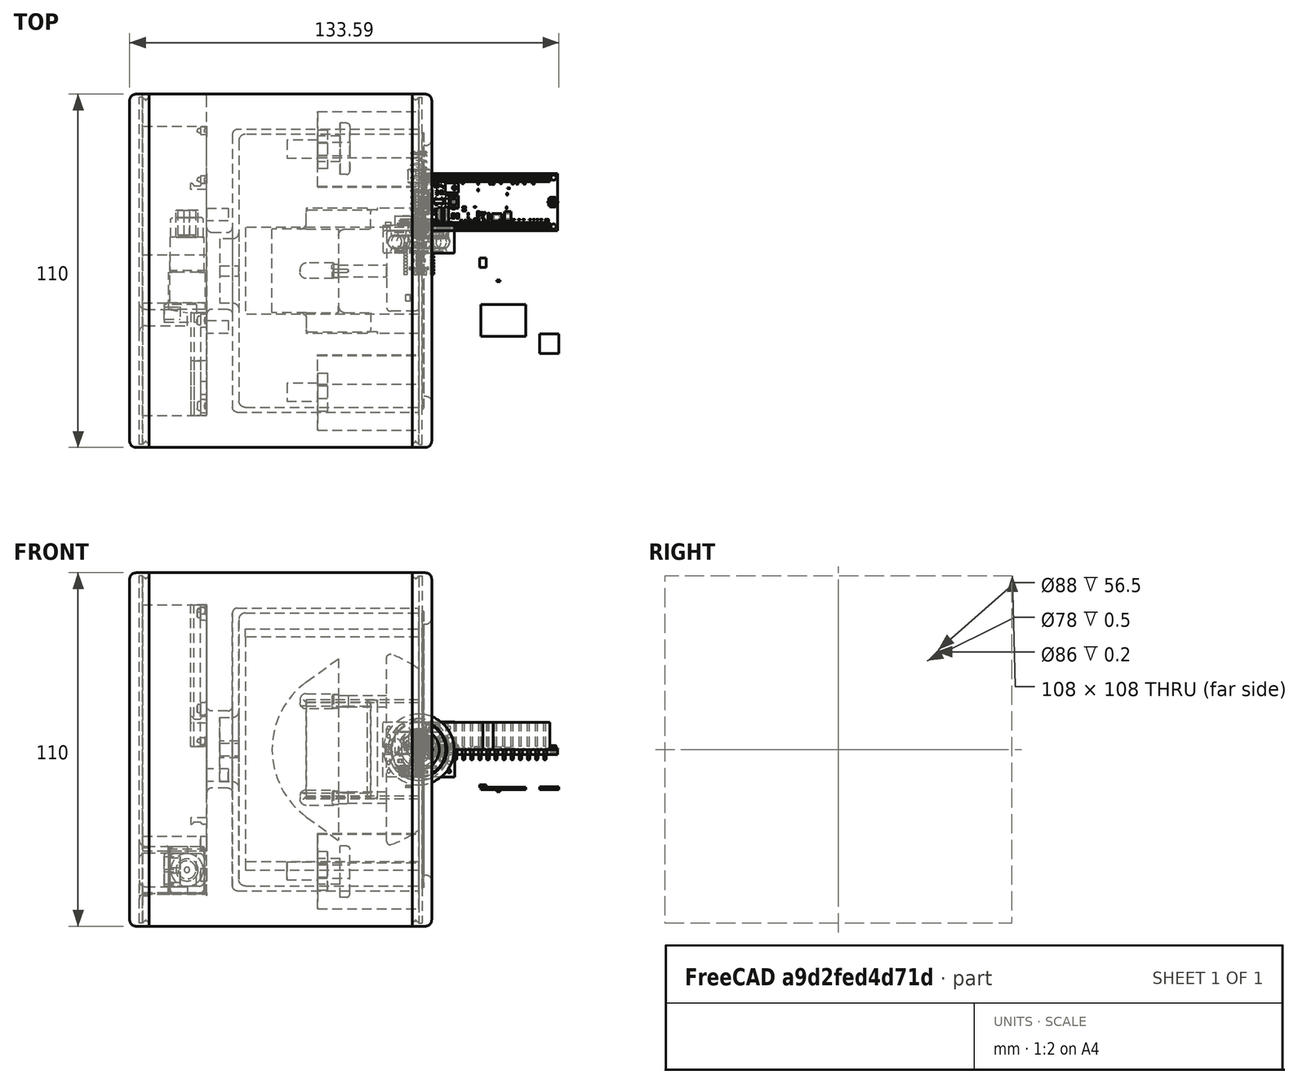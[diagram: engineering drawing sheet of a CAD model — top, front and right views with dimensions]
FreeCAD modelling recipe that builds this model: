
FCSTD DOCUMENT  (FreeCAD 1.0R39109 (Git))
Label: Watch_Winder
License: All rights reserved
LicenseURL: https://en.wikipedia.org/wiki/All_rights_reserved
objects: Part::Feature×284, App::Part×149, Sketcher::SketchObject×41, PartDesign::Fillet×24, PartDesign::Pad×20, PartDesign::Pocket×16, App::FeaturePython×16, App::Link×15, PartDesign::Body×7, PartDesign::AdditivePipe×2, PartDesign::SubtractivePipe×2, App::DocumentObjectGroup×2, PartDesign::Revolution×1, PartDesign::Chamfer×1, Assembly::JointGroup×1, Assembly::AssemblyObject×1
note: 571 computed .brp shape members not serialized (recipe doc carries the construction recipe); baked Part::Feature solids carry a one-line shape summary decoded from their .brp

FEATURE [Sketcher::SketchObject] Sketch
  ArcFitTolerance = 1e-06
  AttachmentSupport = -> [XZ_Plane]
  FullyConstrained = true
  MakeInternals = false
  MapMode = 5
  Placement = pos=(0,0,0) rot=(1,0,0;1.5708rad)
  sketch-geometry (4):
    g0: LineSegment StartX=-7.1e-15 StartY=-25 StartZ=0 EndX=3.6e-15 EndY=25 EndZ=0
    g1: LineSegment StartX=-10 StartY=-30 StartZ=0 EndX=-10 EndY=30 EndZ=0
    g2: ArcOfCircle CenterX=-18.75 CenterY=-1.9e-15 CenterZ=0 NormalX=0 NormalY=0 NormalZ=1 AngleXU=0 Radius=31.25 StartAngle=0.927295 EndAngle=1.287
    g3: ArcOfCircle CenterX=-18.75 CenterY=-1.9e-15 CenterZ=0 NormalX=0 NormalY=0 NormalZ=1 AngleXU=0 Radius=31.25 StartAngle=4.99618 EndAngle=5.35589
  constraints (11):
    c: PointOnObject(g0,g-2)
    c: DistanceY(g0,g0) = 50
    c: DistanceY(g1,g1) = 60
    c: Symmetric(g0,g0,g-1)
    c: Symmetric(g1,g1,g-1)
    c: DistanceX(g1,g0) = 10
    c: Coincident(g2,g0)
    c: Coincident(g2,g1)
    c: Coincident(g3,g0)
    c: Coincident(g3,g1)
    c: Coincident(g3,g2)
FEATURE [PartDesign::Pad] Pad  label="General_Shape"
  Direction = (0,-1,2e-16)
  Length = 25
  Length2 = 10
  Placement = pos=(0,0,0) rot=(1,0,0;1.5708rad)
  Profile = -> Sketch
  ReferenceAxis = -> Sketch [N_Axis]
  Refine = true
  Suppressed = false
  Type = 0
FEATURE [Sketcher::SketchObject] Sketch002
  ArcFitTolerance = 1e-06
  AttachmentSupport = -> [Pad]
  ExternalGeometry = -> [Pad]
  FullyConstrained = true
  MakeInternals = false
  MapMode = 5
  Placement = pos=(-10,0,-9e-16) rot=(0.707107,0,-0.707107;3.14159rad)
  sketch-geometry (3):
    g0: Circle CenterX=-15 CenterY=12.5 CenterZ=0 NormalX=0 NormalY=0 NormalZ=1 AngleXU=0 Radius=1.85
    g1: Circle CenterX=15 CenterY=12.5 CenterZ=0 NormalX=0 NormalY=0 NormalZ=1 AngleXU=0 Radius=1.85
    g2: LineSegment [constr] StartX=15 StartY=12.5 StartZ=0 EndX=-30 EndY=12.5 EndZ=0
  constraints (8):
    c: Equal(g0,g1)
    c: Diameter(g0) = 3.7
    c: Horizontal(g0,g1)
    c: DistanceX(g0,g1) = 30
    c: DistanceX(g-1,g1) = 15
    c: Coincident(g2,g1)
    c: Symmetric(g-3,g-3,g2)
    c: Horizontal(g2)
FEATURE [PartDesign::Pad] Pad002  label="Columns"
  BaseFeature = -> Pad
  Direction = (-1,0,-2e-16)
  Length = 15
  Length2 = 10
  Placement = pos=(0,0,0) rot=(1,0,0;1.5708rad)
  Profile = -> Sketch002
  ReferenceAxis = -> Sketch002 [N_Axis]
  Refine = true
  Suppressed = false
  Type = 0
FEATURE [PartDesign::Fillet] Fillet
  Base = -> Pad002 [Edge7,Edge6,Edge5,Edge1]
  BaseFeature = -> Pad002
  Placement = pos=(0,0,0) rot=(1,0,0;1.5708rad)
  Radius = 1
  Refine = true
  SupportTransform = false
  Suppressed = false
  UseAllEdges = false
FEATURE [PartDesign::Fillet] Fillet001
  Base = -> Fillet [Edge6,Edge15]
  BaseFeature = -> Fillet
  Placement = pos=(0,0,0) rot=(1,0,0;1.5708rad)
  Radius = 1
  Refine = true
  SupportTransform = false
  Suppressed = false
  UseAllEdges = false
FEATURE [Part::Feature] Part__Feature  label="SOLID"
  shape: bbox 5.553 x 25.03 x 5.575 mm, 16 faces (baked)
FEATURE [App::Part] Y_JG_WJ_A00220_01  label="Spring_0.5x5x25"
  Group = -> [Part__Feature]
  Origin = -> Origin003
  Placement = pos=(-10,-10,15) rot=(0,0,1;1.5708rad)
FEATURE [Sketcher::SketchObject] Sketch004
  ArcFitTolerance = 1e-06
  AttachmentSupport = -> [Fillet001]
  ExternalGeometry = -> [Fillet001]
  FullyConstrained = true
  MakeInternals = false
  MapMode = 5
  Placement = pos=(-25,0,-6e-15) rot=(0.707107,0,-0.707107;3.14159rad)
  sketch-geometry (2):
    g0: Circle CenterX=15 CenterY=12.5 CenterZ=0 NormalX=0 NormalY=0 NormalZ=1 AngleXU=0 Radius=2.1
    g1: Circle CenterX=-15 CenterY=12.5 CenterZ=0 NormalX=0 NormalY=0 NormalZ=1 AngleXU=0 Radius=2.1
  constraints (4):
    c: Coincident(g0,g-3)
    c: Coincident(g1,g-4)
    c: Equal(g1,g0)
    c: Diameter(g1) = 4.2
FEATURE [PartDesign::Pad] Pad003  label="Stopper"
  BaseFeature = -> Fillet001
  Direction = (-1,0,-2e-16)
  Length = 2
  Length2 = 10
  Placement = pos=(0,0,0) rot=(1,0,0;1.5708rad)
  Profile = -> Sketch004
  ReferenceAxis = -> Sketch004 [N_Axis]
  Refine = true
  Suppressed = false
  Type = 0
FEATURE [PartDesign::Fillet] Fillet004
  Base = -> Pad003 [Edge36,Edge34]
  BaseFeature = -> Pad003
  Placement = pos=(0,0,0) rot=(1,0,0;1.5708rad)
  Radius = 0.05
  Refine = true
  SupportTransform = false
  Suppressed = false
  UseAllEdges = false
FEATURE [PartDesign::Fillet] Fillet005
  Base = -> Fillet004 [Edge46,Edge27]
  BaseFeature = -> Fillet004
  Placement = pos=(0,0,0) rot=(1,0,0;1.5708rad)
  Radius = 0.4
  Refine = true
  SupportTransform = false
  Suppressed = false
  UseAllEdges = false
FEATURE [Sketcher::SketchObject] Sketch001
  ArcFitTolerance = 1e-06
  AttachmentSupport = -> [XZ_Plane001]
  FullyConstrained = true
  MakeInternals = false
  MapMode = 5
  Placement = pos=(0,0,0) rot=(1,0,0;1.5708rad)
  expr: Constraints[3] = 42 / 2 + 5
  sketch-geometry (5):
    g0: LineSegment [constr] StartX=-35 StartY=21 StartZ=0 EndX=-35 EndY=-21 EndZ=0
    g1: ArcOfCircle CenterX=-19.6703 CenterY=0 CenterZ=0 NormalX=0 NormalY=0 NormalZ=1 AngleXU=0 Radius=26 StartAngle=2.20137 EndAngle=4.08182
    g2: LineSegment StartX=-35 StartY=21 StartZ=0 EndX=-25 EndY=28.2998 EndZ=0
    g3: LineSegment StartX=-35 StartY=-21 StartZ=0 EndX=-25 EndY=-28.2998 EndZ=0
    g4: LineSegment StartX=-25 StartY=28.2998 StartZ=0 EndX=-25 EndY=-28.2998 EndZ=0
  constraints (15):
    c: DistanceY(g0,g0) = 42
    c: Coincident(g1,g0)
    c: Coincident(g1,g0)
    c: Radius(g1) = 26
    c: Vertical(g0)
    c: Coincident(g2,g0)
    c: Tangent(g2,g1)
    c: Coincident(g3,g0)
    c: Tangent(g3,g1)
    c: Coincident(g4,g2)
    c: Coincident(g4,g3)
    c: Vertical(g4)
    c: DistanceX(g0,g3) = 10
    c: PointOnObject(g1,g-1)
    c: DistanceX(g2,g-1) = 25
FEATURE [PartDesign::Pad] Pad001  label="General_Shape_R"
  Direction = (0,-1,2e-16)
  Length = 26
  Length2 = 10
  Placement = pos=(0,0,0) rot=(1,0,0;1.5708rad)
  Profile = -> Sketch001
  ReferenceAxis = -> Sketch001 [N_Axis]
  Refine = true
  Suppressed = false
  Type = 0
FEATURE [Sketcher::SketchObject] Sketch003
  ArcFitTolerance = 1e-06
  AttachmentSupport = -> [Pad001]
  ExternalGeometry = -> [Pad001]
  FullyConstrained = true
  MakeInternals = false
  MapMode = 5
  Placement = pos=(-25,0,0) rot=(0.707107,0,0.707107;3.14159rad)
  sketch-geometry (3):
    g0: Circle CenterX=-15 CenterY=13 CenterZ=0 NormalX=0 NormalY=0 NormalZ=1 AngleXU=0 Radius=2.05
    g1: Circle CenterX=15 CenterY=13 CenterZ=0 NormalX=0 NormalY=0 NormalZ=1 AngleXU=0 Radius=2.05
    g2: LineSegment [constr] StartX=15 StartY=13 StartZ=0 EndX=-28.2998 EndY=13 EndZ=0
  constraints (8):
    c: Horizontal(g1,g0)
    c: Equal(g0,g1)
    c: Diameter(g0) = 4.1
    c: DistanceX(g0,g1) = 30
    c: DistanceX(g-1,g1) = 15
    c: Coincident(g2,g1)
    c: Symmetric(g-3,g-3,g2)
    c: Horizontal(g2)
FEATURE [PartDesign::Pocket] Pocket  label="Columns_Holes"
  BaseFeature = -> Pad001
  Direction = (-1,0,2e-16)
  Length = 12
  Length2 = 5
  Placement = pos=(0,0,0) rot=(1,0,0;1.5708rad)
  Profile = -> Sketch003
  ReferenceAxis = -> Sketch003 [N_Axis]
  Refine = true
  Suppressed = false
  Type = 0
FEATURE [Sketcher::SketchObject] Sketch005
  ArcFitTolerance = 1e-06
  AttachmentSupport = -> [Pocket]
  ExternalGeometry = -> [Pocket]
  FullyConstrained = true
  MakeInternals = false
  MapMode = 5
  Placement = pos=(-37,0,8.5e-15) rot=(0.707107,0,0.707107;3.14159rad)
  sketch-geometry (2):
    g0: Circle CenterX=-15 CenterY=13 CenterZ=0 NormalX=0 NormalY=0 NormalZ=1 AngleXU=0 Radius=2.4
    g1: Circle CenterX=15 CenterY=13 CenterZ=0 NormalX=0 NormalY=0 NormalZ=1 AngleXU=0 Radius=2.4
  constraints (4):
    c: Coincident(g1,g-4)
    c: Equal(g0,g1)
    c: Diameter(g0) = 4.8
    c: Coincident(g0,g-3)
FEATURE [PartDesign::Pocket] Pocket001  label="Columns_Cavity"
  BaseFeature = -> Pocket
  Direction = (-1,0,2e-16)
  Length = 10.5
  Length2 = 5
  Placement = pos=(0,0,0) rot=(1,0,0;1.5708rad)
  Profile = -> Sketch005
  ReferenceAxis = -> Sketch005 [N_Axis]
  Refine = true
  Reversed = true
  Suppressed = false
  Type = 0
FEATURE [Sketcher::SketchObject] Sketch006
  ArcFitTolerance = 1e-06
  AttachmentSupport = -> [Pocket001]
  ExternalGeometry = -> [Pocket001]
  FullyConstrained = false
  MakeInternals = false
  MapMode = 5
  Placement = pos=(-25,0,0) rot=(0.707107,0,0.707107;3.14159rad)
  sketch-geometry (9):
    g0: LineSegment StartX=-13.504 StartY=26 StartZ=0 EndX=13.504 EndY=26 EndZ=0
    g1: LineSegment StartX=-13.504 StartY=26 StartZ=0 EndX=-15 EndY=32 EndZ=0
    g2: LineSegment StartX=13.504 StartY=26 StartZ=0 EndX=15 EndY=32 EndZ=0
    g3: LineSegment StartX=15 StartY=32 StartZ=0 EndX=-15 EndY=32 EndZ=0
    g4: LineSegment [constr] StartX=-15 StartY=13 StartZ=0 EndX=15 EndY=13 EndZ=0
    g5: LineSegment StartX=-13.504 StartY=-3.6e-15 StartZ=0 EndX=13.504 EndY=3.6e-15 EndZ=0
    g6: LineSegment StartX=-13.504 StartY=-3.6e-15 StartZ=0 EndX=-15 EndY=-6 EndZ=0
    g7: LineSegment StartX=13.504 StartY=3.6e-15 StartZ=0 EndX=15 EndY=-6 EndZ=0
    g8: LineSegment StartX=15 StartY=-6 StartZ=0 EndX=-15 EndY=-6 EndZ=0
  constraints (19):
    c: PointOnObject(g0,g-3)
    c: PointOnObject(g0,g-3)
    c: Coincident(g1,g0)
    c: Coincident(g2,g0)
    c: Coincident(g3,g2)
    c: Coincident(g3,g1)
    c: Horizontal(g3)
    c: DistanceY(g0,g1) = 6
    c: Angle(g-3,g1) = 1.81514
    c: Angle(g2,g0) = 1.81514
    c: DistanceX(g3,g3) = 30
    c: DistanceX(g-1,g2) = 15
    c: Coincident(g4,g-5)
    c: Coincident(g4,g-6)
    c: Coincident(g6,g5)
    c: Coincident(g7,g5)
    c: Coincident(g8,g7)
    c: Coincident(g8,g6)
    c: Angle(g7,g5) = -1.81514
FEATURE [PartDesign::Pad] Pad004  label="Dovetail"
  BaseFeature = -> Pocket001
  Direction = (1,0,-2e-16)
  Length = 20
  Length2 = 10
  Midplane = true
  Placement = pos=(0,0,0) rot=(1,0,0;1.5708rad)
  Profile = -> Sketch006
  ReferenceAxis = -> Sketch006 [N_Axis]
  Refine = true
  Suppressed = false
  Type = 0
FEATURE [PartDesign::Fillet] Fillet006
  Base = -> Pad004 [Edge22,Edge21,Edge13,Edge18]
  BaseFeature = -> Pad004
  Placement = pos=(0,0,0) rot=(1,0,0;1.5708rad)
  Radius = 2
  Refine = true
  SupportTransform = false
  Suppressed = false
  UseAllEdges = false
FEATURE [PartDesign::Fillet] Fillet007
  Base = -> Fillet006 [Edge43,Edge15,Edge44,Edge34,Edge48,Edge68,Edge60,Edge69]
  BaseFeature = -> Fillet006
  Placement = pos=(0,0,0) rot=(1,0,0;1.5708rad)
  Radius = 0.5
  Refine = true
  SupportTransform = false
  Suppressed = false
  UseAllEdges = false
FEATURE [PartDesign::Fillet] Fillet008
  Base = -> Fillet007 [Edge98,Edge100]
  BaseFeature = -> Fillet007
  Placement = pos=(0,0,0) rot=(1,0,0;1.5708rad)
  Radius = 2
  Refine = true
  SupportTransform = false
  Suppressed = false
  UseAllEdges = false
FEATURE [PartDesign::Body] Body001  label="Watch_Press_Rear"
  AllowCompound = false
  Group = -> [Sketch001,Pad001,Sketch003,Pocket,Sketch005,Pocket001,Sketch006,Pad004,Fillet006,Fillet007,Fillet008]
  Origin = -> Origin001
  Placement = pos=(0,0.5,0) rot=(0,0,1;0rad)
  Tip = -> Fillet008
FEATURE [Sketcher::SketchObject] Sketch007
  ArcFitTolerance = 1e-06
  AttachmentSupport = -> [Fillet005]
  ExternalGeometry = -> [Fillet005]
  FullyConstrained = false
  MakeInternals = false
  MapMode = 5
  Placement = pos=(-27,0,-6.2e-15) rot=(0.707107,0,-0.707107;3.14159rad)
  sketch-geometry (5):
    g0: LineSegment StartX=-18.2309 StartY=13 StartZ=0 EndX=-18.2309 EndY=12 EndZ=0
    g1: LineSegment StartX=-18.2309 StartY=12 StartZ=0 EndX=19.1024 EndY=12 EndZ=0
    g2: LineSegment StartX=19.1024 StartY=12 StartZ=0 EndX=19.1024 EndY=13 EndZ=0
    g3: LineSegment StartX=19.1024 StartY=13 StartZ=0 EndX=-18.2309 EndY=13 EndZ=0
    g4: LineSegment [constr] StartX=-15 StartY=12.5 StartZ=0 EndX=-18.2309 EndY=12.5 EndZ=0
  constraints (12):
    c: Coincident(g0,g1)
    c: Coincident(g1,g2)
    c: Coincident(g2,g3)
    c: Coincident(g3,g0)
    c: Vertical(g0)
    c: Vertical(g2)
    c: Horizontal(g1)
    c: Horizontal(g3)
    c: Coincident(g4,g-3)
    c: Symmetric(g0,g0,g4)
    c: Horizontal(g4)
    c: DistanceY(g0,g0) = 1
FEATURE [PartDesign::Pocket] Pocket002  label="Snap"
  BaseFeature = -> Fillet005
  Direction = (1,0,2e-16)
  Length = 5
  Length2 = 5
  Placement = pos=(0,0,0) rot=(1,0,0;1.5708rad)
  Profile = -> Sketch007
  ReferenceAxis = -> Sketch007 [N_Axis]
  Refine = true
  Suppressed = false
  Type = 0
FEATURE [PartDesign::Fillet] Fillet009
  Base = -> Pocket002 [Edge12,Edge26,Edge80,Edge79]
  BaseFeature = -> Pocket002
  Placement = pos=(0,0,0) rot=(1,0,0;1.5708rad)
  Radius = 0.3
  Refine = true
  SupportTransform = false
  Suppressed = false
  UseAllEdges = false
FEATURE [PartDesign::Body] Body  label="Watch_Press_Front"
  AllowCompound = false
  Group = -> [Sketch,Pad,Sketch002,Pad002,Fillet,Fillet001,Sketch004,Pad003,Fillet004,Fillet005,Sketch007,Pocket002,Fillet009]
  Origin = -> Origin
  Tip = -> Fillet009
FEATURE [Sketcher::SketchObject] Sketch008
  ArcFitTolerance = 1e-06
  AttachmentSupport = -> [YZ_Plane002]
  FullyConstrained = true
  MakeInternals = false
  MapMode = 5
  Placement = pos=(0,0,0) rot=(0.57735,0.57735,0.57735;2.0944rad)
  sketch-geometry (1):
    g0: Circle CenterX=-12.5 CenterY=0 CenterZ=0 NormalX=0 NormalY=0 NormalZ=1 AngleXU=0 Radius=42.5
  constraints (3):
    c: PointOnObject(g0,g-1)
    c: DistanceX(g0,g-1) = 12.5
    c: Diameter(g0) = 85
FEATURE [PartDesign::Pad] Pad005  label="Drum_Depth"
  Direction = (1,0,0)
  Length = 56
  Length2 = 10
  Placement = pos=(0,0,0) rot=(1,1,1;2.0944rad)
  Profile = -> Sketch008
  ReferenceAxis = -> Sketch008 [N_Axis]
  Refine = true
  Reversed = true
  Suppressed = false
  Type = 0
FEATURE [Sketcher::SketchObject] Sketch009
  ArcFitTolerance = 1e-06
  AttachmentSupport = -> [Pad005]
  ExternalGeometry = -> [Pad005]
  FullyConstrained = true
  MakeInternals = false
  MapMode = 5
  Placement = pos=(0,0,0) rot=(0.57735,0.57735,0.57735;2.0944rad)
  expr: Constraints[44] = 31.5 / 2
  sketch-geometry (16):
    g0: ArcOfCircle CenterX=-12.5 CenterY=0 CenterZ=0 NormalX=0 NormalY=0 NormalZ=1 AngleXU=0 Radius=37.5 StartAngle=4.34412 EndAngle=5.08066
    g1: LineSegment StartX=-26 StartY=34.9857 StartZ=0 EndX=-26 EndY=14.254 EndZ=0
    g2: LineSegment StartX=1 StartY=34.9857 StartZ=0 EndX=1 EndY=14.254 EndZ=0
    g3: LineSegment [constr] StartX=-26 StartY=34.9857 StartZ=0 EndX=1 EndY=34.9857 EndZ=0
    g4: LineSegment [constr] StartX=-26 StartY=-34.9857 StartZ=0 EndX=1 EndY=-34.9857 EndZ=0
    g5: ArcOfCircle CenterX=-12.5 CenterY=0 CenterZ=0 NormalX=0 NormalY=0 NormalZ=1 AngleXU=0 Radius=37.5 StartAngle=1.20253 EndAngle=1.93906
    g6: LineSegment StartX=-26 StartY=14.254 StartZ=0 EndX=-32 EndY=15.75 EndZ=0
    g7: LineSegment StartX=-32 StartY=15.75 StartZ=0 EndX=-32 EndY=-15.75 EndZ=0
    g8: LineSegment StartX=-32 StartY=-15.75 StartZ=0 EndX=-26 EndY=-14.254 EndZ=0
    g9: LineSegment StartX=1 StartY=14.254 StartZ=0 EndX=7 EndY=15.75 EndZ=0
    g10: LineSegment StartX=7 StartY=15.75 StartZ=0 EndX=7 EndY=-15.75 EndZ=0
    g11: LineSegment StartX=7 StartY=-15.75 StartZ=0 EndX=1 EndY=-14.254 EndZ=0
    g12: LineSegment StartX=-26 StartY=-14.254 StartZ=0 EndX=-26 EndY=-34.9857 EndZ=0
    g13: LineSegment StartX=1 StartY=-14.254 StartZ=0 EndX=1 EndY=-34.9857 EndZ=0
    g14: LineSegment [constr] StartX=-26 StartY=14.254 StartZ=0 EndX=1 EndY=14.254 EndZ=0
    g15: LineSegment [constr] StartX=-26 StartY=-14.254 StartZ=0 EndX=1 EndY=-14.254 EndZ=0
  constraints (47):
    c: Coincident(g0,g-3)
    c: Diameter(g0) = 75
    c: Vertical(g1)
    c: PointOnObject(g2,g5)
    c: Vertical(g2)
    c: Coincident(g3,g1)
    c: Coincident(g3,g2)
    c: Horizontal(g3)
    c: Coincident(g4,g12)
    c: Coincident(g4,g13)
    c: DistanceX(g3,g3) = 27
    c: Coincident(g5,g1)
    c: Coincident(g0,g12)
    c: Equal(g0,g5)
    c: Coincident(g0,g13)
    c: PointOnObject(g5,g2)
    c: Coincident(g0,g5)
    c: Coincident(g7,g6)
    c: Vertical(g7)
    c: Coincident(g8,g7)
    c: PointOnObject(g8,g12)
    c: Angle(g6,g1) = 1.81514
    c: Angle(g1,g8) = 1.81514
    c: Coincident(g10,g9)
    c: Vertical(g10)
    c: Coincident(g11,g10)
    c: PointOnObject(g11,g13)
    c: Coincident(g1,g6)
    c: PointOnObject(g12,g8)
    c: Coincident(g2,g9)
    c: PointOnObject(g13,g11)
    c: Angle(g11,g13) = 1.81514
    c: Angle(g2,g9) = 1.81514
    c: Coincident(g14,g1)
    c: Coincident(g14,g2)
    c: Horizontal(g14)
    c: Coincident(g15,g8)
    c: Coincident(g15,g11)
    c: Horizontal(g15)
    c: DistanceX(g4,g4) = 27
    c: Vertical(g13)
    c: Vertical(g12)
    c: DistanceX(g2,g9) = 6
    c: DistanceY(g7,g7) = 31.5
    c: DistanceY(g0,g6) = 15.75
    c: DistanceX(g7,g12) = 6
    c: DistanceX(g6,g1) = 6
FEATURE [PartDesign::Pocket] Pocket003  label="Press_Stand"
  BaseFeature = -> Pad005
  Direction = (-1,0,0)
  Length = 35
  Length2 = 5
  Placement = pos=(0,0,0) rot=(1,1,1;2.0944rad)
  Profile = -> Sketch009
  ReferenceAxis = -> Sketch009 [N_Axis]
  Refine = true
  Suppressed = false
  Type = 0
FEATURE [Sketcher::SketchObject] Sketch010
  ArcFitTolerance = 1e-06
  AttachmentSupport = -> [Pocket003]
  ExternalGeometry = -> [Pocket003]
  FullyConstrained = true
  MakeInternals = false
  MapMode = 5
  Placement = pos=(-35,0,0) rot=(0.57735,0.57735,0.57735;2.0944rad)
  sketch-geometry (4):
    g0: ArcOfCircle CenterX=-12.5 CenterY=1.22e-14 CenterZ=0 NormalX=0 NormalY=0 NormalZ=1 AngleXU=0 Radius=37.5 StartAngle=4.34412 EndAngle=5.08066
    g1: LineSegment StartX=-26 StartY=34.9857 StartZ=0 EndX=-26 EndY=-34.9857 EndZ=0
    g2: LineSegment StartX=1 StartY=34.9857 StartZ=0 EndX=1 EndY=-34.9857 EndZ=0
    g3: ArcOfCircle CenterX=-12.5 CenterY=1.22e-14 CenterZ=0 NormalX=0 NormalY=0 NormalZ=1 AngleXU=0 Radius=37.5 StartAngle=1.20253 EndAngle=1.93906
  constraints (11):
    c: Coincident(g0,g-3)
    c: Coincident(g1,g-3)
    c: Vertical(g1)
    c: Coincident(g2,g-3)
    c: Vertical(g2)
    c: Coincident(g3,g1)
    c: Coincident(g0,g1)
    c: Equal(g0,g3)
    c: Coincident(g0,g2)
    c: PointOnObject(g3,g2)
    c: Coincident(g0,g3)
FEATURE [PartDesign::Pocket] Pocket004  label="Press_Depth"
  BaseFeature = -> Pocket003
  Direction = (-1,0,0)
  Length = 19
  Length2 = 5
  Placement = pos=(0,0,0) rot=(1,1,1;2.0944rad)
  Profile = -> Sketch010
  ReferenceAxis = -> Sketch010 [N_Axis]
  Refine = true
  Suppressed = false
  Type = 0
FEATURE [Part::Feature] Part__Feature001  label="PRODUCT_NAME_1"
  shape: bbox 4.2 x 4.2 x 4.2 mm, 2 faces (baked)
FEATURE [Part::Feature] Part__Feature002  label="PRODUCT_NAME_002"
  shape: bbox 4.2 x 4.2 x 4.2 mm, 2 faces (baked)
FEATURE [Part::Feature] Part__Feature003  label="PRODUCT_NAME_003"
  shape: bbox 4.2 x 4.2 x 4.2 mm, 2 faces (baked)
FEATURE [Part::Feature] Part__Feature004  label="PRODUCT_NAME_004"
  shape: bbox 4.2 x 4.2 x 4.2 mm, 2 faces (baked)
FEATURE [Part::Feature] Part__Feature005  label="PRODUCT_NAME_005"
  shape: bbox 4.2 x 4.2 x 4.2 mm, 2 faces (baked)
FEATURE [Part::Feature] Part__Feature006  label="PRODUCT_NAME_006"
  shape: bbox 4.2 x 4.2 x 4.2 mm, 2 faces (baked)
FEATURE [Part::Feature] Part__Feature007  label="PRODUCT_NAME_007"
  shape: bbox 4.2 x 4.2 x 4.2 mm, 2 faces (baked)
FEATURE [Part::Feature] Part__Feature008  label="PRODUCT_NAME_008"
  shape: bbox 4.2 x 4.2 x 4.2 mm, 2 faces (baked)
FEATURE [Part::Feature] Part__Feature009  label="PRODUCT_NAME_009"
  shape: bbox 4.2 x 4.2 x 4.2 mm, 2 faces (baked)
FEATURE [Part::Feature] Part__Feature010  label="PRODUCT_NAME_010"
  shape: bbox 16.24 x 7 x 15.75 mm, 38 faces (baked)
FEATURE [Part::Feature] Part__Feature011  label="PRODUCT_NAME_011"
  shape: bbox 23.81 x 7 x 23.81 mm, 54 faces (baked)
FEATURE [App::Part] PRODUCT_NAME_1  label="608zz"
  Group = -> [Part__Feature001,Part__Feature002,Part__Feature003,Part__Feature004,Part__Feature005,Part__Feature006,Part__Feature007,Part__Feature008,Part__Feature009,Part__Feature010,Part__Feature011]
  Origin = -> Origin004
  Placement = pos=(-31.5,25.5,-38) rot=(0,0,1;1.5708rad)
FEATURE [Part::Feature] Part__Feature012  label="28BYJ-48"
  Placement = pos=(-85,-12.5,-8) rot=(0.57735,0.57735,0.57735;2.0944rad)
  shape: bbox 137.1 x 43.04 x 56 mm, 617 faces, 0 solids (baked)
FEATURE [Sketcher::SketchObject] Sketch011
  ArcFitTolerance = 1e-06
  AttachmentSupport = -> [YZ_Plane005]
  FullyConstrained = true
  MakeInternals = false
  MapMode = 5
  Placement = pos=(0,0,0) rot=(0.57735,0.57735,0.57735;2.0944rad)
  sketch-geometry (7):
    g0: LineSegment StartX=-67.5 StartY=55 StartZ=0 EndX=-67.5 EndY=-55 EndZ=0
    g1: LineSegment StartX=-67.5 StartY=-55 StartZ=0 EndX=42.5 EndY=-55 EndZ=0
    g2: LineSegment StartX=42.5 StartY=-55 StartZ=0 EndX=42.5 EndY=55 EndZ=0
    g3: LineSegment StartX=42.5 StartY=55 StartZ=0 EndX=-67.5 EndY=55 EndZ=0
    g4: LineSegment [constr] StartX=-12.5 StartY=55 StartZ=0 EndX=-12.5 EndY=-55 EndZ=0
    g5: LineSegment [constr] StartX=-67.5 StartY=-7e-16 StartZ=0 EndX=42.5 EndY=7e-16 EndZ=0
    g6: GeomPoint [constr] X=-12.5 Y=0 Z=0
  constraints (17):
    c: Coincident(g0,g1)
    c: Coincident(g1,g2)
    c: Coincident(g2,g3)
    c: Coincident(g3,g0)
    c: Vertical(g0)
    c: Vertical(g2)
    c: Horizontal(g1)
    c: Horizontal(g3)
    c: DistanceX(g3,g3) = 110
    c: DistanceY(g0,g0) = 110
    c: Symmetric(g3,g3,g4)
    c: Symmetric(g1,g1,g4)
    c: Symmetric(g0,g0,g5)
    c: Symmetric(g2,g2,g5)
    c: Symmetric(g5,g5,g6)
    c: DistanceX(g6,g-1) = 12.5
    c: PointOnObject(g6,g-1)
FEATURE [PartDesign::Pad] Pad006  label="Depth"
  Direction = (1,0,0)
  Length = 86
  Length2 = 10
  Placement = pos=(0,0,0) rot=(1,1,1;2.0944rad)
  Profile = -> Sketch011
  ReferenceAxis = -> Sketch011 [N_Axis]
  Refine = true
  Reversed = true
  Suppressed = false
  Type = 0
FEATURE [Sketcher::SketchObject] Sketch012
  ArcFitTolerance = 1e-06
  AttachmentSupport = -> [Pad006]
  ExternalGeometry = -> [Pad006]
  FullyConstrained = true
  MakeInternals = false
  MapMode = 5
  Placement = pos=(0,0,0) rot=(0.57735,0.57735,0.57735;2.0944rad)
  sketch-geometry (4):
    g0: LineSegment [constr] StartX=-67.5 StartY=2.15e-14 StartZ=0 EndX=42.5 EndY=-1.24e-14 EndZ=0
    g1: LineSegment [constr] StartX=-12.5 StartY=-55 StartZ=0 EndX=-12.5 EndY=55 EndZ=0
    g2: GeomPoint [constr] X=-12.5 Y=4.5e-15 Z=0
    g3: Circle CenterX=-12.5 CenterY=4.5e-15 CenterZ=0 NormalX=0 NormalY=0 NormalZ=1 AngleXU=0 Radius=44
  constraints (7):
    c: Symmetric(g-6,g-6,g0)
    c: Symmetric(g-5,g-5,g0)
    c: Symmetric(g-4,g-4,g1)
    c: Symmetric(g-3,g-3,g1)
    c: Symmetric(g0,g0,g2)
    c: Coincident(g3,g2)
    c: Diameter(g3) = 88
FEATURE [PartDesign::Pocket] Pocket005  label="Drum_Cavity"
  BaseFeature = -> Pad006
  Direction = (-1,0,0)
  Length = 58
  Length2 = 5
  Placement = pos=(0,0,0) rot=(1,1,1;2.0944rad)
  Profile = -> Sketch012
  ReferenceAxis = -> Sketch012 [N_Axis]
  Refine = true
  Suppressed = false
  Type = 0
FEATURE [Sketcher::SketchObject] Sketch013
  ArcFitTolerance = 1e-06
  AttachmentSupport = -> [Pocket005]
  ExternalGeometry = -> [Pocket005]
  FullyConstrained = true
  MakeInternals = false
  MapMode = 5
  Placement = pos=(0,0,0) rot=(0.57735,0.57735,0.57735;2.0944rad)
  expr: Constraints[4] = 85 / 2 + 22 / 2
  sketch-geometry (6):
    g0: LineSegment [constr] StartX=-12.5 StartY=8.7e-15 StartZ=0 EndX=42.5 EndY=-55 EndZ=0
    g1: Circle [constr] CenterX=25.3302 CenterY=-37.8302 CenterZ=0 NormalX=0 NormalY=0 NormalZ=1 AngleXU=0 Radius=11
    g2: Circle CenterX=25.3302 CenterY=-37.8302 CenterZ=0 NormalX=0 NormalY=0 NormalZ=1 AngleXU=0 Radius=11.75
    g3: LineSegment [constr] StartX=-12.5 StartY=8.7e-15 StartZ=0 EndX=-67.5 EndY=-55 EndZ=0
    g4: LineSegment [constr] StartX=25.3302 StartY=-37.8302 StartZ=0 EndX=-50.3302 EndY=-37.8302 EndZ=0
    g5: Circle CenterX=-50.3302 CenterY=-37.8302 CenterZ=0 NormalX=0 NormalY=0 NormalZ=1 AngleXU=0 Radius=11.75
  constraints (14):
    c: Coincident(g0,g-3)
    c: Coincident(g0,g-5)
    c: PointOnObject(g1,g0)
    c: Diameter(g1) = 22
    c: Distance(g1,g0) = 53.5
    c: Coincident(g2,g1)
    c: Coincident(g3,g0)
    c: Coincident(g3,g-6)
    c: Coincident(g4,g1)
    c: PointOnObject(g4,g3)
    c: Horizontal(g4)
    c: Coincident(g5,g4)
    c: Equal(g2,g5)
    c: Diameter(g2) = 23.5
FEATURE [PartDesign::Pocket] Pocket006  label="Bearing"
  BaseFeature = -> Pocket005
  Direction = (-1,0,0)
  Length = 31.5
  Length2 = 5
  Placement = pos=(0,0,0) rot=(1,1,1;2.0944rad)
  Profile = -> Sketch013
  ReferenceAxis = -> Sketch013 [N_Axis]
  Refine = true
  Suppressed = false
  Type = 0
  expr: Length = 56 / 2 + 7 / 2
FEATURE [Sketcher::SketchObject] Sketch014
  ArcFitTolerance = 1e-06
  AttachmentSupport = -> [Pocket004]
  ExternalGeometry = -> [Pocket004]
  FullyConstrained = true
  MakeInternals = false
  MapMode = 5
  Placement = pos=(-56,0,0) rot=(0.57735,0.57735,-0.57735;4.18879rad)
  sketch-geometry (1):
    g0: Circle CenterX=-12.5 CenterY=0 CenterZ=0 NormalX=0 NormalY=0 NormalZ=1 AngleXU=0 Radius=10
  constraints (2):
    c: Coincident(g0,g-3)
    c: Diameter(g0) = 20
FEATURE [PartDesign::Pad] Pad007  label="Motor_Pad"
  BaseFeature = -> Pocket004
  Direction = (-1,0,0)
  Length = 6
  Length2 = 10
  Placement = pos=(0,0,0) rot=(1,1,1;2.0944rad)
  Profile = -> Sketch014
  ReferenceAxis = -> Sketch014 [N_Axis]
  Refine = true
  Suppressed = false
  Type = 0
FEATURE [Sketcher::SketchObject] Sketch015
  ArcFitTolerance = 1e-06
  AttachmentSupport = -> [Pad007]
  ExternalGeometry = -> [Pad007]
  FullyConstrained = true
  MakeInternals = false
  MapMode = 5
  Placement = pos=(-62,0,0) rot=(0.57735,0.57735,-0.57735;4.18879rad)
  sketch-geometry (5):
    g0: ArcOfCircle CenterX=-12.5 CenterY=1.52e-14 CenterZ=0 NormalX=0 NormalY=0 NormalZ=1 AngleXU=0 Radius=2.55 StartAngle=0.917455 EndAngle=2.22414
    g1: LineSegment [constr] StartX=-10.95 StartY=-2.02485 StartZ=0 EndX=-14.05 EndY=-2.02485 EndZ=0
    g2: LineSegment StartX=-10.95 StartY=-2.02485 StartZ=0 EndX=-10.95 EndY=2.02485 EndZ=0
    g3: LineSegment StartX=-14.05 StartY=-2.02485 StartZ=0 EndX=-14.05 EndY=2.02485 EndZ=0
    g4: ArcOfCircle CenterX=-12.5 CenterY=1.52e-14 CenterZ=0 NormalX=0 NormalY=0 NormalZ=1 AngleXU=0 Radius=2.55 StartAngle=4.05905 EndAngle=5.36573
  constraints (15):
    c: Coincident(g0,g-3)
    c: Diameter(g0) = 5.1
    c: PointOnObject(g1,g4)
    c: Horizontal(g1)
    c: Coincident(g2,g1)
    c: Vertical(g2)
    c: Coincident(g3,g1)
    c: Vertical(g3)
    c: DistanceX(g1,g1) = 3.1
    c: Coincident(g4,g2)
    c: Coincident(g0,g2)
    c: Equal(g0,g4)
    c: Coincident(g0,g3)
    c: PointOnObject(g4,g3)
    c: Coincident(g0,g4)
FEATURE [PartDesign::Pocket] Pocket007  label="Motor_Axis"
  BaseFeature = -> Pad007
  Direction = (1,0,0)
  Length = 6
  Length2 = 5
  Placement = pos=(0,0,0) rot=(1,1,1;2.0944rad)
  Profile = -> Sketch015
  ReferenceAxis = -> Sketch015 [N_Axis]
  Refine = true
  Suppressed = false
  Type = 0
FEATURE [PartDesign::Fillet] Fillet010
  Base = -> Pocket007 [Edge32,Edge34,Edge33,Edge36,Edge38,Edge20,Edge21,Edge25,Edge27,Edge22]
  BaseFeature = -> Pocket007
  Placement = pos=(0,0,0) rot=(1,1,1;2.0944rad)
  Radius = 1
  Refine = true
  SupportTransform = false
  Suppressed = false
  UseAllEdges = false
FEATURE [PartDesign::Fillet] Fillet011
  Base = -> Fillet010 [Edge70]
  BaseFeature = -> Fillet010
  Placement = pos=(0,0,0) rot=(1,1,1;2.0944rad)
  Radius = 2
  Refine = true
  SupportTransform = false
  Suppressed = false
  UseAllEdges = false
FEATURE [Sketcher::SketchObject] Sketch016
  ArcFitTolerance = 1e-06
  AttachmentSupport = -> [Pocket006]
  ExternalGeometry = -> [Pocket006]
  FullyConstrained = true
  MakeInternals = false
  MapMode = 5
  Placement = pos=(-86,0,0) rot=(0.57735,0.57735,-0.57735;4.18879rad)
  expr: Constraints[20] = 90 - 35
  sketch-geometry (8):
    g0: LineSegment StartX=32.5 StartY=-45 StartZ=0 EndX=32.5 EndY=27 EndZ=0
    g1: LineSegment StartX=-22.5 StartY=45 StartZ=0 EndX=-57.5 EndY=45 EndZ=0
    g2: LineSegment StartX=-57.5 StartY=45 StartZ=0 EndX=-57.5 EndY=-45 EndZ=0
    g3: LineSegment StartX=-57.5 StartY=-45 StartZ=0 EndX=32.5 EndY=-45 EndZ=0
    g4: LineSegment [constr] StartX=-12.5 StartY=-55 StartZ=0 EndX=-12.5 EndY=55 EndZ=0
    g5: LineSegment [constr] StartX=42.5 StartY=4.18e-14 StartZ=0 EndX=-67.5 EndY=0 EndZ=0
    g6: LineSegment StartX=-22.5 StartY=27 StartZ=0 EndX=32.5 EndY=27 EndZ=0
    g7: LineSegment StartX=-22.5 StartY=27 StartZ=0 EndX=-22.5 EndY=45 EndZ=0
  constraints (22):
    c: Coincident(g1,g2)
    c: Coincident(g2,g3)
    c: Coincident(g3,g0)
    c: Vertical(g0)
    c: Vertical(g2)
    c: Horizontal(g1)
    c: Horizontal(g3)
    c: DistanceX(g3,g3) = 90
    c: Symmetric(g-3,g-3,g4)
    c: Symmetric(g-4,g-4,g4)
    c: DistanceX(g2,g4) = 45
    c: Symmetric(g-5,g-5,g5)
    c: Symmetric(g-6,g-6,g5)
    c: DistanceY(g0,g5) = 45
    c: Horizontal(g6)
    c: Coincident(g7,g6)
    c: Vertical(g7)
    c: DistanceY(g2,g2) = 90
    c: Coincident(g0,g6)
    c: Coincident(g1,g7)
    c: DistanceX(g6,g6) = 55
    c: DistanceY(g7,g7) = 18
FEATURE [PartDesign::Pocket] Pocket008  label="Rear_Cavity"
  BaseFeature = -> Pocket006
  Direction = (1,0,0)
  Length = 20
  Length2 = 5
  Placement = pos=(0,0,0) rot=(1,1,1;2.0944rad)
  Profile = -> Sketch016
  ReferenceAxis = -> Sketch016 [N_Axis]
  Refine = true
  Suppressed = false
  Type = 0
FEATURE [Sketcher::SketchObject] Sketch017
  ArcFitTolerance = 1e-06
  AttachmentSupport = -> [Pocket008]
  ExternalGeometry = -> [Pocket008]
  FullyConstrained = false
  MakeInternals = false
  MapMode = 5
  Placement = pos=(-66,0,0) rot=(0.57735,0.57735,-0.57735;4.18879rad)
  sketch-geometry (4):
    g0: LineSegment [constr] StartX=-12.5 StartY=55 StartZ=0 EndX=-12.5 EndY=-20.1023 EndZ=0
    g1: LineSegment [constr] StartX=-67.5 StartY=-6.03e-14 StartZ=0 EndX=21.0372 EndY=-6.03e-14 EndZ=0
    g2: GeomPoint [constr] X=-12.5 Y=0 Z=0
    g3: Circle CenterX=-12.5 CenterY=0 CenterZ=0 NormalX=0 NormalY=0 NormalZ=1 AngleXU=0 Radius=12
  constraints (8):
    c: Symmetric(g-3,g-3,g0)
    c: Vertical(g0)
    c: Symmetric(g-4,g-4,g1)
    c: Horizontal(g1)
    c: PointOnObject(g2,g0)
    c: PointOnObject(g2,g1)
    c: Coincident(g3,g2)
    c: Diameter(g3) = 24
FEATURE [PartDesign::Pocket] Pocket009  label="Motor_pass_through"
  BaseFeature = -> Pocket008
  Direction = (1,0,0)
  Length = 5
  Length2 = 5
  Placement = pos=(0,0,0) rot=(1,1,1;2.0944rad)
  Profile = -> Sketch017
  ReferenceAxis = -> Sketch017 [N_Axis]
  Refine = true
  Suppressed = false
  Type = 1
FEATURE [Part::Feature] Part__Feature013  label="ULN2003"
  Placement = pos=(-68,-25.25,10.25) rot=(0.57735,-0.57735,-0.57735;2.0944rad)
  shape: bbox 94.31 x 32 x 34.6 mm, 2359 faces, 0 solids (baked)
FEATURE [Part::Feature] Part__Feature014  label="Open CASCADE STEP translator 7.5 2.1.1"
  Placement = pos=(0,0,-1.60632) rot=(0,0,1;0rad)
  shape: bbox 43.18 x 17.78 x 1.606 mm, 361 faces (baked)
FEATURE [App::Part] Board
  Group = -> [Part__Feature014]
  Origin = -> Origin006
FEATURE [Part::Feature] Part__Feature015  label="CAP-0201"
  Placement = pos=(38.0693,3.4529,0) rot=(0,0,1;3.14159rad)
  shape: bbox 0.6 x 0.3076 x 0.3076 mm, 58 faces (baked)
FEATURE [App::Part] C16
  Group = -> [Part__Feature015]
  Origin = -> Origin007
FEATURE [Part::Feature] Part__Feature016  label="RES-0201"
  Placement = pos=(31.155,3.45286,0) rot=(0,0,1;3.14159rad)
  shape: bbox 0.6 x 0.3 x 0.2375 mm, 36 faces (baked)
FEATURE [App::Part] R16
  Group = -> [Part__Feature016]
  Origin = -> Origin008
FEATURE [Part::Feature] Part__Feature017  label="RES-0202"
  Placement = pos=(13.6362,14.771,0) rot=(0,0,1;3.14159rad)
  shape: bbox 0.6 x 0.3 x 0.2375 mm, 36 faces (baked)
FEATURE [App::Part] RPAD
  Group = -> [Part__Feature017]
  Origin = -> Origin009
FEATURE [Part::Feature] Part__Feature018  label="CAP-0202"
  Placement = pos=(21.7196,4.04301,0) rot=(0,0,1;3.14159rad)
  shape: bbox 0.6 x 0.3076 x 0.3076 mm, 58 faces (baked)
FEATURE [App::Part] C30
  Group = -> [Part__Feature018]
  Origin = -> Origin010
FEATURE [Part::Feature] Part__Feature019  label="CAP-0203"
  Placement = pos=(21.7196,3.44301,0) rot=(0,0,1;3.14159rad)
  shape: bbox 0.6 x 0.3076 x 0.3076 mm, 58 faces (baked)
FEATURE [App::Part] C32
  Group = -> [Part__Feature019]
  Origin = -> Origin011
FEATURE [Part::Feature] Part__Feature020  label="CAP-0204"
  Placement = pos=(29.4943,3.44248,0) rot=(0,0,0.991678;0rad)
  shape: bbox 0.6 x 0.3076 x 0.3076 mm, 58 faces (baked)
FEATURE [App::Part] C27
  Group = -> [Part__Feature020]
  Origin = -> Origin012
FEATURE [Part::Feature] Part__Feature021  label="RES-0203"
  Placement = pos=(20.6756,3.14594,0) rot=(0,0,1;1.5708rad)
  shape: bbox 0.3 x 0.6 x 0.2375 mm, 36 faces (baked)
FEATURE [App::Part] R10
  Group = -> [Part__Feature021]
  Origin = -> Origin013
FEATURE [Part::Feature] Part__Feature022  label="RES-0204"
  Placement = pos=(20.0429,3.14729,0) rot=(0,0,1;1.5708rad)
  shape: bbox 0.3 x 0.6 x 0.2375 mm, 36 faces (baked)
FEATURE [App::Part] R9
  Group = -> [Part__Feature022]
  Origin = -> Origin014
FEATURE [Part::Feature] Part__Feature023  label="RES-0205"
  Placement = pos=(6.99618,14.0061,0) rot=(0,0,1;1.5708rad)
  shape: bbox 0.3 x 0.6 x 0.2375 mm, 36 faces (baked)
FEATURE [App::Part] R23
  Group = -> [Part__Feature023]
  Origin = -> Origin015
FEATURE [Part::Feature] Part__Feature024  label="RES-0206"
  Placement = pos=(25.5132,14.7616,0) rot=(0,0,0.991678;0rad)
  shape: bbox 0.6 x 0.3 x 0.2375 mm, 36 faces (baked)
FEATURE [App::Part] R12
  Group = -> [Part__Feature024]
  Origin = -> Origin016
FEATURE [Part::Feature] Part__Feature025  label="CAP-0205"
  Placement = pos=(21.7196,4.64301,0) rot=(0,0,1;3.14159rad)
  shape: bbox 0.6 x 0.3076 x 0.3076 mm, 58 faces (baked)
FEATURE [App::Part] C6
  Group = -> [Part__Feature025]
  Origin = -> Origin017
FEATURE [Part::Feature] Part__Feature026  label="CAP-0206"
  Placement = pos=(21.7196,5.24301,0) rot=(0,0,1;3.14159rad)
  shape: bbox 0.6 x 0.3076 x 0.3076 mm, 58 faces (baked)
FEATURE [App::Part] C5
  Group = -> [Part__Feature026]
  Origin = -> Origin018
FEATURE [Part::Feature] Part__Feature027  label="RES-0207"
  Placement = pos=(3.81931,3.49148,0) rot=(0,0,0.991678;0rad)
  shape: bbox 0.6 x 0.3 x 0.2375 mm, 36 faces (baked)
FEATURE [App::Part] SJ2
  Group = -> [Part__Feature027]
  Origin = -> Origin019
FEATURE [Part::Feature] Part__Feature028  label="RES-0208"
  Placement = pos=(32.7943,14.6024,0) rot=(0,0,1;3.14159rad)
  shape: bbox 0.6 x 0.3 x 0.2375 mm, 36 faces (baked)
FEATURE [App::Part] R28
  Group = -> [Part__Feature028]
  Origin = -> Origin020
FEATURE [Part::Feature] Part__Feature029  label="RES-0209"
  Placement = pos=(3.84431,14.4915,0) rot=(0,0,0.991678;0rad)
  shape: bbox 0.6 x 0.3 x 0.2375 mm, 36 faces (baked)
FEATURE [App::Part] R25
  Group = -> [Part__Feature029]
  Origin = -> Origin021
FEATURE [Part::Feature] Part__Feature030  label="HSMx-190"
  Placement = pos=(1.89431,14.4914,0) rot=(0,0,1;3.14159rad)
  shape: bbox 1.601 x 0.8052 x 0.7957 mm, 72 faces (baked)
FEATURE [App::Part] DL2
  Group = -> [Part__Feature030]
  Origin = -> Origin022
FEATURE [Part::Feature] Part__Feature031  label="RES-0210"
  Placement = pos=(30.5463,14.6024,0) rot=(0,0,1;3.14159rad)
  shape: bbox 0.6 x 0.3 x 0.2375 mm, 36 faces (baked)
FEATURE [App::Part] R22
  Group = -> [Part__Feature031]
  Origin = -> Origin023
FEATURE [Part::Feature] Part__Feature032  label="RES-0211"
  Placement = pos=(35.6883,3.44241,0) rot=(0,0,1;3.14159rad)
  shape: bbox 0.6 x 0.3 x 0.2375 mm, 36 faces (baked)
FEATURE [App::Part] R20
  Group = -> [Part__Feature032]
  Origin = -> Origin024
FEATURE [Part::Feature] Part__Feature033  label="RES-0212"
  Placement = pos=(34.5883,3.44241,0) rot=(0,0,1;3.14159rad)
  shape: bbox 0.6 x 0.3 x 0.2375 mm, 36 faces (baked)
FEATURE [App::Part] R19
  Group = -> [Part__Feature033]
  Origin = -> Origin025
FEATURE [Part::Feature] Part__Feature034  label="RES-0213"
  Placement = pos=(27.8943,13.1915,0) rot=(0,0,0.991678;0rad)
  shape: bbox 0.6 x 0.3 x 0.2375 mm, 36 faces (baked)
FEATURE [App::Part] R18
  Group = -> [Part__Feature034]
  Origin = -> Origin026
FEATURE [Part::Feature] Part__Feature035  label="CAP-0207"
  Placement = pos=(19.8621,4.61416,0) rot=(0,0,0.991678;0rad)
  shape: bbox 0.6 x 0.3076 x 0.3076 mm, 58 faces (baked)
FEATURE [App::Part] C33
  Group = -> [Part__Feature035]
  Origin = -> Origin027
FEATURE [Part::Feature] Part__Feature036  label="CAP-0208"
  Placement = pos=(19.8621,4.01417,0) rot=(0,0,1;3.14159rad)
  shape: bbox 0.6 x 0.3076 x 0.3076 mm, 58 faces (baked)
FEATURE [App::Part] C24
  Group = -> [Part__Feature036]
  Origin = -> Origin028
FEATURE [Part::Feature] Part__Feature037  label="CAP-0209"
  Placement = pos=(20.476,5.45742,0) rot=(0,0,-1;1.5708rad)
  shape: bbox 0.3076 x 0.6 x 0.3076 mm, 58 faces (baked)
FEATURE [App::Part] C13
  Group = -> [Part__Feature037]
  Origin = -> Origin029
FEATURE [Part::Feature] Part__Feature038  label="RES-0214"
  Placement = pos=(32.5443,3.44253,0) rot=(0,0,0.991678;0rad)
  shape: bbox 0.6 x 0.3 x 0.2375 mm, 36 faces (baked)
FEATURE [App::Part] R17
  Group = -> [Part__Feature038]
  Origin = -> Origin030
FEATURE [Part::Feature] Part__Feature039  label="RES-0215"
  Placement = pos=(23.3382,14.6865,0) rot=(0,0,1;1.5708rad)
  shape: bbox 0.3 x 0.6 x 0.2375 mm, 36 faces (baked)
FEATURE [App::Part] R3
  Group = -> [Part__Feature039]
  Origin = -> Origin031
FEATURE [Part::Feature] Part__Feature040  label="SOT-523"
  Placement = pos=(5.50746,13.9614,0) rot=(1,0,0;1.5708rad)
  shape: bbox 1.6 x 1.6 x 0.8 mm, 48 faces (baked)
FEATURE [App::Part] Q1
  Group = -> [Part__Feature040]
  Origin = -> Origin032
FEATURE [Part::Feature] Part__Feature041  label="RES-0216"
  Placement = pos=(5.09435,3.31645,0) rot=(0,0,-1;1.5708rad)
  shape: bbox 0.3 x 0.6 x 0.2375 mm, 36 faces (baked)
FEATURE [App::Part] R2
  Group = -> [Part__Feature041]
  Origin = -> Origin033
FEATURE [Part::Feature] Part__Feature042  label="HSMx-191"
  Placement = pos=(1.89421,3.29145,0) rot=(0,0,0.991678;0rad)
  shape: bbox 1.601 x 0.8052 x 0.7957 mm, 72 faces (baked)
FEATURE [App::Part] DL1
  Group = -> [Part__Feature042]
  Origin = -> Origin034
FEATURE [Part::Feature] Part__Feature043  label="CAP-0210"
  Placement = pos=(7.71057,13.5715,0) rot=(0,0,1;1.5708rad)
  shape: bbox 0.3076 x 0.6 x 0.3076 mm, 58 faces (baked)
FEATURE [App::Part] C28
  Group = -> [Part__Feature043]
  Origin = -> Origin035
FEATURE [Part::Feature] Part__Feature044  label="User Library-LGA-14 2_5x3-1"
  Placement = pos=(24.2712,4.13099,0.762) rot=(-1,0,0;1.5708rad)
  shape: bbox 3 x 2.5 x 0.86 mm, 80 faces (baked)
FEATURE [App::Part] U9
  Group = -> [Part__Feature044]
  Origin = -> Origin036
FEATURE [Part::Feature] Part__Feature045  label="MP34DT06J"
  Placement = pos=(10.2842,13.3342,0) rot=(0,0,0.991678;0rad)
  shape: bbox 4 x 3 x 1 mm, 44 faces (baked)
FEATURE [App::Part] U8
  Group = -> [Part__Feature045]
  Origin = -> Origin037
FEATURE [Part::Feature] Part__Feature046  label="Header _Fem_1X8"
  Placement = pos=(30.3323,16.5014,0) rot=(0,0.707107,0.707107;3.14159rad)
  shape: bbox 20.82 x 2.54 x 11.7 mm, 134 faces (baked)
FEATURE [Part::Feature] Part__Feature047  label="Header _Fem_1X009"
  Placement = pos=(12.6832,16.5014,0) rot=(1,0,0;1.5708rad)
  shape: bbox 20.82 x 2.54 x 11.7 mm, 134 faces (baked)
FEATURE [App::Part] JP3
  Group = -> [Part__Feature046,Part__Feature047]
  Origin = -> Origin038
FEATURE [Part::Feature] Part__Feature048  label="Extruded"
  shape: bbox 0.2 x 0.2 x 0.85 mm, 22 faces (baked)
FEATURE [App::Part] _138194336  label="7138194336"
  Group = -> [Part__Feature048]
  Origin = -> Origin039
  Placement = pos=(28.2269,14.708,0.0499999) rot=(0,0,1;0rad)
FEATURE [Part::Feature] Part__Feature049  label="Extruded001"
  shape: bbox 1.6 x 1.2 x 0.86 mm, 7 faces (baked)
FEATURE [App::Part] _138189936  label="7138189936"
  Group = -> [Part__Feature049]
  Origin = -> Origin040
  Placement = pos=(27.6719,14.333,0.0199999) rot=(0,0,1;0rad)
FEATURE [App::Part] U7
  Group = -> [_138194336,_138189936]
  Origin = -> Origin041
FEATURE [Part::Feature] Part__Feature050  label="RES-0217"
  Placement = pos=(5.5909,11.2714,0) rot=(0,0,1;3.14159rad)
  shape: bbox 0.6 x 0.3 x 0.2375 mm, 36 faces (baked)
FEATURE [App::Part] R15
  Group = -> [Part__Feature050]
  Origin = -> Origin042
FEATURE [Part::Feature] Part__Feature051  label="RES-0218"
  Placement = pos=(5.59431,12.4117,0) rot=(0,0,1;3.14159rad)
  shape: bbox 0.6 x 0.3 x 0.2375 mm, 36 faces (baked)
FEATURE [App::Part] R14
  Group = -> [Part__Feature051]
  Origin = -> Origin043
FEATURE [Part::Feature] Part__Feature052  label="RES-0219"
  Placement = pos=(5.59431,11.8414,0) rot=(0,0,1;3.14159rad)
  shape: bbox 0.6 x 0.3 x 0.2375 mm, 36 faces (baked)
FEATURE [App::Part] R13
  Group = -> [Part__Feature052]
  Origin = -> Origin044
FEATURE [Part::Feature] Part__Feature053  label="SMLP34RGB"
  Placement = pos=(7.08928,11.8914,0) rot=(0,0,1;1.5708rad)
  shape: bbox 1.076 x 1 x 0.2004 mm, 116 faces (baked)
FEATURE [App::Part] DL3
  Group = -> [Part__Feature053]
  Origin = -> Origin045
FEATURE [Part::Feature] Part__Feature054  label="Open CASCADE STEP translator 6.8 13.1"
  Placement = pos=(-3.05,-2.55,0) rot=(0,0,1;0rad)
  shape: bbox 0.7625 x 0.7625 x 2e-07 mm, 1 faces, 0 solids (baked)
FEATURE [Part::Feature] Part__Feature055  label="Open CASCADE STEP translator 6.8 13.2.1"
  shape: bbox 6.1 x 5.1 x 0.55 mm, 8 faces (baked)
FEATURE [App::Part] Body004
  Group = -> [Part__Feature055]
  Origin = -> Origin046
  Placement = pos=(-3.05,-2.55,0) rot=(0,0,1;0rad)
FEATURE [Part::Feature] Part__Feature056  label="Thermal_Shape"
  Placement = pos=(-1.7,-2,0) rot=(0,0,1;0rad)
  shape: bbox 3.4 x 4 x 0.05 mm, 7 faces (baked)
FEATURE [Part::Feature] Part__Feature057  label="Open CASCADE STEP translator 6.8 13.4.1"
  shape: bbox 0.625 x 0.415 x 0.05 mm, 6 faces (baked)
FEATURE [Part::Feature] Part__Feature058  label="Open CASCADE STEP translator 6.8 13.4.2"
  shape: bbox 2e-07 x 0.415 x 0.2 mm, 1 faces, 0 solids (baked)
FEATURE [App::Part] Pin_Shape
  Group = -> [Part__Feature057,Part__Feature058]
  Origin = -> Origin047
  Placement = pos=(-3.05,-2.1125,0) rot=(0,0,1;0rad)
FEATURE [Part::Feature] Part__Feature059  label="Open CASCADE STEP translator 6.8 13.4.003"
  shape: bbox 0.625 x 0.415 x 0.05 mm, 6 faces (baked)
FEATURE [Part::Feature] Part__Feature060  label="Open CASCADE STEP translator 6.8 13.4.004"
  shape: bbox 2e-07 x 0.415 x 0.2 mm, 1 faces, 0 solids (baked)
FEATURE [App::Part] Pin_Shape001
  Group = -> [Part__Feature059,Part__Feature060]
  Origin = -> Origin048
  Placement = pos=(-3.05,-0.8425,0) rot=(0,0,1;0rad)
FEATURE [Part::Feature] Part__Feature061  label="Open CASCADE STEP translator 6.8 13.4.005"
  shape: bbox 0.625 x 0.415 x 0.05 mm, 6 faces (baked)
FEATURE [Part::Feature] Part__Feature062  label="Open CASCADE STEP translator 6.8 13.4.006"
  shape: bbox 2e-07 x 0.415 x 0.2 mm, 1 faces, 0 solids (baked)
FEATURE [App::Part] Pin_Shape002
  Group = -> [Part__Feature061,Part__Feature062]
  Origin = -> Origin049
  Placement = pos=(-3.05,0.4275,0) rot=(0,0,1;0rad)
FEATURE [Part::Feature] Part__Feature063  label="Open CASCADE STEP translator 6.8 13.4.007"
  shape: bbox 0.625 x 0.415 x 0.05 mm, 6 faces (baked)
FEATURE [Part::Feature] Part__Feature064  label="Open CASCADE STEP translator 6.8 13.4.008"
  shape: bbox 2e-07 x 0.415 x 0.2 mm, 1 faces, 0 solids (baked)
FEATURE [App::Part] Pin_Shape003
  Group = -> [Part__Feature063,Part__Feature064]
  Origin = -> Origin050
  Placement = pos=(-3.05,1.6975,0) rot=(0,0,1;0rad)
FEATURE [Part::Feature] Part__Feature065  label="Open CASCADE STEP translator 6.8 13.4.009"
  shape: bbox 0.625 x 0.415 x 0.05 mm, 6 faces (baked)
FEATURE [Part::Feature] Part__Feature066  label="Open CASCADE STEP translator 6.8 13.4.010"
  shape: bbox 2e-07 x 0.415 x 0.2 mm, 1 faces, 0 solids (baked)
FEATURE [App::Part] Pin_Shape004
  Group = -> [Part__Feature065,Part__Feature066]
  Origin = -> Origin051
  Placement = pos=(3.05,-1.6975,0) rot=(0,0,1;3.14159rad)
FEATURE [Part::Feature] Part__Feature067  label="Open CASCADE STEP translator 6.8 13.4.011"
  shape: bbox 0.625 x 0.415 x 0.05 mm, 6 faces (baked)
FEATURE [Part::Feature] Part__Feature068  label="Open CASCADE STEP translator 6.8 13.4.012"
  shape: bbox 2e-07 x 0.415 x 0.2 mm, 1 faces, 0 solids (baked)
FEATURE [App::Part] Pin_Shape005
  Group = -> [Part__Feature067,Part__Feature068]
  Origin = -> Origin052
  Placement = pos=(3.05,-0.4275,0) rot=(0,0,1;3.14159rad)
FEATURE [Part::Feature] Part__Feature069  label="Open CASCADE STEP translator 6.8 13.4.013"
  shape: bbox 0.625 x 0.415 x 0.05 mm, 6 faces (baked)
FEATURE [Part::Feature] Part__Feature070  label="Open CASCADE STEP translator 6.8 13.4.014"
  shape: bbox 2e-07 x 0.415 x 0.2 mm, 1 faces, 0 solids (baked)
FEATURE [App::Part] Pin_Shape006
  Group = -> [Part__Feature069,Part__Feature070]
  Origin = -> Origin053
  Placement = pos=(3.05,0.8425,0) rot=(0,0,1;3.14159rad)
FEATURE [Part::Feature] Part__Feature071  label="Open CASCADE STEP translator 6.8 13.4.015"
  shape: bbox 0.625 x 0.415 x 0.05 mm, 6 faces (baked)
FEATURE [Part::Feature] Part__Feature072  label="Open CASCADE STEP translator 6.8 13.4.016"
  shape: bbox 2e-07 x 0.415 x 0.2 mm, 1 faces, 0 solids (baked)
FEATURE [App::Part] Pin_Shape007
  Group = -> [Part__Feature071,Part__Feature072]
  Origin = -> Origin054
  Placement = pos=(3.05,2.1125,0) rot=(0,0,1;3.14159rad)
FEATURE [App::Part] _211587936  label="7211587936"
  Group = -> [Part__Feature054,Body004,Part__Feature056,Pin_Shape,Pin_Shape001,Pin_Shape002,Pin_Shape003,Pin_Shape004,Pin_Shape005,Pin_Shape006,Pin_Shape007]
  Origin = -> Origin055
  Placement = pos=(15.2662,11.0011,0) rot=(0,0,-1;1.5708rad)
FEATURE [App::Part] U5
  Group = -> [_211587936]
  Origin = -> Origin056
FEATURE [Part::Feature] Part__Feature073  label="RES-0220"
  Placement = pos=(18.45,14.6911,0) rot=(0,0,-1;1.5708rad)
  shape: bbox 0.3 x 0.6 x 0.2375 mm, 36 faces (baked)
FEATURE [App::Part] R11
  Group = -> [Part__Feature073]
  Origin = -> Origin057
FEATURE [Part::Feature] Part__Feature074  label="CAP-0211"
  Placement = pos=(17.4462,7.38108,0) rot=(0,0,0.991678;0rad)
  shape: bbox 0.6 x 0.3076 x 0.3076 mm, 58 faces (baked)
FEATURE [App::Part] C26
  Group = -> [Part__Feature074]
  Origin = -> Origin058
FEATURE [Part::Feature] Part__Feature075  label="CAP-0212"
  Placement = pos=(18.45,12.625,0) rot=(0,0,1;1.5708rad)
  shape: bbox 0.3076 x 0.6 x 0.3076 mm, 58 faces (baked)
FEATURE [App::Part] C21
  Group = -> [Part__Feature075]
  Origin = -> Origin059
FEATURE [Part::Feature] Part__Feature076  label="CAP-0213"
  Placement = pos=(19.9278,5.45742,0) rot=(0,0,-1;1.5708rad)
  shape: bbox 0.3076 x 0.6 x 0.3076 mm, 58 faces (baked)
FEATURE [App::Part] C18
  Group = -> [Part__Feature076]
  Origin = -> Origin060
FEATURE [Part::Feature] Part__Feature077  label="ATECC608A-MAH"
  Placement = pos=(27.6543,4.49142,0) rot=(0,0,1;3.14159rad)
  shape: bbox 2 x 3 x 0.55 mm, 56 faces (baked)
FEATURE [App::Part] U4
  Group = -> [Part__Feature077]
  Origin = -> Origin061
FEATURE [Part::Feature] Part__Feature078  label="PCB"
  Placement = pos=(30.6817,-31.292,-13.3123) rot=(0,0,1;0rad)
  shape: bbox 14 x 10 x 0.8 mm, 6 faces (baked)
FEATURE [App::Part] PCB  label="PCB001"
  Group = -> [Part__Feature078]
  Origin = -> Origin062
  Placement = pos=(-1.15818,-1.34837,0) rot=(0,0,1;0rad)
FEATURE [App::Part] _4x10_0_PCB  label="14x10.0 PCB"
  Group = -> [PCB]
  Origin = -> Origin063
  Placement = pos=(-34.0434,-15.9735,12.5523) rot=(0,0,1;1.5708rad)
FEATURE [Part::Feature] Part__Feature079  label="Part9"
  Placement = pos=(1.22143,-17.55,-0.142857) rot=(0,0,1;0rad)
  shape: bbox 0.7 x 1.15 x 0.01 mm, 6 faces (baked)
FEATURE [Part::Feature] Part__Feature080  label="Part010"
  Placement = pos=(2.22143,-17.55,-0.142857) rot=(0,0,1;0rad)
  shape: bbox 0.7 x 1.15 x 0.01 mm, 6 faces (baked)
FEATURE [Part::Feature] Part__Feature081  label="Part011"
  Placement = pos=(3.22143,-17.55,-0.142857) rot=(0,0,1;0rad)
  shape: bbox 0.7 x 1.15 x 0.01 mm, 6 faces (baked)
FEATURE [Part::Feature] Part__Feature082  label="Part012"
  Placement = pos=(4.22143,-17.55,-0.142857) rot=(0,0,1;0rad)
  shape: bbox 0.7 x 1.15 x 0.01 mm, 6 faces (baked)
FEATURE [Part::Feature] Part__Feature083  label="Part013"
  Placement = pos=(5.22143,-17.55,-0.142857) rot=(0,0,1;0rad)
  shape: bbox 0.7 x 1.15 x 0.01 mm, 6 faces (baked)
FEATURE [Part::Feature] Part__Feature084  label="Part014"
  Placement = pos=(-8.55,-16.4214,-0.142857) rot=(0,0,-1;1.5708rad)
  shape: bbox 1.15 x 0.7 x 0.01 mm, 6 faces (baked)
FEATURE [Part::Feature] Part__Feature085  label="Part015"
  Placement = pos=(-8.55,-15.4214,-0.142857) rot=(0,0,-1;1.5708rad)
  shape: bbox 1.15 x 0.7 x 0.01 mm, 6 faces (baked)
FEATURE [Part::Feature] Part__Feature086  label="Part016"
  Placement = pos=(-8.55,-14.4214,-0.142857) rot=(0,0,-1;1.5708rad)
  shape: bbox 1.15 x 0.7 x 0.01 mm, 6 faces (baked)
FEATURE [Part::Feature] Part__Feature087  label="Part017"
  Placement = pos=(-8.55,-13.4214,-0.142857) rot=(0,0,-1;1.5708rad)
  shape: bbox 1.15 x 0.7 x 0.01 mm, 6 faces (baked)
FEATURE [Part::Feature] Part__Feature088  label="Part018"
  Placement = pos=(-8.55,-12.4214,-0.142857) rot=(0,0,-1;1.5708rad)
  shape: bbox 1.15 x 0.7 x 0.01 mm, 6 faces (baked)
FEATURE [Part::Feature] Part__Feature089  label="Part019"
  Placement = pos=(-8.55,-11.4214,-0.142857) rot=(0,0,-1;1.5708rad)
  shape: bbox 1.15 x 0.7 x 0.01 mm, 6 faces (baked)
FEATURE [Part::Feature] Part__Feature090  label="Part020"
  Placement = pos=(-8.55,-10.4214,-0.142857) rot=(0,0,-1;1.5708rad)
  shape: bbox 1.15 x 0.7 x 0.01 mm, 6 faces (baked)
FEATURE [Part::Feature] Part__Feature091  label="Part021"
  Placement = pos=(-8.55,-9.42143,-0.142857) rot=(0,0,-1;1.5708rad)
  shape: bbox 1.15 x 0.7 x 0.01 mm, 6 faces (baked)
FEATURE [Part::Feature] Part__Feature092  label="Part022"
  Placement = pos=(-8.55,-8.42143,-0.142857) rot=(0,0,-1;1.5708rad)
  shape: bbox 1.15 x 0.7 x 0.01 mm, 6 faces (baked)
FEATURE [Part::Feature] Part__Feature093  label="Part023"
  Placement = pos=(-8.55,-7.42143,-0.142857) rot=(0,0,-1;1.5708rad)
  shape: bbox 1.15 x 0.7 x 0.01 mm, 6 faces (baked)
FEATURE [Part::Feature] Part__Feature094  label="Part024"
  Placement = pos=(-0.3,-16.4214,-0.142857) rot=(0,0,-1;1.5708rad)
  shape: bbox 1.15 x 0.7 x 0.01 mm, 6 faces (baked)
FEATURE [Part::Feature] Part__Feature095  label="Part025"
  Placement = pos=(-0.3,-15.4214,-0.142857) rot=(0,0,-1;1.5708rad)
  shape: bbox 1.15 x 0.7 x 0.01 mm, 6 faces (baked)
FEATURE [Part::Feature] Part__Feature096  label="Part026"
  Placement = pos=(-0.3,-14.4214,-0.142857) rot=(0,0,-1;1.5708rad)
  shape: bbox 1.15 x 0.7 x 0.01 mm, 6 faces (baked)
FEATURE [Part::Feature] Part__Feature097  label="Part027"
  Placement = pos=(-0.3,-13.4214,-0.142857) rot=(0,0,-1;1.5708rad)
  shape: bbox 1.15 x 0.7 x 0.01 mm, 6 faces (baked)
FEATURE [Part::Feature] Part__Feature098  label="Part028"
  Placement = pos=(-0.3,-12.4214,-0.142857) rot=(0,0,-1;1.5708rad)
  shape: bbox 1.15 x 0.7 x 0.01 mm, 6 faces (baked)
FEATURE [Part::Feature] Part__Feature099  label="Part029"
  Placement = pos=(-0.3,-11.4214,-0.142857) rot=(0,0,-1;1.5708rad)
  shape: bbox 1.15 x 0.7 x 0.01 mm, 6 faces (baked)
FEATURE [Part::Feature] Part__Feature100  label="Part030"
  Placement = pos=(-0.3,-10.4214,-0.142857) rot=(0,0,-1;1.5708rad)
  shape: bbox 1.15 x 0.7 x 0.01 mm, 6 faces (baked)
FEATURE [Part::Feature] Part__Feature101  label="Part031"
  Placement = pos=(-0.3,-9.42143,-0.142857) rot=(0,0,-1;1.5708rad)
  shape: bbox 1.15 x 0.7 x 0.01 mm, 6 faces (baked)
FEATURE [Part::Feature] Part__Feature102  label="Part032"
  Placement = pos=(-0.3,-8.42143,-0.142857) rot=(0,0,-1;1.5708rad)
  shape: bbox 1.15 x 0.7 x 0.01 mm, 6 faces (baked)
FEATURE [Part::Feature] Part__Feature103  label="Part033"
  Placement = pos=(-0.3,-7.42143,-0.142857) rot=(0,0,-1;1.5708rad)
  shape: bbox 1.15 x 0.7 x 0.01 mm, 6 faces (baked)
FEATURE [Part::Feature] Part__Feature104  label="Part034"
  Placement = pos=(1.22143,-8.7,-0.142857) rot=(0,0,1;0rad)
  shape: bbox 0.7 x 1.15 x 0.01 mm, 6 faces (baked)
FEATURE [Part::Feature] Part__Feature105  label="Part035"
  Placement = pos=(2.22143,-8.7,-0.142857) rot=(0,0,1;0rad)
  shape: bbox 0.7 x 1.15 x 0.01 mm, 6 faces (baked)
FEATURE [Part::Feature] Part__Feature106  label="Part036"
  Placement = pos=(3.22143,-8.7,-0.142857) rot=(0,0,1;0rad)
  shape: bbox 0.7 x 1.15 x 0.01 mm, 6 faces (baked)
FEATURE [Part::Feature] Part__Feature107  label="Part037"
  Placement = pos=(4.22143,-8.7,-0.142857) rot=(0,0,1;0rad)
  shape: bbox 0.7 x 1.15 x 0.01 mm, 6 faces (baked)
FEATURE [Part::Feature] Part__Feature108  label="Part038"
  Placement = pos=(5.22143,-8.7,-0.142857) rot=(0,0,1;0rad)
  shape: bbox 0.7 x 1.15 x 0.01 mm, 6 faces (baked)
FEATURE [Part::Feature] Part__Feature109  label="Part039"
  Placement = pos=(-1.82344,-10.6064,-0.142857) rot=(0,0,-1;1.5708rad)
  shape: bbox 0.7 x 0.7 x 0.01 mm, 6 faces (baked)
FEATURE [Part::Feature] Part__Feature110  label="Part040"
  Placement = pos=(-0.673438,-10.6064,-0.142857) rot=(0,0,-1;1.5708rad)
  shape: bbox 0.7 x 0.7 x 0.01 mm, 6 faces (baked)
FEATURE [Part::Feature] Part__Feature111  label="Part041"
  Placement = pos=(-2.97344,-9.45643,-0.142857) rot=(0,0,-1;1.5708rad)
  shape: bbox 0.7 x 0.7 x 0.01 mm, 6 faces (baked)
FEATURE [Part::Feature] Part__Feature112  label="Part042"
  Placement = pos=(-1.82344,-9.45643,-0.142857) rot=(0,0,-1;1.5708rad)
  shape: bbox 0.7 x 0.7 x 0.01 mm, 6 faces (baked)
FEATURE [Part::Feature] Part__Feature113  label="Part043"
  Placement = pos=(-0.673438,-9.45643,-0.142857) rot=(0,0,-1;1.5708rad)
  shape: bbox 0.7 x 0.7 x 0.01 mm, 6 faces (baked)
FEATURE [Part::Feature] Part__Feature114  label="Part044"
  Placement = pos=(0.476562,-9.45643,-0.142857) rot=(0,0,-1;1.5708rad)
  shape: bbox 0.7 x 0.7 x 0.01 mm, 6 faces (baked)
FEATURE [Part::Feature] Part__Feature115  label="Part045"
  Placement = pos=(-1.82344,-8.30643,-0.142857) rot=(0,0,-1;1.5708rad)
  shape: bbox 0.7 x 0.7 x 0.01 mm, 6 faces (baked)
FEATURE [Part::Feature] Part__Feature116  label="Part046"
  Placement = pos=(-0.673438,-8.30643,-0.142857) rot=(0,0,-1;1.5708rad)
  shape: bbox 0.7 x 0.7 x 0.01 mm, 6 faces (baked)
FEATURE [Part::Feature] Part__Feature117  label="Part047"
  Placement = pos=(-2.97344,-7.15643,-0.142857) rot=(0,0,-1;1.5708rad)
  shape: bbox 0.7 x 0.7 x 0.01 mm, 6 faces (baked)
FEATURE [Part::Feature] Part__Feature118  label="Part048"
  Placement = pos=(-1.82344,-7.15643,-0.142857) rot=(0,0,-1;1.5708rad)
  shape: bbox 0.7 x 0.7 x 0.01 mm, 6 faces (baked)
FEATURE [Part::Feature] Part__Feature119  label="Part049"
  Placement = pos=(-0.673438,-7.15643,-0.142857) rot=(0,0,-1;1.5708rad)
  shape: bbox 0.7 x 0.7 x 0.01 mm, 6 faces (baked)
FEATURE [Part::Feature] Part__Feature120  label="Part050"
  Placement = pos=(0.476562,-7.15643,-0.142857) rot=(0,0,-1;1.5708rad)
  shape: bbox 0.7 x 0.7 x 0.01 mm, 6 faces (baked)
FEATURE [Part::Feature] Part__Feature121  label="Part051"
  Placement = pos=(-3.99844,-11.9314,-0.142857) rot=(0,0,-1;1.5708rad)
  shape: bbox 0.7 x 0.7 x 0.01 mm, 6 faces (baked)
FEATURE [Part::Feature] Part__Feature122  label="Part052"
  Placement = pos=(-2.89844,-11.9314,-0.142857) rot=(0,0,-1;1.5708rad)
  shape: bbox 0.7 x 0.7 x 0.01 mm, 6 faces (baked)
FEATURE [Part::Feature] Part__Feature123  label="Part053"
  Placement = pos=(-1.79844,-11.9314,-0.142857) rot=(0,0,-1;1.5708rad)
  shape: bbox 0.7 x 0.7 x 0.01 mm, 6 faces (baked)
FEATURE [Part::Feature] Part__Feature124  label="Part054"
  Placement = pos=(-0.698438,-11.9314,-0.142857) rot=(0,0,-1;1.5708rad)
  shape: bbox 0.7 x 0.7 x 0.01 mm, 6 faces (baked)
FEATURE [Part::Feature] Part__Feature125  label="Part055"
  Placement = pos=(0.401562,-11.9314,-0.142857) rot=(0,0,-1;1.5708rad)
  shape: bbox 0.7 x 0.7 x 0.01 mm, 6 faces (baked)
FEATURE [Part::Feature] Part__Feature126  label="Part056"
  Placement = pos=(1.50156,-11.9314,-0.142857) rot=(0,0,-1;1.5708rad)
  shape: bbox 0.7 x 0.7 x 0.01 mm, 6 faces (baked)
FEATURE [App::Part] NINA_pads  label="NINA-pads"
  Group = -> [Part__Feature079,Part__Feature080,Part__Feature081,Part__Feature082,Part__Feature083,Part__Feature084,Part__Feature085,Part__Feature086,Part__Feature087,Part__Feature088,Part__Feature089,Part__Feature090,Part__Feature091,Part__Feature092,Part__Feature093,Part__Feature094,Part__Feature095,Part__Feature096,Part__Feature097,Part__Feature098,Part__Feature099,Part__Feature100,Part__Feature101,+25 more]
  Origin = -> Origin064
  Placement = pos=(-4.75303,16.1,-1.7e-15) rot=(0,0,1;0rad)
FEATURE [Part::Feature] Part__Feature127  label="Part49"
  Placement = pos=(0,0,-0.514074) rot=(0,0,1;0rad)
  shape: bbox 9.6 x 9.5 x 1.4 mm, 47 faces (baked)
FEATURE [App::Part] Shield_box  label="Shield box"
  Group = -> [Part__Feature127]
  Origin = -> Origin065
  Placement = pos=(20.0317,-10.292,-10.0114) rot=(0,0,1;0rad)
FEATURE [App::Part] Shieldbox
  Group = -> [Shield_box]
  Origin = -> Origin066
  Placement = pos=(-12.695,-17.1317,12.5255) rot=(0,0,1;1.5708rad)
FEATURE [Part::Feature] Part__Feature128  label="Package"
  Placement = pos=(30.0486,-14.2306,-14.6507) rot=(0,0,1;3.14159rad)
  shape: bbox 2 x 3 x 0.8 mm, 6 faces (baked)
FEATURE [App::Part] Flash
  Group = -> [Part__Feature128]
  Origin = -> Origin067
  Placement = pos=(18.5148,-5.31839,12.7176) rot=(0,0,1;3.14159rad)
FEATURE [Part::Feature] Part__Feature129  label="Part57"
  Placement = pos=(40.646,-34.7577,-15.6591) rot=(0,0,1;0rad)
  shape: bbox 6 x 6 x 0.9 mm, 6 faces (baked)
FEATURE [App::Part] ESP32
  Group = -> [Part__Feature129]
  Origin = -> Origin068
  Placement = pos=(-40.9979,47.5989,-10.7123) rot=(0.707107,-0.707107,0;3.14159rad)
FEATURE [Part::Feature] Part__Feature130  label="Part83"
  Placement = pos=(-1.10414,-6.80865,-2.54666) rot=(0,0,1;0rad)
  shape: bbox 0.15 x 0.3 x 0.33 mm, 6 faces (baked)
FEATURE [Part::Feature] Part__Feature131  label="Part057"
  Placement = pos=(-0.654141,-6.80865,-2.54666) rot=(0,0,1;0rad)
  shape: bbox 0.15 x 0.3 x 0.33 mm, 6 faces (baked)
FEATURE [Part::Feature] Part__Feature132  label="Part058"
  Placement = pos=(-0.879141,-6.80865,-2.54666) rot=(0,0,1;0rad)
  shape: bbox 0.3 x 0.3 x 0.33 mm, 6 faces (baked)
FEATURE [App::Part] C_0201  label="C 0201"
  Group = -> [Part__Feature130,Part__Feature131,Part__Feature132]
  Origin = -> Origin069
  Placement = pos=(6.0018,-1.76916,0.84388) rot=(0,0,-1;1.5708rad)
FEATURE [Part::Feature] Part__Feature133  label="Part059"
  Placement = pos=(-1.10414,-6.80865,-2.54666) rot=(0,0,1;0rad)
  shape: bbox 0.15 x 0.3 x 0.33 mm, 6 faces (baked)
FEATURE [Part::Feature] Part__Feature134  label="Part060"
  Placement = pos=(-0.654141,-6.80865,-2.54666) rot=(0,0,1;0rad)
  shape: bbox 0.15 x 0.3 x 0.33 mm, 6 faces (baked)
FEATURE [Part::Feature] Part__Feature135  label="Part061"
  Placement = pos=(-0.879141,-6.80865,-2.54666) rot=(0,0,1;0rad)
  shape: bbox 0.3 x 0.3 x 0.33 mm, 6 faces (baked)
FEATURE [App::Part] C_0202  label="C 0202"
  Group = -> [Part__Feature133,Part__Feature134,Part__Feature135]
  Origin = -> Origin070
  Placement = pos=(-2.37388,15.0886,0.84388) rot=(0,0,1;0rad)
FEATURE [Part::Feature] Part__Feature136  label="Part062"
  Placement = pos=(-1.10414,-6.80865,-2.54666) rot=(0,0,1;0rad)
  shape: bbox 0.15 x 0.3 x 0.33 mm, 6 faces (baked)
FEATURE [Part::Feature] Part__Feature137  label="Part063"
  Placement = pos=(-0.654141,-6.80865,-2.54666) rot=(0,0,1;0rad)
  shape: bbox 0.15 x 0.3 x 0.33 mm, 6 faces (baked)
FEATURE [Part::Feature] Part__Feature138  label="Part064"
  Placement = pos=(-0.879141,-6.80865,-2.54666) rot=(0,0,1;0rad)
  shape: bbox 0.3 x 0.3 x 0.33 mm, 6 faces (baked)
FEATURE [App::Part] C_0203  label="C 0203"
  Group = -> [Part__Feature136,Part__Feature137,Part__Feature138]
  Origin = -> Origin071
  Placement = pos=(-11.4129,3.94052,0.84388) rot=(0,0,1;3.14159rad)
FEATURE [Part::Feature] Part__Feature139  label="Part065"
  Placement = pos=(-1.10414,-6.80865,-2.54666) rot=(0,0,1;0rad)
  shape: bbox 0.15 x 0.3 x 0.33 mm, 6 faces (baked)
FEATURE [Part::Feature] Part__Feature140  label="Part066"
  Placement = pos=(-0.654141,-6.80865,-2.54666) rot=(0,0,1;0rad)
  shape: bbox 0.15 x 0.3 x 0.33 mm, 6 faces (baked)
FEATURE [Part::Feature] Part__Feature141  label="Part067"
  Placement = pos=(-0.879141,-6.80865,-2.54666) rot=(0,0,1;0rad)
  shape: bbox 0.3 x 0.3 x 0.33 mm, 6 faces (baked)
FEATURE [App::Part] C_0204  label="C 0204"
  Group = -> [Part__Feature139,Part__Feature140,Part__Feature141]
  Origin = -> Origin072
  Placement = pos=(-2.37388,14.5586,0.84388) rot=(0,0,1;0rad)
FEATURE [Part::Feature] Part__Feature142  label="Part068"
  Placement = pos=(-1.10414,-6.80865,-2.54666) rot=(0,0,1;0rad)
  shape: bbox 0.15 x 0.3 x 0.33 mm, 6 faces (baked)
FEATURE [Part::Feature] Part__Feature143  label="Part069"
  Placement = pos=(-0.654141,-6.80865,-2.54666) rot=(0,0,1;0rad)
  shape: bbox 0.15 x 0.3 x 0.33 mm, 6 faces (baked)
FEATURE [Part::Feature] Part__Feature144  label="Part070"
  Placement = pos=(-0.879141,-6.80865,-2.54666) rot=(0,0,1;0rad)
  shape: bbox 0.3 x 0.3 x 0.33 mm, 6 faces (baked)
FEATURE [App::Part] C_0205  label="C 0205"
  Group = -> [Part__Feature142,Part__Feature143,Part__Feature144]
  Origin = -> Origin073
  Placement = pos=(-7.46694,2.81803,0.84388) rot=(0,0,1;3.14159rad)
FEATURE [Part::Feature] Part__Feature145  label="Part071"
  Placement = pos=(-1.10414,-6.80865,-2.54666) rot=(0,0,1;0rad)
  shape: bbox 0.15 x 0.3 x 0.33 mm, 6 faces (baked)
FEATURE [Part::Feature] Part__Feature146  label="Part072"
  Placement = pos=(-0.654141,-6.80865,-2.54666) rot=(0,0,1;0rad)
  shape: bbox 0.15 x 0.3 x 0.33 mm, 6 faces (baked)
FEATURE [Part::Feature] Part__Feature147  label="Part073"
  Placement = pos=(-0.879141,-6.80865,-2.54666) rot=(0,0,1;0rad)
  shape: bbox 0.3 x 0.3 x 0.33 mm, 6 faces (baked)
FEATURE [App::Part] C_0206  label="C 0206"
  Group = -> [Part__Feature145,Part__Feature146,Part__Feature147]
  Origin = -> Origin074
  Placement = pos=(-7.69228,2.31135,0.84388) rot=(0,0,1;3.14159rad)
FEATURE [Part::Feature] Part__Feature148  label="Part074"
  Placement = pos=(-1.10414,-6.80865,-2.54666) rot=(0,0,1;0rad)
  shape: bbox 0.15 x 0.3 x 0.33 mm, 6 faces (baked)
FEATURE [Part::Feature] Part__Feature149  label="Part075"
  Placement = pos=(-0.654141,-6.80865,-2.54666) rot=(0,0,1;0rad)
  shape: bbox 0.15 x 0.3 x 0.33 mm, 6 faces (baked)
FEATURE [Part::Feature] Part__Feature150  label="Part076"
  Placement = pos=(-0.879141,-6.80865,-2.54666) rot=(0,0,1;0rad)
  shape: bbox 0.3 x 0.3 x 0.33 mm, 6 faces (baked)
FEATURE [App::Part] C_0207  label="C 0207"
  Group = -> [Part__Feature148,Part__Feature149,Part__Feature150]
  Origin = -> Origin075
  Placement = pos=(-7.73732,-0.182825,0.84388) rot=(0,0,1;3.14159rad)
FEATURE [Part::Feature] Part__Feature151  label="Part077"
  Placement = pos=(-1.10414,-6.80865,-2.54666) rot=(0,0,1;0rad)
  shape: bbox 0.15 x 0.3 x 0.33 mm, 6 faces (baked)
FEATURE [Part::Feature] Part__Feature152  label="Part078"
  Placement = pos=(-0.654141,-6.80865,-2.54666) rot=(0,0,1;0rad)
  shape: bbox 0.15 x 0.3 x 0.33 mm, 6 faces (baked)
FEATURE [Part::Feature] Part__Feature153  label="Part079"
  Placement = pos=(-0.879141,-6.80865,-2.54666) rot=(0,0,1;0rad)
  shape: bbox 0.3 x 0.3 x 0.33 mm, 6 faces (baked)
FEATURE [App::Part] C_0208  label="C 0208"
  Group = -> [Part__Feature151,Part__Feature152,Part__Feature153]
  Origin = -> Origin076
  Placement = pos=(-12.4448,4.02842,0.84388) rot=(0,0,1;3.14159rad)
FEATURE [Part::Feature] Part__Feature154  label="Part080"
  Placement = pos=(-1.10414,-6.80865,-2.54666) rot=(0,0,1;0rad)
  shape: bbox 0.15 x 0.3 x 0.33 mm, 6 faces (baked)
FEATURE [Part::Feature] Part__Feature155  label="Part081"
  Placement = pos=(-0.654141,-6.80865,-2.54666) rot=(0,0,1;0rad)
  shape: bbox 0.15 x 0.3 x 0.33 mm, 6 faces (baked)
FEATURE [Part::Feature] Part__Feature156  label="Part082"
  Placement = pos=(-0.879141,-6.80865,-2.54666) rot=(0,0,1;0rad)
  shape: bbox 0.3 x 0.3 x 0.33 mm, 6 faces (baked)
FEATURE [App::Part] C_0209  label="C 0209"
  Group = -> [Part__Feature154,Part__Feature155,Part__Feature156]
  Origin = -> Origin077
  Placement = pos=(-6.4332,2.83141,0.84388) rot=(0,0,1;3.14159rad)
FEATURE [Part::Feature] Part__Feature157  label="Part083"
  Placement = pos=(-1.10414,-6.80865,-2.54666) rot=(0,0,1;0rad)
  shape: bbox 0.15 x 0.3 x 0.33 mm, 6 faces (baked)
FEATURE [Part::Feature] Part__Feature158  label="Part084"
  Placement = pos=(-0.654141,-6.80865,-2.54666) rot=(0,0,1;0rad)
  shape: bbox 0.15 x 0.3 x 0.33 mm, 6 faces (baked)
FEATURE [Part::Feature] Part__Feature159  label="Part085"
  Placement = pos=(-0.879141,-6.80865,-2.54666) rot=(0,0,1;0rad)
  shape: bbox 0.3 x 0.3 x 0.33 mm, 6 faces (baked)
FEATURE [App::Part] C_0210  label="C 0210"
  Group = -> [Part__Feature157,Part__Feature158,Part__Feature159]
  Origin = -> Origin078
  Placement = pos=(1.86717,5.11122,0.84388) rot=(0,0,-1;1.5708rad)
FEATURE [Part::Feature] Part__Feature160  label="Part38"
  shape: bbox 0.6 x 0.5 x 0.5 mm, 6 faces (baked)
FEATURE [Part::Feature] Part__Feature161  label="Part39"
  shape: bbox 1 x 0.5 x 0.5 mm, 12 faces, 2 solids (baked)
FEATURE [App::Part] C0402
  Group = -> [Part__Feature160,Part__Feature161]
  Origin = -> Origin079
  Placement = pos=(-17.197,-14.0175,13.993) rot=(0,0,1;1.5708rad)
FEATURE [Part::Feature] Part__Feature162  label="Part086"
  Placement = pos=(-1.10414,-6.80865,-2.54666) rot=(0,0,1;0rad)
  shape: bbox 0.15 x 0.3 x 0.33 mm, 6 faces (baked)
FEATURE [Part::Feature] Part__Feature163  label="Part087"
  Placement = pos=(-0.654141,-6.80865,-2.54666) rot=(0,0,1;0rad)
  shape: bbox 0.15 x 0.3 x 0.33 mm, 6 faces (baked)
FEATURE [Part::Feature] Part__Feature164  label="Part088"
  Placement = pos=(-0.879141,-6.80865,-2.54666) rot=(0,0,1;0rad)
  shape: bbox 0.3 x 0.3 x 0.33 mm, 6 faces (baked)
FEATURE [App::Part] L_0201  label="L 0201"
  Group = -> [Part__Feature162,Part__Feature163,Part__Feature164]
  Origin = -> Origin080
  Placement = pos=(-0.554071,8.24143,0.84388) rot=(0,0,-1;1.5708rad)
FEATURE [Part::Feature] Part__Feature165  label="Part089"
  Placement = pos=(-1.10414,-6.80865,-2.54666) rot=(0,0,1;0rad)
  shape: bbox 0.15 x 0.3 x 0.33 mm, 6 faces (baked)
FEATURE [Part::Feature] Part__Feature166  label="Part090"
  Placement = pos=(-0.654141,-6.80865,-2.54666) rot=(0,0,1;0rad)
  shape: bbox 0.15 x 0.3 x 0.33 mm, 6 faces (baked)
FEATURE [Part::Feature] Part__Feature167  label="Part091"
  Placement = pos=(-0.879141,-6.80865,-2.54666) rot=(0,0,1;0rad)
  shape: bbox 0.3 x 0.3 x 0.33 mm, 6 faces (baked)
FEATURE [App::Part] C_0211  label="C 0211"
  Group = -> [Part__Feature165,Part__Feature166,Part__Feature167]
  Origin = -> Origin081
  Placement = pos=(-8.25428,3.73865,0.84388) rot=(0,0,1;3.14159rad)
FEATURE [Part::Feature] Part__Feature168  label="X2"
  Placement = pos=(-3.3463,-23.8977,-14.3401) rot=(0,0,1;1.5708rad)
  shape: bbox 1.6 x 2 x 0.8 mm, 27 faces (baked)
FEATURE [App::Part] _x1_6_Crystal  label="2x1.6 Crystal"
  Group = -> [Part__Feature168]
  Origin = -> Origin082
  Placement = pos=(-22.3165,11.2012,12.7123) rot=(0,0,1;1.5708rad)
FEATURE [Part::Feature] Part__Feature169  label="Pads"
  Placement = pos=(9.34912,7.35,-1.601) rot=(0,0,1;0rad)
  shape: bbox 3.15 x 9.4 x 0.011 mm, 24 faces, 4 solids (baked)
FEATURE [Part::Feature] Part__Feature170  label="LILY Antenna Rev D"
  Placement = pos=(5.39824,-2.597,0.656381) rot=(0.57735,-0.57735,0.57735;2.0944rad)
  shape: bbox 3.802 x 9.9 x 3.002 mm, 81 faces (baked)
FEATURE [App::Part] Antenna
  Group = -> [Part__Feature169,Part__Feature170]
  Origin = -> Origin083
  Placement = pos=(20.0317,-10.292,-10.1255) rot=(0,0,1;0rad)
FEATURE [App::Part] Antenna001
  Group = -> [Antenna]
  Origin = -> Origin084
  Placement = pos=(-12.695,-13.1317,12.5256) rot=(0,0,1;1.5708rad)
FEATURE [Part::Feature] Part__Feature171  label="Part092"
  shape: bbox 0.6 x 0.5 x 0.5 mm, 6 faces (baked)
FEATURE [Part::Feature] Part__Feature172  label="Part093"
  shape: bbox 1 x 0.5 x 0.5 mm, 12 faces, 2 solids (baked)
FEATURE [App::Part] C0403
  Group = -> [Part__Feature171,Part__Feature172]
  Origin = -> Origin085
  Placement = pos=(-16.275,-14.0348,13.993) rot=(0,0,1;1.5708rad)
FEATURE [Part::Feature] Part__Feature173  label="Part094"
  Placement = pos=(-1.10414,-6.80865,-2.54666) rot=(0,0,1;0rad)
  shape: bbox 0.15 x 0.3 x 0.33 mm, 6 faces (baked)
FEATURE [Part::Feature] Part__Feature174  label="Part095"
  Placement = pos=(-0.654141,-6.80865,-2.54666) rot=(0,0,1;0rad)
  shape: bbox 0.15 x 0.3 x 0.33 mm, 6 faces (baked)
FEATURE [Part::Feature] Part__Feature175  label="Part096"
  Placement = pos=(-0.879141,-6.80865,-2.54666) rot=(0,0,1;0rad)
  shape: bbox 0.3 x 0.3 x 0.33 mm, 6 faces (baked)
FEATURE [App::Part] C_0212  label="C 0212"
  Group = -> [Part__Feature173,Part__Feature174,Part__Feature175]
  Origin = -> Origin086
  Placement = pos=(-6.51288,-0.203908,0.84388) rot=(0,0,1;3.14159rad)
FEATURE [Part::Feature] Part__Feature176  label="Part097"
  Placement = pos=(-1.10414,-6.80865,-2.54666) rot=(0,0,1;0rad)
  shape: bbox 0.15 x 0.3 x 0.33 mm, 6 faces (baked)
FEATURE [Part::Feature] Part__Feature177  label="Part098"
  Placement = pos=(-0.654141,-6.80865,-2.54666) rot=(0,0,1;0rad)
  shape: bbox 0.15 x 0.3 x 0.33 mm, 6 faces (baked)
FEATURE [Part::Feature] Part__Feature178  label="Part099"
  Placement = pos=(-0.879141,-6.80865,-2.54666) rot=(0,0,1;0rad)
  shape: bbox 0.3 x 0.3 x 0.33 mm, 6 faces (baked)
FEATURE [App::Part] C_0213  label="C 0213"
  Group = -> [Part__Feature176,Part__Feature177,Part__Feature178]
  Origin = -> Origin087
  Placement = pos=(-9.07195,-3.2553,0.84388) rot=(0,0,1;3.14159rad)
FEATURE [Part::Feature] Part__Feature179  label="Part100"
  Placement = pos=(-1.10414,-6.80865,-2.54666) rot=(0,0,1;0rad)
  shape: bbox 0.15 x 0.3 x 0.33 mm, 6 faces (baked)
FEATURE [Part::Feature] Part__Feature180  label="Part101"
  Placement = pos=(-0.654141,-6.80865,-2.54666) rot=(0,0,1;0rad)
  shape: bbox 0.15 x 0.3 x 0.33 mm, 6 faces (baked)
FEATURE [Part::Feature] Part__Feature181  label="Part102"
  Placement = pos=(-0.879141,-6.80865,-2.54666) rot=(0,0,1;0rad)
  shape: bbox 0.3 x 0.3 x 0.33 mm, 6 faces (baked)
FEATURE [App::Part] C_0214  label="C 0214"
  Group = -> [Part__Feature179,Part__Feature180,Part__Feature181]
  Origin = -> Origin088
  Placement = pos=(4.48804,9.50069,0.84388) rot=(0,0,-1;1.0472rad)
FEATURE [Part::Feature] Part__Feature182  label="Part103"
  Placement = pos=(-1.10414,-6.80865,-2.54666) rot=(0,0,1;0rad)
  shape: bbox 0.15 x 0.3 x 0.33 mm, 6 faces (baked)
FEATURE [Part::Feature] Part__Feature183  label="Part104"
  Placement = pos=(-0.654141,-6.80865,-2.54666) rot=(0,0,1;0rad)
  shape: bbox 0.15 x 0.3 x 0.33 mm, 6 faces (baked)
FEATURE [Part::Feature] Part__Feature184  label="Part105"
  Placement = pos=(-0.879141,-6.80865,-2.54666) rot=(0,0,1;0rad)
  shape: bbox 0.3 x 0.3 x 0.33 mm, 6 faces (baked)
FEATURE [App::Part] C_0215  label="C 0215"
  Group = -> [Part__Feature182,Part__Feature183,Part__Feature184]
  Origin = -> Origin089
  Placement = pos=(-10.1504,-3.28729,0.84388) rot=(0,0,1;3.14159rad)
FEATURE [Part::Feature] Part__Feature185  label="Part106"
  Placement = pos=(-1.10414,-6.80865,-2.54666) rot=(0,0,1;0rad)
  shape: bbox 0.15 x 0.3 x 0.33 mm, 6 faces (baked)
FEATURE [Part::Feature] Part__Feature186  label="Part107"
  Placement = pos=(-0.654141,-6.80865,-2.54666) rot=(0,0,1;0rad)
  shape: bbox 0.15 x 0.3 x 0.33 mm, 6 faces (baked)
FEATURE [Part::Feature] Part__Feature187  label="Part108"
  Placement = pos=(-0.879141,-6.80865,-2.54666) rot=(0,0,1;0rad)
  shape: bbox 0.3 x 0.3 x 0.33 mm, 6 faces (baked)
FEATURE [App::Part] C_0216  label="C 0216"
  Group = -> [Part__Feature185,Part__Feature186,Part__Feature187]
  Origin = -> Origin090
  Placement = pos=(-12.444,-3.66035,0.84388) rot=(0,0,1;3.14159rad)
FEATURE [Part::Feature] Part__Feature188  label="Part109"
  Placement = pos=(-1.10414,-6.80865,-2.54666) rot=(0,0,1;0rad)
  shape: bbox 0.15 x 0.3 x 0.33 mm, 6 faces (baked)
FEATURE [Part::Feature] Part__Feature189  label="Part110"
  Placement = pos=(-0.654141,-6.80865,-2.54666) rot=(0,0,1;0rad)
  shape: bbox 0.15 x 0.3 x 0.33 mm, 6 faces (baked)
FEATURE [Part::Feature] Part__Feature190  label="Part111"
  Placement = pos=(-0.879141,-6.80865,-2.54666) rot=(0,0,1;0rad)
  shape: bbox 0.3 x 0.3 x 0.33 mm, 6 faces (baked)
FEATURE [App::Part] C_0217  label="C 0217"
  Group = -> [Part__Feature188,Part__Feature189,Part__Feature190]
  Origin = -> Origin091
  Placement = pos=(3.43652,5.1337,0.84388) rot=(0,0,-1;1.5708rad)
FEATURE [Part::Feature] Part__Feature191  label="Part112"
  Placement = pos=(-1.10414,-6.80865,-2.54666) rot=(0,0,1;0rad)
  shape: bbox 0.15 x 0.3 x 0.33 mm, 6 faces (baked)
FEATURE [Part::Feature] Part__Feature192  label="Part113"
  Placement = pos=(-0.654141,-6.80865,-2.54666) rot=(0,0,1;0rad)
  shape: bbox 0.15 x 0.3 x 0.33 mm, 6 faces (baked)
FEATURE [Part::Feature] Part__Feature193  label="Part114"
  Placement = pos=(-0.879141,-6.80865,-2.54666) rot=(0,0,1;0rad)
  shape: bbox 0.3 x 0.3 x 0.33 mm, 6 faces (baked)
FEATURE [App::Part] C_0218  label="C 0218"
  Group = -> [Part__Feature191,Part__Feature192,Part__Feature193]
  Origin = -> Origin092
  Placement = pos=(-8.23665,4.24066,0.84388) rot=(0,0,1;3.14159rad)
FEATURE [Part::Feature] Part__Feature194  label="Part115"
  Placement = pos=(-1.10414,-6.80865,-2.54666) rot=(0,0,1;0rad)
  shape: bbox 0.15 x 0.3 x 0.33 mm, 6 faces (baked)
FEATURE [Part::Feature] Part__Feature195  label="Part116"
  Placement = pos=(-0.654141,-6.80865,-2.54666) rot=(0,0,1;0rad)
  shape: bbox 0.15 x 0.3 x 0.33 mm, 6 faces (baked)
FEATURE [Part::Feature] Part__Feature196  label="Part117"
  Placement = pos=(-0.879141,-6.80865,-2.54666) rot=(0,0,1;0rad)
  shape: bbox 0.3 x 0.3 x 0.33 mm, 6 faces (baked)
FEATURE [App::Part] C_0219  label="C 0219"
  Group = -> [Part__Feature194,Part__Feature195,Part__Feature196]
  Origin = -> Origin093
  Placement = pos=(-8.23665,4.75189,0.84388) rot=(0,0,1;3.14159rad)
FEATURE [Part::Feature] Part__Feature197  label="Part118"
  Placement = pos=(-1.10414,-6.80865,-2.54666) rot=(0,0,1;0rad)
  shape: bbox 0.15 x 0.3 x 0.33 mm, 6 faces (baked)
FEATURE [Part::Feature] Part__Feature198  label="Part119"
  Placement = pos=(-0.654141,-6.80865,-2.54666) rot=(0,0,1;0rad)
  shape: bbox 0.15 x 0.3 x 0.33 mm, 6 faces (baked)
FEATURE [Part::Feature] Part__Feature199  label="Part120"
  Placement = pos=(-0.879141,-6.80865,-2.54666) rot=(0,0,1;0rad)
  shape: bbox 0.3 x 0.3 x 0.33 mm, 6 faces (baked)
FEATURE [App::Part] C_0220  label="C 0220"
  Group = -> [Part__Feature197,Part__Feature198,Part__Feature199]
  Origin = -> Origin094
  Placement = pos=(-2.24002,5.14739,0.84388) rot=(0,0,-1;1.5708rad)
FEATURE [Part::Feature] Part__Feature200  label="Part121"
  Placement = pos=(-1.10414,-6.80865,-2.54666) rot=(0,0,1;0rad)
  shape: bbox 0.15 x 0.3 x 0.33 mm, 6 faces (baked)
FEATURE [Part::Feature] Part__Feature201  label="Part122"
  Placement = pos=(-0.654141,-6.80865,-2.54666) rot=(0,0,1;0rad)
  shape: bbox 0.15 x 0.3 x 0.33 mm, 6 faces (baked)
FEATURE [Part::Feature] Part__Feature202  label="Part123"
  Placement = pos=(-0.879141,-6.80865,-2.54666) rot=(0,0,1;0rad)
  shape: bbox 0.3 x 0.3 x 0.33 mm, 6 faces (baked)
FEATURE [App::Part] C_0221  label="C 0221"
  Group = -> [Part__Feature200,Part__Feature201,Part__Feature202]
  Origin = -> Origin095
  Placement = pos=(-13.9838,4.07709,0.84388) rot=(0,0,1;3.14159rad)
FEATURE [Part::Feature] Part__Feature203  label="Part124"
  Placement = pos=(-1.10414,-6.80865,-2.54666) rot=(0,0,1;0rad)
  shape: bbox 0.15 x 0.3 x 0.33 mm, 6 faces (baked)
FEATURE [Part::Feature] Part__Feature204  label="Part125"
  Placement = pos=(-0.654141,-6.80865,-2.54666) rot=(0,0,1;0rad)
  shape: bbox 0.15 x 0.3 x 0.33 mm, 6 faces (baked)
FEATURE [Part::Feature] Part__Feature205  label="Part126"
  Placement = pos=(-0.879141,-6.80865,-2.54666) rot=(0,0,1;0rad)
  shape: bbox 0.3 x 0.3 x 0.33 mm, 6 faces (baked)
FEATURE [App::Part] C_0222  label="C 0222"
  Group = -> [Part__Feature203,Part__Feature204,Part__Feature205]
  Origin = -> Origin096
  Placement = pos=(-13.2729,7.90257,0.84388) rot=(0,0,1;3.14159rad)
FEATURE [Part::Feature] Part__Feature206  label="Part127"
  Placement = pos=(-1.10414,-6.80865,-2.54666) rot=(0,0,1;0rad)
  shape: bbox 0.15 x 0.3 x 0.33 mm, 6 faces (baked)
FEATURE [Part::Feature] Part__Feature207  label="Part128"
  Placement = pos=(-0.654141,-6.80865,-2.54666) rot=(0,0,1;0rad)
  shape: bbox 0.15 x 0.3 x 0.33 mm, 6 faces (baked)
FEATURE [Part::Feature] Part__Feature208  label="Part129"
  Placement = pos=(-0.879141,-6.80865,-2.54666) rot=(0,0,1;0rad)
  shape: bbox 0.3 x 0.3 x 0.33 mm, 6 faces (baked)
FEATURE [App::Part] C_0223  label="C 0223"
  Group = -> [Part__Feature206,Part__Feature207,Part__Feature208]
  Origin = -> Origin097
  Placement = pos=(-12.7654,6.30543,0.84388) rot=(0,0,1;3.14159rad)
FEATURE [Part::Feature] Part__Feature209  label="Part130"
  Placement = pos=(-1.10414,-6.80865,-2.54666) rot=(0,0,1;0rad)
  shape: bbox 0.15 x 0.3 x 0.33 mm, 6 faces (baked)
FEATURE [Part::Feature] Part__Feature210  label="Part131"
  Placement = pos=(-0.654141,-6.80865,-2.54666) rot=(0,0,1;0rad)
  shape: bbox 0.15 x 0.3 x 0.33 mm, 6 faces (baked)
FEATURE [Part::Feature] Part__Feature211  label="Part132"
  Placement = pos=(-0.879141,-6.80865,-2.54666) rot=(0,0,1;0rad)
  shape: bbox 0.3 x 0.3 x 0.33 mm, 6 faces (baked)
FEATURE [App::Part] C_0224  label="C 0224"
  Group = -> [Part__Feature209,Part__Feature210,Part__Feature211]
  Origin = -> Origin098
  Placement = pos=(-6.41238,2.31135,0.84388) rot=(0,0,1;3.14159rad)
FEATURE [Part::Feature] Part__Feature212  label="Part133"
  Placement = pos=(-1.10414,-6.80865,-2.54666) rot=(0,0,1;0rad)
  shape: bbox 0.15 x 0.3 x 0.33 mm, 6 faces (baked)
FEATURE [Part::Feature] Part__Feature213  label="Part134"
  Placement = pos=(-0.654141,-6.80865,-2.54666) rot=(0,0,1;0rad)
  shape: bbox 0.15 x 0.3 x 0.33 mm, 6 faces (baked)
FEATURE [Part::Feature] Part__Feature214  label="Part135"
  Placement = pos=(-0.879141,-6.80865,-2.54666) rot=(0,0,1;0rad)
  shape: bbox 0.3 x 0.3 x 0.33 mm, 6 faces (baked)
FEATURE [App::Part] C_0225  label="C 0225"
  Group = -> [Part__Feature212,Part__Feature213,Part__Feature214]
  Origin = -> Origin099
  Placement = pos=(-13.4395,-3.2553,0.84388) rot=(0,0,1;3.14159rad)
FEATURE [Part::Feature] Part__Feature215  label="Part136"
  Placement = pos=(-1.10414,-6.80865,-2.54666) rot=(0,0,1;0rad)
  shape: bbox 0.15 x 0.3 x 0.33 mm, 6 faces (baked)
FEATURE [Part::Feature] Part__Feature216  label="Part137"
  Placement = pos=(-0.654141,-6.80865,-2.54666) rot=(0,0,1;0rad)
  shape: bbox 0.15 x 0.3 x 0.33 mm, 6 faces (baked)
FEATURE [Part::Feature] Part__Feature217  label="Part138"
  Placement = pos=(-0.879141,-6.80865,-2.54666) rot=(0,0,1;0rad)
  shape: bbox 0.3 x 0.3 x 0.33 mm, 6 faces (baked)
FEATURE [App::Part] C_0226  label="C 0226"
  Group = -> [Part__Feature215,Part__Feature216,Part__Feature217]
  Origin = -> Origin100
  Placement = pos=(-13.9601,4.62472,0.84388) rot=(0,0,1;3.14159rad)
FEATURE [App::Part] NINA_W132_00B  label="NINA-W132-00B"
  Group = -> [_4x10_0_PCB,NINA_pads,Shieldbox,Flash,ESP32,C_0201,C_0202,C_0203,C_0204,C_0205,C_0206,C_0207,C_0208,C_0209,C_0210,C0402,L_0201,C_0211,_x1_6_Crystal,Antenna001,C0403,C_0212,C_0213,C_0214,C_0215,C_0216,C_0217,C_0218,C_0219,C_0220,C_0221,C_0222,C_0223,C_0224,C_0225,C_0226]
  Origin = -> Origin101
  Placement = pos=(27.0391,4.17556,0) rot=(0,0,-1;1.5708rad)
FEATURE [App::Part] U2
  Group = -> [NINA_W132_00B]
  Origin = -> Origin102
FEATURE [Part::Feature] Part__Feature218  label="Extruded002"
  shape: bbox 7 x 7 x 0.89 mm, 6 faces (baked)
FEATURE [App::Part] _138194256  label="7138194256"
  Group = -> [Part__Feature218]
  Origin = -> Origin103
  Placement = pos=(22.8043,10.1665,0.00999997) rot=(0,0,1;0rad)
FEATURE [App::Part] U1
  Group = -> [_138194256]
  Origin = -> Origin104
FEATURE [Part::Feature] Part__Feature219  label="RES-0221"
  Placement = pos=(35.6443,14.6393,0) rot=(0,0,1;3.14159rad)
  shape: bbox 0.6 x 0.3 x 0.2375 mm, 36 faces (baked)
FEATURE [App::Part] R7
  Group = -> [Part__Feature219]
  Origin = -> Origin105
FEATURE [Part::Feature] Part__Feature220  label="FER-0603"
  Placement = pos=(18.5137,5.17332,0) rot=(0,0,-1;1.5708rad)
  shape: bbox 0.8 x 1.6 x 0.8 mm, 58 faces (baked)
FEATURE [App::Part] L1
  Group = -> [Part__Feature220]
  Origin = -> Origin106
FEATURE [Part::Feature] Part__Feature221  label="U_FL-R-SMT(10)"
  Placement = pos=(41.6944,8.88136,0) rot=(0,0,1;1.5708rad)
  shape: bbox 3.3 x 3.2 x 1.45 mm, 79 faces (baked)
FEATURE [App::Part] J2
  Group = -> [Part__Feature221]
  Origin = -> Origin107
FEATURE [Part::Feature] Part__Feature222  label="CAP-0214"
  Placement = pos=(36.8883,3.44244,0) rot=(0,0,1;3.14159rad)
  shape: bbox 0.6 x 0.3076 x 0.3076 mm, 58 faces (baked)
FEATURE [App::Part] C15
  Group = -> [Part__Feature222]
  Origin = -> Origin108
FEATURE [Part::Feature] Part__Feature223  label="CAP-0215"
  Placement = pos=(29.2639,14.6024,0) rot=(0,0,0.991678;0rad)
  shape: bbox 0.6 x 0.3076 x 0.3076 mm, 58 faces (baked)
FEATURE [App::Part] C14
  Group = -> [Part__Feature223]
  Origin = -> Origin109
FEATURE [Part::Feature] Part__Feature224  label="CAP-0216"
  Placement = pos=(27.2993,7.12242,0) rot=(0,0,-1;1.5708rad)
  shape: bbox 0.3076 x 0.6 x 0.3076 mm, 58 faces (baked)
FEATURE [App::Part] C12
  Group = -> [Part__Feature224]
  Origin = -> Origin110
FEATURE [Part::Feature] Part__Feature225  label="CAP-0217"
  Placement = pos=(22.7338,14.6912,0) rot=(0,0,1;1.5708rad)
  shape: bbox 0.3076 x 0.6 x 0.3076 mm, 58 faces (baked)
FEATURE [App::Part] C11
  Group = -> [Part__Feature225]
  Origin = -> Origin111
FEATURE [Part::Feature] Part__Feature226  label="CAP-0218"
  Placement = pos=(22.1338,14.6912,0) rot=(0,0,1;1.5708rad)
  shape: bbox 0.3076 x 0.6 x 0.3076 mm, 58 faces (baked)
FEATURE [App::Part] C10
  Group = -> [Part__Feature226]
  Origin = -> Origin112
FEATURE [Part::Feature] Part__Feature227  label="CAP-0603"
  Placement = pos=(17.9848,3.35543,0) rot=(0,0,1;3.14159rad)
  shape: bbox 1.6 x 0.8 x 0.8 mm, 58 faces (baked)
FEATURE [App::Part] C9
  Group = -> [Part__Feature227]
  Origin = -> Origin113
FEATURE [Part::Feature] Part__Feature228  label="CAP-0604"
  Placement = pos=(19.3796,5.45742,0) rot=(0,0,-1;1.5708rad)
  shape: bbox 0.3076 x 0.6 x 0.3076 mm, 58 faces (baked)
FEATURE [App::Part] C8
  Group = -> [Part__Feature228]
  Origin = -> Origin114
FEATURE [Part::Feature] Part__Feature229  label="CAP-0605"
  Placement = pos=(27.4912,11.3793,0) rot=(0,0,1;1.5708rad)
  shape: bbox 0.3076 x 0.6 x 0.3076 mm, 58 faces (baked)
FEATURE [App::Part] C7
  Group = -> [Part__Feature229]
  Origin = -> Origin115
FEATURE [Part::Feature] Part__Feature230  label="CAP-0402"
  Placement = pos=(39.8393,3.33045,0) rot=(0,0,0.991678;0rad)
  shape: bbox 1 x 0.5 x 0.5 mm, 58 faces (baked)
FEATURE [App::Part] C25
  Group = -> [Part__Feature230]
  Origin = -> Origin116
FEATURE [Part::Feature] Part__Feature231  label="RES-0222"
  Placement = pos=(8.30421,8.46644,0) rot=(0,0,1;1.5708rad)
  shape: bbox 0.3 x 0.6 x 0.2375 mm, 36 faces (baked)
FEATURE [App::Part] R5
  Group = -> [Part__Feature231]
  Origin = -> Origin117
FEATURE [Part::Feature] Part__Feature232  label="CAP-0606"
  Placement = pos=(10.7077,4.57802,0) rot=(0,0,-1;1.5708rad)
  shape: bbox 0.8 x 1.6 x 0.8 mm, 58 faces (baked)
FEATURE [App::Part] C23
  Group = -> [Part__Feature232]
  Origin = -> Origin118
FEATURE [Part::Feature] Part__Feature233  label="Open CASCADE STEP translator 6.8 19.1"
  Placement = pos=(-0.8,-1.05,0) rot=(0,0,1;0rad)
  shape: bbox 0.2 x 0.2 x 2e-07 mm, 1 faces, 0 solids (baked)
FEATURE [Part::Feature] Part__Feature234  label="Open CASCADE STEP translator 6.8 19.2.1"
  shape: bbox 1.6 x 2.1 x 0.9 mm, 8 faces (baked)
FEATURE [App::Part] Body005
  Group = -> [Part__Feature234]
  Origin = -> Origin119
  Placement = pos=(-0.8,-1.05,0) rot=(0,0,1;0rad)
FEATURE [Part::Feature] Part__Feature235  label="Open CASCADE STEP translator 6.8 19.3.1"
  shape: bbox 0.351 x 0.25 x 0.2 mm, 14 faces (baked)
FEATURE [App::Part] Pin_Shape008
  Group = -> [Part__Feature235]
  Origin = -> Origin120
  Placement = pos=(-0.8,-0.875,0) rot=(0,0,1;0rad)
FEATURE [Part::Feature] Part__Feature236  label="Open CASCADE STEP translator 6.8 19.3.002"
  shape: bbox 0.351 x 0.25 x 0.2 mm, 14 faces (baked)
FEATURE [App::Part] Pin_Shape009
  Group = -> [Part__Feature236]
  Origin = -> Origin121
  Placement = pos=(0.8,0.875,0) rot=(0,0,1;3.14159rad)
FEATURE [Part::Feature] Part__Feature237  label="Open CASCADE STEP translator 6.8 19.3.003"
  shape: bbox 0.351 x 0.25 x 0.2 mm, 14 faces (baked)
FEATURE [App::Part] Pin_Shape010
  Group = -> [Part__Feature237]
  Origin = -> Origin122
  Placement = pos=(-0.8,-0.375,0) rot=(0,0,1;0rad)
FEATURE [Part::Feature] Part__Feature238  label="Open CASCADE STEP translator 6.8 19.3.004"
  shape: bbox 0.351 x 0.25 x 0.2 mm, 14 faces (baked)
FEATURE [App::Part] Pin_Shape011
  Group = -> [Part__Feature238]
  Origin = -> Origin123
  Placement = pos=(0.8,0.375,0) rot=(0,0,1;3.14159rad)
FEATURE [Part::Feature] Part__Feature239  label="Open CASCADE STEP translator 6.8 19.3.005"
  shape: bbox 0.351 x 0.25 x 0.2 mm, 14 faces (baked)
FEATURE [App::Part] Pin_Shape012
  Group = -> [Part__Feature239]
  Origin = -> Origin124
  Placement = pos=(-0.8,0.125,0) rot=(0,0,1;0rad)
FEATURE [Part::Feature] Part__Feature240  label="Open CASCADE STEP translator 6.8 19.3.006"
  shape: bbox 0.351 x 0.25 x 0.2 mm, 14 faces (baked)
FEATURE [App::Part] Pin_Shape013
  Group = -> [Part__Feature240]
  Origin = -> Origin125
  Placement = pos=(0.8,-0.125,0) rot=(0,0,1;3.14159rad)
FEATURE [Part::Feature] Part__Feature241  label="Open CASCADE STEP translator 6.8 19.3.007"
  shape: bbox 0.351 x 0.25 x 0.2 mm, 14 faces (baked)
FEATURE [App::Part] Pin_Shape014
  Group = -> [Part__Feature241]
  Origin = -> Origin126
  Placement = pos=(-0.8,0.625,0) rot=(0,0,1;0rad)
FEATURE [Part::Feature] Part__Feature242  label="Open CASCADE STEP translator 6.8 19.3.008"
  shape: bbox 0.351 x 0.25 x 0.2 mm, 14 faces (baked)
FEATURE [App::Part] Pin_Shape015
  Group = -> [Part__Feature242]
  Origin = -> Origin127
  Placement = pos=(0.8,-0.625,0) rot=(0,0,1;3.14159rad)
FEATURE [App::Part] _211592816  label="7211592816"
  Group = -> [Part__Feature233,Body005,Pin_Shape008,Pin_Shape009,Pin_Shape010,Pin_Shape011,Pin_Shape012,Pin_Shape013,Pin_Shape014,Pin_Shape015]
  Origin = -> Origin128
  Placement = pos=(13.8877,4.70129,0) rot=(0,0,0.991678;0rad)
FEATURE [App::Part] U6
  Group = -> [_211592816]
  Origin = -> Origin129
FEATURE [Part::Feature] Part__Feature243  label="Extruded003"
  shape: bbox 1.6 x 2 x 1 mm, 6 faces (baked)
FEATURE [App::Part] _138192816  label="7138192816"
  Group = -> [Part__Feature243]
  Origin = -> Origin130
  Placement = pos=(16.7185,5.81413,0) rot=(0,0,1;0rad)
FEATURE [App::Part] L2
  Group = -> [_138192816]
  Origin = -> Origin131
FEATURE [Part::Feature] Part__Feature244  label="CAP-0607"
  Placement = pos=(13.2251,3.15956,0) rot=(0,0,1;3.14159rad)
  shape: bbox 0.6 x 0.3076 x 0.3076 mm, 58 faces (baked)
FEATURE [App::Part] C22
  Group = -> [Part__Feature244]
  Origin = -> Origin132
FEATURE [Part::Feature] Part__Feature245  label="CAP-0608"
  Placement = pos=(15.7796,3.1761,0) rot=(0,0,0.991678;0rad)
  shape: bbox 1 x 0.5 x 0.5 mm, 58 faces (baked)
FEATURE [App::Part] C20
  Group = -> [Part__Feature245]
  Origin = -> Origin133
FEATURE [Part::Feature] Part__Feature246  label="CAP-0609"
  Placement = pos=(15.3577,5.18627,0) rot=(0,0,-1;1.5708rad)
  shape: bbox 0.3076 x 0.6 x 0.3076 mm, 58 faces (baked)
FEATURE [App::Part] C19
  Group = -> [Part__Feature246]
  Origin = -> Origin134
FEATURE [Part::Feature] Part__Feature247  label="CAP-0610"
  Placement = pos=(14.1362,7.23108,0) rot=(0,0,0.991678;0rad)
  shape: bbox 1 x 0.5 x 0.5 mm, 58 faces (baked)
FEATURE [App::Part] C17
  Group = -> [Part__Feature247]
  Origin = -> Origin135
FEATURE [Part::Feature] Part__Feature248  label="CAP-0611"
  Placement = pos=(14.1362,6.33108,0) rot=(0,0,0.991678;0rad)
  shape: bbox 1 x 0.5 x 0.5 mm, 58 faces (baked)
FEATURE [App::Part] C3
  Group = -> [Part__Feature248]
  Origin = -> Origin136
FEATURE [Part::Feature] Part__Feature249  label="PTS820J20KSMTRLFS"
  Placement = pos=(10.7943,8.93339,0) rot=(0,0,1;1.5708rad)
  shape: bbox 2.9 x 4.5 x 2.005 mm, 253 faces (baked)
FEATURE [App::Part] PB1
  Group = -> [Part__Feature249]
  Origin = -> Origin137
FEATURE [Part::Feature] Part__Feature250  label="CAP-0612"
  Placement = pos=(12.0577,4.57802,0) rot=(0,0,-1;1.5708rad)
  shape: bbox 0.8 x 1.6 x 0.8 mm, 58 faces (baked)
FEATURE [App::Part] C4
  Group = -> [Part__Feature250]
  Origin = -> Origin138
FEATURE [Part::Feature] Part__Feature251  label="RES-0223"
  Placement = pos=(14.3773,3.14883,0) rot=(0,0,0.991678;0rad)
  shape: bbox 0.6 x 0.3 x 0.2375 mm, 36 faces (baked)
FEATURE [App::Part] R8
  Group = -> [Part__Feature251]
  Origin = -> Origin139
FEATURE [Part::Feature] Part__Feature252  label="RES-0224"
  Placement = pos=(15.3577,4.1094,0) rot=(0,0,1;1.5708rad)
  shape: bbox 0.3 x 0.6 x 0.2375 mm, 36 faces (baked)
FEATURE [App::Part] R6
  Group = -> [Part__Feature252]
  Origin = -> Origin140
FEATURE [Part::Feature] Part__Feature253  label="SOD123"
  Placement = pos=(7.65942,3.78654,0) rot=(1,0,0;1.5708rad)
  shape: bbox 3.7 x 1.6 x 1.27 mm, 39 faces (baked)
FEATURE [App::Part] D2
  Group = -> [Part__Feature253]
  Origin = -> Origin141
FEATURE [Part::Feature] Part__Feature254  label="Header _Fem_1X010"
  Placement = pos=(30.3323,1.26144,0) rot=(0,0.707107,0.707107;3.14159rad)
  shape: bbox 20.82 x 2.54 x 11.7 mm, 134 faces (baked)
FEATURE [Part::Feature] Part__Feature255  label="Header _Fem_1X011"
  Placement = pos=(12.6832,1.26138,0) rot=(1,0,0;1.5708rad)
  shape: bbox 20.82 x 2.54 x 11.7 mm, 134 faces (baked)
FEATURE [App::Part] JP2
  Group = -> [Part__Feature254,Part__Feature255]
  Origin = -> Origin142
FEATURE [Part::Feature] Part__Feature256  label="RES-0402"
  Placement = pos=(5.20131,6.21445,0) rot=(0,0,-1;1.5708rad)
  shape: bbox 0.5 x 1 x 0.3375 mm, 36 faces (baked)
FEATURE [App::Part] R1
  Group = -> [Part__Feature256]
  Origin = -> Origin143
FEATURE [Part::Feature] Part__Feature257  label="CAP-0805"
  Placement = pos=(7.36024,5.70635,0) rot=(0,0,1;3.14159rad)
  shape: bbox 2 x 1.25 x 1.25 mm, 58 faces (baked)
FEATURE [App::Part] C1
  Group = -> [Part__Feature257]
  Origin = -> Origin144
FEATURE [Part::Feature] Part__Feature258  label="RES-0403"
  Placement = pos=(8.30429,9.91644,0) rot=(0,0,-1;1.5708rad)
  shape: bbox 0.3 x 0.6 x 0.2375 mm, 36 faces (baked)
FEATURE [App::Part] R4
  Group = -> [Part__Feature258]
  Origin = -> Origin145
FEATURE [Part::Feature] Part__Feature259  label="CAP-0806"
  Placement = pos=(8.57251,11.2264,0) rot=(0,0,1;3.14159rad)
  shape: bbox 0.6 x 0.3076 x 0.3076 mm, 58 faces (baked)
FEATURE [App::Part] C2
  Group = -> [Part__Feature259]
  Origin = -> Origin146
FEATURE [Part::Feature] Part__Feature260  label="PRTR5V0U2X"
  Placement = pos=(6.19246,9.12641,0) rot=(0,0,0.991678;0rad)
  shape: bbox 2.899 x 2.308 x 0.9999 mm, 126 faces (baked)
FEATURE [App::Part] D1
  Group = -> [Part__Feature260]
  Origin = -> Origin147
FEATURE [Part::Feature] Part__Feature261  label="ZX62-AB-5PA(31)"
  Placement = pos=(1.27424,8.88148,0) rot=(0,0,1;1.5708rad)
  shape: bbox 5.6 x 8.817 x 2.95 mm, 543 faces (baked)
FEATURE [App::Part] J1
  Group = -> [Part__Feature261]
  Origin = -> Origin148
FEATURE [App::Part] PCB001  label="Arduino_Nano_RP2040"
  Group = -> [Board,C16,R16,RPAD,C30,C32,C27,R10,R9,R23,R12,C6,C5,SJ2,R28,R25,DL2,R22,R20,R19,R18,C33,C24,C13,R17,R3,Q1,R2,DL1,C28,U9,U8,JP3,U7,R15,R14,R13,DL3,U5,R11,C26,C21,C18,U4,U2,U1,R7,L1,J2,C15,C14,C12,C11,C10,C9,C8,C7,C25,R5,C23,U6,L2,C22,C20,C19,C17,C3,PB1,C4,R8,R6,D2,JP2,R1,C1,R4,C2,D1,J1]
  Origin = -> Origin149
  Placement = pos=(-69.5,14.5,1.25) rot=(0,1,0;4.71239rad)
FEATURE [Part::Feature] Part__Feature262  label="DC Barrel Plug v4"
  Placement = pos=(-66.5,38,-72.5) rot=(-0.57735,0.57735,0.57735;4.18879rad)
  shape: bbox 12.82 x 34.73 x 14.5 mm, 71 faces, 3 solids (baked)
FEATURE [Sketcher::SketchObject] Sketch018
  ArcFitTolerance = 1e-06
  AttachmentSupport = -> [Pocket009]
  ExternalGeometry = -> [Pocket009]
  FullyConstrained = true
  MakeInternals = false
  MapMode = 5
  Placement = pos=(-66,0,0) rot=(0.57735,0.57735,-0.57735;4.18879rad)
  expr: Constraints[5] = 35 / 2
  sketch-geometry (3):
    g0: Circle CenterX=-30 CenterY=8 CenterZ=0 NormalX=0 NormalY=0 NormalZ=1 AngleXU=0 Radius=2
    g1: Circle CenterX=5 CenterY=8 CenterZ=0 NormalX=0 NormalY=0 NormalZ=1 AngleXU=0 Radius=2
    g2: LineSegment [constr] StartX=-30 StartY=8 StartZ=0 EndX=5 EndY=8 EndZ=0
  constraints (8):
    c: Coincident(g2,g0)
    c: Coincident(g2,g1)
    c: Horizontal(g2)
    c: DistanceX(g2,g2) = 35
    c: DistanceY(g-3,g1) = 8
    c: DistanceX(g-3,g1) = 17.5
    c: Equal(g0,g1)
    c: Diameter(g0) = 4
FEATURE [PartDesign::Pocket] Pocket010  label="Motor_fix"
  BaseFeature = -> Pocket009
  Direction = (1,0,0)
  Length = 6.74
  Length2 = 5
  Placement = pos=(0,0,0) rot=(1,1,1;2.0944rad)
  Profile = -> Sketch018
  ReferenceAxis = -> Sketch018 [N_Axis]
  Refine = true
  Suppressed = false
  Type = 0
FEATURE [Sketcher::SketchObject] Sketch019
  ArcFitTolerance = 1e-06
  AttachmentSupport = -> [Pocket010]
  ExternalGeometry = -> [Pocket010]
  FullyConstrained = true
  MakeInternals = false
  MapMode = 5
  Placement = pos=(-66,0,0) rot=(0.57735,0.57735,-0.57735;4.18879rad)
  expr: Constraints[45] = 35 / 2
  expr: Constraints[46] = 18 / 2
  expr: Constraints[47] = 44 / 2
  expr: Constraints[54] = 17 / 2
  expr: Constraints[55] = (22 - 10) / 2
  sketch-geometry (23):
    g0: LineSegment [constr] StartX=-54.6 StartY=-42.3 StartZ=0 EndX=-28 EndY=-42.3 EndZ=0
    g1: LineSegment [constr] StartX=-28 StartY=-42.3 StartZ=0 EndX=-28 EndY=-12.7 EndZ=0
    g2: LineSegment [constr] StartX=-28 StartY=-12.7 StartZ=0 EndX=-54.6 EndY=-12.7 EndZ=0
    g3: LineSegment [constr] StartX=-54.6 StartY=-12.7 StartZ=0 EndX=-54.6 EndY=-42.3 EndZ=0
    g4: LineSegment [constr] StartX=-41.3 StartY=-12.7 StartZ=0 EndX=-41.3 EndY=-42.3 EndZ=0
    g5: LineSegment [constr] StartX=-54.6 StartY=-27.5 StartZ=0 EndX=-28 EndY=-27.5 EndZ=0
    g6: Circle CenterX=-54.6 CenterY=-12.7 CenterZ=0 NormalX=0 NormalY=0 NormalZ=1 AngleXU=0 Radius=2
    g7: Circle CenterX=-28 CenterY=-12.7 CenterZ=0 NormalX=0 NormalY=0 NormalZ=1 AngleXU=0 Radius=2
    g8: Circle CenterX=-28 CenterY=-42.3 CenterZ=0 NormalX=0 NormalY=0 NormalZ=1 AngleXU=0 Radius=2
    g9: Circle CenterX=-54.6 CenterY=-42.3 CenterZ=0 NormalX=0 NormalY=0 NormalZ=1 AngleXU=0 Radius=2
    g10: Circle CenterX=15.88 CenterY=-43.32 CenterZ=0 NormalX=0 NormalY=0 NormalZ=1 AngleXU=0 Radius=1.125
    g11: LineSegment [constr] StartX=15.88 StartY=-43.32 StartZ=0 EndX=31.12 EndY=-43.32 EndZ=0
    g12: LineSegment [constr] StartX=31.12 StartY=-43.32 StartZ=0 EndX=31.12 EndY=-2.68 EndZ=0
    g13: LineSegment [constr] StartX=31.12 StartY=-2.68 StartZ=0 EndX=15.88 EndY=-2.68 EndZ=0
    g14: LineSegment [constr] StartX=15.88 StartY=-2.68 StartZ=0 EndX=15.88 EndY=-43.32 EndZ=0
    g15: LineSegment [constr] StartX=23.5 StartY=-2.68 StartZ=0 EndX=23.5 EndY=-43.32 EndZ=0
    g16: LineSegment [constr] StartX=15.88 StartY=-23 StartZ=0 EndX=31.12 EndY=-23 EndZ=0
    g17: Circle CenterX=15.88 CenterY=-2.68 CenterZ=0 NormalX=0 NormalY=0 NormalZ=1 AngleXU=0 Radius=1.125
    g18: Circle CenterX=31.12 CenterY=-2.68 CenterZ=0 NormalX=0 NormalY=0 NormalZ=1 AngleXU=0 Radius=1.125
    g19: Circle CenterX=31.12 CenterY=-43.32 CenterZ=0 NormalX=0 NormalY=0 NormalZ=1 AngleXU=0 Radius=1.125
    g20: Circle CenterX=-49 CenterY=39 CenterZ=0 NormalX=0 NormalY=0 NormalZ=1 AngleXU=0 Radius=2
    g21: Circle CenterX=-49 CenterY=29 CenterZ=0 NormalX=0 NormalY=0 NormalZ=1 AngleXU=0 Radius=2
    g22: LineSegment [constr] StartX=-49 StartY=39 StartZ=0 EndX=-49 EndY=29 EndZ=0
  constraints (56):
    c: Coincident(g0,g1)
    c: Coincident(g1,g2)
    c: Coincident(g2,g3)
    c: Coincident(g3,g0)
    c: Horizontal(g0)
    c: Horizontal(g2)
    c: Vertical(g1)
    c: Vertical(g3)
    c: DistanceX(g0,g0) = 26.6
    c: DistanceY(g3,g3) = 29.6
    c: Symmetric(g2,g2,g4)
    c: Symmetric(g0,g0,g4)
    c: Symmetric(g3,g3,g5)
    c: Symmetric(g1,g1,g5)
    c: Coincident(g6,g2)
    c: Coincident(g7,g1)
    c: Coincident(g8,g0)
    c: Coincident(g9,g0)
    c: Equal(g9,g6)
    c: Equal(g9,g7)
    c: Equal(g9,g8)
    c: Diameter(g9) = 4
    c: Coincident(g11,g12)
    c: Coincident(g12,g13)
    c: Coincident(g13,g14)
    c: Coincident(g14,g11)
    c: Horizontal(g11)
    c: Horizontal(g13)
    c: Vertical(g12)
    c: Vertical(g14)
    c: Coincident(g11,g10)
    c: Symmetric(g13,g13,g15)
    c: Symmetric(g11,g11,g15)
    c: Symmetric(g14,g14,g16)
    c: Symmetric(g12,g12,g16)
    c: Coincident(g17,g13)
    c: Coincident(g18,g12)
    c: Coincident(g19,g11)
    c: Equal(g17,g18)
    c: Equal(g17,g19)
    c: Equal(g17,g10)
    c: Diameter(g17) = 2.25
    c: DistanceY(g15,g15) = 40.64
    c: DistanceX(g16,g16) = 15.24
    c: DistanceX(g-4,g4) = 16.2
    c: DistanceY(g-4,g5) = 17.5
    c: DistanceX(g15,g-4) = 9
    c: DistanceY(g-4,g16) = 22
    c: Coincident(g22,g20)
    c: Coincident(g22,g21)
    c: Vertical(g22)
    c: Equal(g20,g21)
    c: Diameter(g20) = 4
    c: DistanceY(g22,g22) = 10
    c: DistanceX(g-5,g20) = 8.5
    c: DistanceY(g20,g-5) = 6
FEATURE [Sketcher::SketchObject] Sketch020
  ArcFitTolerance = 1e-06
  FullyConstrained = true
  MakeInternals = false
  MapMode = 5
  Placement = pos=(-31.5,3.5e-14,-1.75e-14) rot=(0.57735,0.57735,0.57735;2.0944rad)
  sketch-geometry (2):
    g0: Circle CenterX=-50.3302 CenterY=-37.8302 CenterZ=0 NormalX=0 NormalY=0 NormalZ=1 AngleXU=0 Radius=2.8
    g1: Circle CenterX=25.3302 CenterY=-37.8302 CenterZ=0 NormalX=0 NormalY=0 NormalZ=1 AngleXU=0 Radius=2.8
  constraints (4):
    c: Coincident(g0,g-3)
    c: Coincident(g1,g-4)
    c: Equal(g1,g0)
    c: Diameter(g1) = 5.6
FEATURE [PartDesign::Pocket] Pocket012  label="Bearing_stopper"
  BaseFeature = -> Pocket010
  Direction = (-1,1.1e-15,0)
  Length = 9.55
  Length2 = 5
  Placement = pos=(0,0,0) rot=(1,1,1;2.0944rad)
  Profile = -> Sketch020
  ReferenceAxis = -> Sketch020 [N_Axis]
  Refine = true
  Suppressed = false
  Type = 0
  expr: Length = 8.15 + 0.7 * 2
FEATURE [Sketcher::SketchObject] Sketch021
  ArcFitTolerance = 1e-06
  AttachmentSupport = -> [XZ_Plane150]
  FullyConstrained = true
  MakeInternals = false
  MapMode = 5
  Placement = pos=(0,0,0) rot=(1,0,0;1.5708rad)
  expr: Constraints[16] = 4.2 / 2
  sketch-geometry (6):
    g0: LineSegment StartX=0 StartY=-2.1 StartZ=0 EndX=0 EndY=-8 EndZ=0
    g1: LineSegment StartX=0 StartY=-8 StartZ=0 EndX=-3 EndY=-8 EndZ=0
    g2: LineSegment StartX=-3 StartY=-8 StartZ=0 EndX=-3 EndY=-4 EndZ=0
    g3: LineSegment StartX=-3 StartY=-4 StartZ=0 EndX=-10 EndY=-4 EndZ=0
    g4: LineSegment StartX=-10 StartY=-4 StartZ=0 EndX=-10 EndY=-2.1 EndZ=0
    g5: LineSegment StartX=-10 StartY=-2.1 StartZ=0 EndX=0 EndY=-2.1 EndZ=0
  constraints (18):
    c: PointOnObject(g0,g-2)
    c: Coincident(g1,g0)
    c: Horizontal(g1)
    c: Coincident(g2,g1)
    c: Vertical(g2)
    c: Coincident(g3,g2)
    c: Horizontal(g3)
    c: Coincident(g4,g3)
    c: Vertical(g4)
    c: DistanceX(g3,g3) = 7
    c: DistanceX(g1,g1) = 3
    c: Horizontal(g5)
    c: Coincident(g0,g5)
    c: Coincident(g4,g5)
    c: DistanceY(g3,g-1) = 4
    c: DistanceY(g0,g-1) = 8
    c: DistanceY(g4,g-1) = 2.1
    c: Vertical(g0)
FEATURE [PartDesign::Revolution] Revolution
  Angle = 360
  Angle2 = 60
  Axis = (1,0,0)
  Base = (0,0,0)
  Placement = pos=(0,0,0) rot=(1,0,0;1.5708rad)
  Profile = -> Sketch021
  ReferenceAxis = -> Sketch021 [H_Axis]
  Refine = true
  Reversed = true
  Suppressed = false
  Type = 0
FEATURE [PartDesign::Fillet] Fillet012
  Base = -> Revolution [Edge2]
  BaseFeature = -> Revolution
  Placement = pos=(0,0,0) rot=(1,0,0;1.5708rad)
  Radius = 1
  Refine = true
  SupportTransform = false
  Suppressed = false
  UseAllEdges = false
FEATURE [PartDesign::Body] Body006  label="Bearing_Stopper"
  AllowCompound = false
  Group = -> [Sketch021,Revolution,Fillet012]
  Origin = -> Origin150
  Placement = pos=(-21.5,25.5,-38) rot=(0,0,1;0rad)
  Tip = -> Fillet012
FEATURE [PartDesign::Pad] Pad008  label="PCBs_Stand"
  BaseFeature = -> Pocket012
  Direction = (-1,0,0)
  Length = 2
  Length2 = 10
  Placement = pos=(0,0,0) rot=(1,1,1;2.0944rad)
  Profile = -> Sketch019
  ReferenceAxis = -> Sketch019 [N_Axis]
  Refine = true
  Suppressed = false
  Type = 0
FEATURE [Sketcher::SketchObject] Sketch022
  ArcFitTolerance = 1e-06
  AttachmentSupport = -> [Pad008]
  ExternalGeometry = -> [Pad008]
  FullyConstrained = true
  MakeInternals = false
  MapMode = 5
  Placement = pos=(-68,0,0) rot=(0.57735,0.57735,-0.57735;4.18879rad)
  sketch-geometry (8):
    g0: Circle CenterX=-54.6 CenterY=-12.7 CenterZ=0 NormalX=0 NormalY=0 NormalZ=1 AngleXU=0 Radius=1.375
    g1: Circle CenterX=-54.6 CenterY=-42.3 CenterZ=0 NormalX=0 NormalY=0 NormalZ=1 AngleXU=0 Radius=1.375
    g2: Circle CenterX=-28 CenterY=-12.7 CenterZ=0 NormalX=0 NormalY=0 NormalZ=1 AngleXU=0 Radius=1.375
    g3: Circle CenterX=-28 CenterY=-42.3 CenterZ=0 NormalX=0 NormalY=0 NormalZ=1 AngleXU=0 Radius=1.375
    g4: Circle CenterX=15.88 CenterY=-2.68 CenterZ=0 NormalX=0 NormalY=0 NormalZ=1 AngleXU=0 Radius=0.625
    g5: Circle CenterX=31.12 CenterY=-2.68 CenterZ=0 NormalX=0 NormalY=0 NormalZ=1 AngleXU=0 Radius=0.625
    g6: Circle CenterX=15.88 CenterY=-43.32 CenterZ=0 NormalX=0 NormalY=0 NormalZ=1 AngleXU=0 Radius=0.625
    g7: Circle CenterX=31.12 CenterY=-43.32 CenterZ=0 NormalX=0 NormalY=0 NormalZ=1 AngleXU=0 Radius=0.625
  constraints (16):
    c: Coincident(g0,g-3)
    c: Coincident(g1,g-5)
    c: Coincident(g2,g-4)
    c: Coincident(g3,g-6)
    c: Coincident(g4,g-7)
    c: Coincident(g5,g-8)
    c: Coincident(g6,g-10)
    c: Coincident(g7,g-9)
    c: Equal(g6,g7)
    c: Equal(g6,g5)
    c: Equal(g6,g4)
    c: Diameter(g6) = 1.25
    c: Equal(g0,g2)
    c: Equal(g0,g3)
    c: Equal(g0,g1)
    c: Diameter(g0) = 2.75
FEATURE [PartDesign::Pad] Pad009  label="PCBs_Pins"
  BaseFeature = -> Pad008
  Direction = (-1,0,0)
  Length = 1
  Length2 = 10
  Placement = pos=(0,0,0) rot=(1,1,1;2.0944rad)
  Profile = -> Sketch022
  ReferenceAxis = -> Sketch022 [N_Axis]
  Refine = true
  Suppressed = false
  Type = 0
FEATURE [Sketcher::SketchObject] Sketch023
  ArcFitTolerance = 1e-06
  AttachmentSupport = -> [Pad009]
  ExternalGeometry = -> [Pad009]
  FullyConstrained = true
  MakeInternals = false
  MapMode = 5
  Placement = pos=(-86,0,0) rot=(0.57735,0.57735,-0.57735;4.18879rad)
  sketch-geometry (11):
    g0: LineSegment [constr] StartX=-12.5 StartY=45 StartZ=0 EndX=-7.5 EndY=44.5 EndZ=0
    g1: LineSegment StartX=-7.5 StartY=44.5 StartZ=0 EndX=42.5 EndY=44.5 EndZ=0
    g2: LineSegment [constr] StartX=-22.5 StartY=45 StartZ=0 EndX=-12.5 EndY=45 EndZ=0
    g3: LineSegment [constr] StartX=-12.5 StartY=45 StartZ=0 EndX=-12.5 EndY=31 EndZ=0
    g4: LineSegment [constr] StartX=-22.5 StartY=45 StartZ=0 EndX=-22.5 EndY=27 EndZ=0
    g5: LineSegment [constr] StartX=-12.5 StartY=31 StartZ=0 EndX=-22.5 EndY=31 EndZ=0
    g6: LineSegment StartX=-7.5 StartY=44.5 StartZ=0 EndX=-7.5 EndY=31.5 EndZ=0
    g7: LineSegment [constr] StartX=-12.5 StartY=31 StartZ=0 EndX=-7.5 EndY=31.5 EndZ=0
    g8: LineSegment StartX=-7.5 StartY=31.5 StartZ=0 EndX=42.5 EndY=31.5 EndZ=0
    g9: LineSegment StartX=42.5 StartY=31.5 StartZ=0 EndX=42.5 EndY=44.5 EndZ=0
    g10: LineSegment [constr] StartX=-12.5 StartY=38 StartZ=0 EndX=-7.5 EndY=38 EndZ=0
  constraints (29):
    c: Coincident(g1,g0)
    c: PointOnObject(g1,g-5)
    c: Horizontal(g1)
    c: DistanceX(g-3,g0) = 10
    c: Coincident(g2,g-3)
    c: Coincident(g2,g0)
    c: Horizontal(g2)
    c: Coincident(g3,g0)
    c: Vertical(g3)
    c: Coincident(g4,g2)
    c: Coincident(g4,g-4)
    c: Coincident(g5,g3)
    c: PointOnObject(g5,g4)
    c: Horizontal(g5)
    c: Coincident(g6,g0)
    c: Vertical(g6)
    c: Coincident(g7,g3)
    c: Coincident(g7,g6)
    c: Coincident(g8,g6)
    c: PointOnObject(g8,g-5)
    c: Horizontal(g8)
    c: Coincident(g9,g8)
    c: Coincident(g9,g1)
    c: DistanceY(g3,g3) = 14
    c: DistanceX(g2,g0) = 15
    c: DistanceY(g6,g6) = 13
    c: Symmetric(g3,g3,g10)
    c: Symmetric(g6,g6,g10)
    c: Horizontal(g10)
FEATURE [PartDesign::Pocket] Pocket013  label="DC_Open"
  BaseFeature = -> Pad009
  Direction = (1,-1.9e-15,1e-16)
  Length = 20
  Length2 = 5
  Placement = pos=(0,0,0) rot=(1,1,1;2.0944rad)
  Profile = -> Sketch023
  ReferenceAxis = -> Sketch023 [N_Axis]
  Refine = true
  Suppressed = false
  Type = 0
FEATURE [Sketcher::SketchObject] Sketch024
  ArcFitTolerance = 1e-06
  AttachmentSupport = -> [Pocket013]
  ExternalGeometry = -> [Pocket013]
  FullyConstrained = true
  MakeInternals = false
  MapMode = 5
  Placement = pos=(-66,0,0) rot=(0.57735,0.57735,-0.57735;4.18879rad)
  sketch-geometry (8):
    g0: LineSegment StartX=-22.5 StartY=45 StartZ=0 EndX=-22.5 EndY=31 EndZ=0
    g1: LineSegment StartX=-22.5 StartY=31 StartZ=0 EndX=-12.5 EndY=31 EndZ=0
    g2: LineSegment StartX=-22.5 StartY=45 StartZ=0 EndX=-12.5 EndY=45 EndZ=0
    g3: LineSegment [constr] StartX=-12.5 StartY=45 StartZ=0 EndX=-12.5 EndY=31 EndZ=0
    g4: LineSegment StartX=-12.5 StartY=45 StartZ=0 EndX=-7.5 EndY=44.5 EndZ=0
    g5: LineSegment StartX=-12.5 StartY=31 StartZ=0 EndX=-7.5 EndY=31.5 EndZ=0
    g6: LineSegment [constr] StartX=-12.5 StartY=38 StartZ=0 EndX=-7.5 EndY=38 EndZ=0
    g7: LineSegment StartX=-7.5 StartY=44.5 StartZ=0 EndX=-7.5 EndY=31.5 EndZ=0
  constraints (20):
    c: Coincident(g0,g-3)
    c: Vertical(g0)
    c: Coincident(g1,g0)
    c: Horizontal(g1)
    c: Coincident(g2,g0)
    c: Horizontal(g2)
    c: Coincident(g3,g2)
    c: Coincident(g3,g1)
    c: Vertical(g3)
    c: Coincident(g4,g2)
    c: Coincident(g4,g-5)
    c: Coincident(g5,g1)
    c: Coincident(g5,g-5)
    c: Symmetric(g3,g3,g6)
    c: Symmetric(g-5,g-5,g6)
    c: Horizontal(g6)
    c: DistanceX(g0,g2) = 10
    c: DistanceY(g-5,g-5) = 13
    c: Coincident(g7,g4)
    c: Coincident(g7,g5)
FEATURE [PartDesign::Pocket] Pocket014  label="DC_Hole"
  BaseFeature = -> Pocket013
  Direction = (1,-1.4e-15,1e-16)
  Length = 11.5
  Length2 = 5
  Placement = pos=(0,0,0) rot=(1,1,1;2.0944rad)
  Profile = -> Sketch024
  ReferenceAxis = -> Sketch024 [N_Axis]
  Refine = true
  Reversed = true
  Suppressed = false
  Type = 0
FEATURE [Part::Feature] Part__Feature263  label="PCB, DC-DC 4.5-28V to 0.8-20V Output 3A MP1584EN Step Down Buck Converter"
  shape: bbox 22.4 x 1.6 x 17.1 mm, 22 faces (baked)
FEATURE [Part::Feature] Part__Feature264  label="MP1584EN CHIP, DC-DC 4.5-28V to 0.8-20V Output 3A MP1584EN Step Down Buck Converter"
  Placement = pos=(3.7,2.4,0.55) rot=(0,0,1;0rad)
  shape: bbox 5 x 1.6 x 6.8 mm, 106 faces, 9 solids (baked)
FEATURE [Part::Feature] Part__Feature265  label="INDUCTOR, DC-DC 4.5-28V to 0.8-20V Output 3A MP1584EN Step Down Buck Converter"
  Placement = pos=(-4.2,1.6,2.05) rot=(0,0,1;0rad)
  shape: bbox 6.601 x 3.001 x 6.901 mm, 82 faces (baked)
FEATURE [Part::Feature] Part__Feature266  label="SCHOTTKY DIODE, DC-DC 4.5-28V to 0.8-20V Output 3A MP1584EN Step Down Buck Converter"
  Placement = pos=(4.2,2.5,6.55) rot=(0,0,1;0rad)
  shape: bbox 4.4 x 1.8 x 2.6 mm, 36 faces (baked)
FEATURE [Part::Feature] Part__Feature267  label="LARGE SMD CAPACITOR, DC-DC 4.5-28V to 0.8-20V Output 3A MP1584EN Step Down Buck Converter"
  Placement = pos=(9.6,1.6,0) rot=(0,0,1;0rad)
  shape: bbox 1.6 x 1 x 3.2 mm, 18 faces, 3 solids (baked)
FEATURE [Part::Feature] Part__Feature268  label="LARGE SMD CAPACITOR, DC-DC 4.5-28V to 0.8-20V Output 3A MP1584EN Step Down Buck Converter001"
  Placement = pos=(-9.6,1.6,0) rot=(0,1,0;3.14159rad)
  shape: bbox 1.6 x 1 x 3.2 mm, 18 faces, 3 solids (baked)
FEATURE [Part::Feature] Part__Feature269  label="SMD RESISTOR, 104, DC-DC 4.5-28V to 0.8-20V Output 3A MP1584EN Step Down Buck Converter"
  Placement = pos=(1.7,1.6,-5.55) rot=(0,-1,0;1.5708rad)
  shape: bbox 2 x 0.4 x 0.8 mm, 18 faces, 3 solids (baked)
FEATURE [Part::Feature] Part__Feature270  label="SMD RESISTOR, 822, DC-DC 4.5-28V to 0.8-20V Output 3A MP1584EN Step Down Buck Converter"
  Placement = pos=(7,1.6,-2.85) rot=(0,0,1;0rad)
  shape: bbox 0.8 x 0.4 x 2 mm, 18 faces, 3 solids (baked)
FEATURE [Part::Feature] Part__Feature271  label="SMALL SMD CAPACITOR, DC-DC 4.5-28V to 0.8-20V Output 3A MP1584EN Step Down Buck Converter"
  Placement = pos=(7,1.6,3.05) rot=(0,0,1;0rad)
  shape: bbox 0.8 x 0.8 x 1.7 mm, 18 faces, 3 solids (baked)
FEATURE [Part::Feature] Part__Feature272  label="SMD RESISTOR, 104, DC-DC 4.5-28V to 0.8-20V Output 3A MP1584EN Step Down Buck Converter001"
  Placement = pos=(7,2,-0.05) rot=(0,0,1;3.14159rad)
  shape: bbox 0.8 x 0.4 x 2 mm, 18 faces, 3 solids (baked)
FEATURE [Part::Feature] Part__Feature273  label="SMD RESISTOR, 104, DC-DC 4.5-28V to 0.8-20V Output 3A MP1584EN Step Down Buck Converter002"
  Placement = pos=(1.7,1.6,-7.05) rot=(0,-1,0;1.5708rad)
  shape: bbox 2 x 0.4 x 0.8 mm, 18 faces, 3 solids (baked)
FEATURE [Part::Feature] Part__Feature274  label="SMD RESISTOR, 104, DC-DC 4.5-28V to 0.8-20V Output 3A MP1584EN Step Down Buck Converter003"
  Placement = pos=(4.5,1.6,-5.55) rot=(0,-1,0;1.5708rad)
  shape: bbox 2 x 0.4 x 0.8 mm, 18 faces, 3 solids (baked)
FEATURE [Part::Feature] Part__Feature275  label="SMALL SMD CAPACITOR, DC-DC 4.5-28V to 0.8-20V Output 3A MP1584EN Step Down Buck Converter001"
  Placement = pos=(4.5,2.4,-7.05) rot=(0.707107,0,-0.707107;3.14159rad)
  shape: bbox 1.7 x 0.8 x 0.8 mm, 18 faces, 3 solids (baked)
FEATURE [Part::Feature] Part__Feature276  label="SMALL SMD CAPACITOR, DC-DC 4.5-28V to 0.8-20V Output 3A MP1584EN Step Down Buck Converter002"
  Placement = pos=(-2.1,2.4,-3.75) rot=(0.707107,0,-0.707107;3.14159rad)
  shape: bbox 1.7 x 0.8 x 0.8 mm, 18 faces, 3 solids (baked)
FEATURE [Part::Feature] Part__Feature277  label="SMALL SMD CAPACITOR, DC-DC 4.5-28V to 0.8-20V Output 3A MP1584EN Step Down Buck Converter003"
  Placement = pos=(-5.7,2.4,-3.55) rot=(0.707107,0,-0.707107;3.14159rad)
  shape: bbox 1.7 x 0.8 x 0.8 mm, 18 faces, 3 solids (baked)
FEATURE [Part::Feature] Part__Feature278  label="POTENTIOMETER, DC-DC 4.5-28V to 0.8-20V Output 3A MP1584EN Step Down Buck Converter"
  Placement = pos=(-4.6,1.6,-6.55) rot=(0,1,0;1.5708rad)
  shape: bbox 3.803 x 1.66 x 3.103 mm, 386 faces, 6 solids (baked)
FEATURE [App::Part] DC_DC_4_5_28V_to_0_8_20V_Output_3A_MP1584EN_Step_Down_Buck_Converter  label="MP1584EN_Board"
  Group = -> [Part__Feature263,Part__Feature264,Part__Feature265,Part__Feature266,Part__Feature267,Part__Feature268,Part__Feature269,Part__Feature270,Part__Feature271,Part__Feature272,Part__Feature273,Part__Feature274,Part__Feature275,Part__Feature276,Part__Feature277,Part__Feature278]
  Origin = -> Origin151
  Placement = pos=(-68,-48.75,-33.75) rot=(-0.57735,0.57735,0.57735;2.0944rad)
FEATURE [Sketcher::SketchObject] Sketch025
  ArcFitTolerance = 1e-06
  AttachmentSupport = -> [Pocket014]
  ExternalGeometry = -> [Pocket014]
  FullyConstrained = true
  MakeInternals = false
  MapMode = 5
  Placement = pos=(-66,0,-1.478e-13) rot=(0.57735,0.57735,-0.57735;4.18879rad)
  sketch-geometry (12):
    g0: LineSegment StartX=-57.5 StartY=23.25 StartZ=0 EndX=-57.5 EndY=21.25 EndZ=0
    g1: LineSegment StartX=-57.5 StartY=21.25 StartZ=0 EndX=-40.5 EndY=21.25 EndZ=0
    g2: LineSegment StartX=-40.5 StartY=21.25 StartZ=0 EndX=-40.5 EndY=23.25 EndZ=0
    g3: LineSegment StartX=-40.5 StartY=23.25 StartZ=0 EndX=-57.5 EndY=23.25 EndZ=0
    g4: LineSegment StartX=12.75 StartY=-45 StartZ=0 EndX=12.75 EndY=-1 EndZ=0
    g5: LineSegment StartX=12.75 StartY=-1 StartZ=0 EndX=14.75 EndY=-1 EndZ=0
    g6: LineSegment StartX=14.75 StartY=-1 StartZ=0 EndX=14.75 EndY=-45 EndZ=0
    g7: LineSegment StartX=14.75 StartY=-45 StartZ=0 EndX=12.75 EndY=-45 EndZ=0
    g8: LineSegment StartX=-57.5 StartY=-10.25 StartZ=0 EndX=-25.5 EndY=-10.25 EndZ=0
    g9: LineSegment StartX=-25.5 StartY=-10.25 StartZ=0 EndX=-25.5 EndY=-8.25 EndZ=0
    g10: LineSegment StartX=-25.5 StartY=-8.25 StartZ=0 EndX=-57.5 EndY=-8.25 EndZ=0
    g11: LineSegment StartX=-57.5 StartY=-8.25 StartZ=0 EndX=-57.5 EndY=-10.25 EndZ=0
  constraints (36):
    c: Coincident(g0,g1)
    c: Coincident(g1,g2)
    c: Coincident(g2,g3)
    c: Coincident(g3,g0)
    c: Vertical(g0)
    c: Vertical(g2)
    c: Horizontal(g1)
    c: Horizontal(g3)
    c: PointOnObject(g0,g-3)
    c: DistanceY(g0,g-3) = 21.75
    c: DistanceY(g0,g0) = 2
    c: DistanceX(g1,g1) = 17
    c: Coincident(g4,g5)
    c: Coincident(g5,g6)
    c: Coincident(g6,g7)
    c: Coincident(g7,g4)
    c: Vertical(g4)
    c: Vertical(g6)
    c: Horizontal(g5)
    c: Horizontal(g7)
    c: PointOnObject(g4,g-5)
    c: DistanceY(g6,g6) = 44
    c: DistanceX(g4,g6) = 2
    c: DistanceX(g6,g-5) = 17.75
    c: Coincident(g8,g9)
    c: Coincident(g9,g10)
    c: Coincident(g10,g11)
    c: Coincident(g11,g8)
    c: Horizontal(g8)
    c: Horizontal(g10)
    c: Vertical(g9)
    c: Vertical(g11)
    c: PointOnObject(g8,g-3)
    c: DistanceY(g8,g10) = 2
    c: DistanceY(g-5,g8) = 34.75
    c: DistanceX(g10,g10) = 32
FEATURE [PartDesign::Pad] Pad010  label="PCB_Slots"
  BaseFeature = -> Pocket014
  Direction = (-1,0,-2.2e-15)
  Length = 1
  Length2 = 10
  Placement = pos=(0,0,0) rot=(1,1,1;2.0944rad)
  Profile = -> Sketch025
  ReferenceAxis = -> Sketch025 [N_Axis]
  Refine = true
  Suppressed = false
  Type = 0
FEATURE [Sketcher::SketchObject] Sketch026
  ArcFitTolerance = 1e-06
  AttachmentSupport = -> [Pad010]
  ExternalGeometry = -> [Pad010]
  FullyConstrained = true
  MakeInternals = false
  MapMode = 5
  Placement = pos=(-2.2e-15,2e-16,1) rot=(0.707107,0.707107,0;3.14159rad)
  sketch-geometry (8):
    g0: LineSegment StartX=14.75 StartY=-67 StartZ=0 EndX=12.75 EndY=-67 EndZ=0
    g1: LineSegment StartX=12.75 StartY=-67 StartZ=0 EndX=12.75 EndY=-71 EndZ=0
    g2: LineSegment StartX=12.75 StartY=-71 StartZ=0 EndX=14.75 EndY=-71 EndZ=0
    g3: LineSegment [constr] StartX=14.75 StartY=-71 StartZ=0 EndX=14.75 EndY=-67 EndZ=0
    g4: LineSegment StartX=14 StartY=-70 StartZ=0 EndX=14 EndY=-68 EndZ=0
    g5: LineSegment [constr] StartX=14 StartY=-69 StartZ=0 EndX=12.75 EndY=-69 EndZ=0
    g6: ArcOfCircle CenterX=13.7083 CenterY=-71 CenterZ=0 NormalX=0 NormalY=0 NormalZ=1 AngleXU=0 Radius=1.04167 StartAngle=1.33e-14 EndAngle=1.287
    g7: ArcOfCircle CenterX=13.7083 CenterY=-67 CenterZ=0 NormalX=0 NormalY=0 NormalZ=1 AngleXU=0 Radius=1.04167 StartAngle=4.99618 EndAngle=6.28319
  constraints (22):
    c: Coincident(g0,g-3)
    c: Coincident(g0,g-3)
    c: Distance(g1) = 4
    c: Coincident(g1,g0)
    c: Vertical(g1)
    c: Coincident(g2,g1)
    c: Horizontal(g2)
    c: Coincident(g3,g2)
    c: Coincident(g3,g0)
    c: Vertical(g3)
    c: Vertical(g4)
    c: DistanceY(g4,g4) = 2
    c: Symmetric(g4,g4,g5)
    c: Symmetric(g1,g1,g5)
    c: Horizontal(g5)
    c: DistanceX(g4,g2) = 0.75
    c: Coincident(g6,g2)
    c: Coincident(g6,g4)
    c: Coincident(g7,g0)
    c: Coincident(g7,g4)
    c: Perpendicular(g7,g0)
    c: Perpendicular(g6,g2)
FEATURE [PartDesign::Pad] Pad011  label="Arduino_Slot"
  BaseFeature = -> Pad010
  Direction = (2.3e-15,0,-1)
  Length = 44
  Length2 = 10
  Placement = pos=(0,0,0) rot=(1,1,1;2.0944rad)
  Profile = -> Sketch026
  ReferenceAxis = -> Sketch026 [N_Axis]
  Refine = true
  Reversed = true
  Suppressed = false
  Type = 0
FEATURE [Sketcher::SketchObject] Sketch028
  ArcFitTolerance = 1e-06
  AttachmentSupport = -> [Pad011]
  ExternalGeometry = -> [Pad011]
  FullyConstrained = true
  MakeInternals = false
  MapMode = 5
  Placement = pos=(-5.6e-15,-25.5,0) rot=(0.57735,0.57735,0.57735;4.18879rad)
  sketch-geometry (8):
    g0: LineSegment StartX=10.25 StartY=-67 StartZ=0 EndX=8.25 EndY=-67 EndZ=0
    g1: LineSegment StartX=8.25 StartY=-67 StartZ=0 EndX=8.25 EndY=-71 EndZ=0
    g2: LineSegment StartX=8.25 StartY=-71 StartZ=0 EndX=10.25 EndY=-71 EndZ=0
    g3: LineSegment [constr] StartX=10.25 StartY=-71 StartZ=0 EndX=10.25 EndY=-67 EndZ=0
    g4: LineSegment StartX=9.5 StartY=-70 StartZ=0 EndX=9.5 EndY=-68 EndZ=0
    g5: LineSegment [constr] StartX=9.5 StartY=-69 StartZ=0 EndX=8.25 EndY=-69 EndZ=0
    g6: ArcOfCircle CenterX=9.20833 CenterY=-67 CenterZ=0 NormalX=0 NormalY=0 NormalZ=1 AngleXU=0 Radius=1.04167 StartAngle=4.99618 EndAngle=6.28319
    g7: ArcOfCircle CenterX=9.20833 CenterY=-71 CenterZ=0 NormalX=0 NormalY=0 NormalZ=1 AngleXU=0 Radius=1.04167 StartAngle=3.92e-14 EndAngle=1.287
  constraints (22):
    c: Coincident(g0,g-3)
    c: Coincident(g0,g-3)
    c: Distance(g1) = 4
    c: Coincident(g1,g0)
    c: Vertical(g1)
    c: Coincident(g2,g1)
    c: Horizontal(g2)
    c: Coincident(g3,g2)
    c: Coincident(g3,g0)
    c: Vertical(g3)
    c: Distance(g4) = 2
    c: Vertical(g4)
    c: Symmetric(g4,g4,g5)
    c: Symmetric(g1,g1,g5)
    c: Horizontal(g5)
    c: DistanceX(g4,g2) = 0.75
    c: Coincident(g6,g4)
    c: Coincident(g6,g0)
    c: Coincident(g7,g2)
    c: Coincident(g7,g4)
    c: Perpendicular(g6,g0)
    c: Perpendicular(g7,g2)
FEATURE [PartDesign::Pad] Pad012  label="ULN2003_Slot"
  BaseFeature = -> Pad011
  Direction = (0,1,0)
  Length = 32
  Length2 = 10
  Placement = pos=(0,0,0) rot=(1,1,1;2.0944rad)
  Profile = -> Sketch028
  ReferenceAxis = -> Sketch028 [N_Axis]
  Refine = true
  Reversed = true
  Suppressed = false
  Type = 0
FEATURE [Sketcher::SketchObject] Sketch029
  ArcFitTolerance = 1e-06
  AttachmentSupport = -> [Pad012]
  ExternalGeometry = -> [Pad012]
  FullyConstrained = true
  MakeInternals = false
  MapMode = 5
  Placement = pos=(-8.9e-15,-40.5,0) rot=(0.57735,0.57735,0.57735;4.18879rad)
  sketch-geometry (8):
    g0: LineSegment StartX=-23.25 StartY=-67 StartZ=0 EndX=-21.25 EndY=-67 EndZ=0
    g1: LineSegment StartX=-21.25 StartY=-67 StartZ=0 EndX=-21.25 EndY=-71 EndZ=0
    g2: LineSegment StartX=-21.25 StartY=-71 StartZ=0 EndX=-23.25 EndY=-71 EndZ=0
    g3: LineSegment [constr] StartX=-23.25 StartY=-67 StartZ=0 EndX=-23.25 EndY=-71 EndZ=0
    g4: LineSegment StartX=-22.5 StartY=-70 StartZ=0 EndX=-22.5 EndY=-68 EndZ=0
    g5: LineSegment [constr] StartX=-22.5 StartY=-69 StartZ=0 EndX=-21.25 EndY=-69 EndZ=0
    g6: ArcOfCircle CenterX=-22.2083 CenterY=-71 CenterZ=0 NormalX=0 NormalY=0 NormalZ=1 AngleXU=0 Radius=1.04167 StartAngle=1.85459 EndAngle=3.14159
    g7: ArcOfCircle CenterX=-22.2083 CenterY=-67 CenterZ=0 NormalX=0 NormalY=0 NormalZ=1 AngleXU=0 Radius=1.04167 StartAngle=3.14159 EndAngle=4.42859
  constraints (22):
    c: Coincident(g0,g-3)
    c: Coincident(g0,g-3)
    c: Distance(g1) = 4
    c: Coincident(g1,g0)
    c: Vertical(g1)
    c: Coincident(g2,g1)
    c: Horizontal(g2)
    c: Coincident(g3,g0)
    c: Coincident(g3,g2)
    c: Vertical(g3)
    c: Vertical(g4)
    c: DistanceY(g4,g4) = 2
    c: Symmetric(g4,g4,g5)
    c: Symmetric(g1,g1,g5)
    c: Horizontal(g5)
    c: DistanceX(g2,g4) = 0.75
    c: Coincident(g6,g2)
    c: Coincident(g6,g4)
    c: Coincident(g7,g0)
    c: Coincident(g7,g4)
    c: Perpendicular(g6,g2)
    c: Perpendicular(g7,g0)
FEATURE [PartDesign::Pad] Pad013  label="MP1584_Slot"
  BaseFeature = -> Pad012
  Direction = (0,1,0)
  Length = 17
  Length2 = 10
  Placement = pos=(0,0,0) rot=(1,1,1;2.0944rad)
  Profile = -> Sketch029
  ReferenceAxis = -> Sketch029 [N_Axis]
  Refine = true
  Reversed = true
  Suppressed = false
  Type = 0
FEATURE [PartDesign::Fillet] Fillet013
  Base = -> Pad013 [Edge193,Edge191,Edge197,Edge195,Edge199,Edge203,Edge205,Edge201]
  BaseFeature = -> Pad013
  Placement = pos=(0,0,0) rot=(1,1,1;2.0944rad)
  Radius = 0.6
  Refine = true
  SupportTransform = false
  Suppressed = false
  UseAllEdges = false
FEATURE [PartDesign::Fillet] Fillet014
  Base = -> Fillet013 [Edge41,Edge137,Edge177]
  BaseFeature = -> Fillet013
  Placement = pos=(0,0,0) rot=(1,1,1;2.0944rad)
  Radius = 1.5
  Refine = true
  SupportTransform = false
  Suppressed = false
  UseAllEdges = false
FEATURE [PartDesign::Fillet] Fillet015
  Base = -> Fillet014 [Edge47,Edge42,Edge60,Edge55,Edge59]
  BaseFeature = -> Fillet014
  Placement = pos=(0,0,0) rot=(1,1,1;2.0944rad)
  Radius = 1
  Refine = true
  SupportTransform = false
  Suppressed = false
  UseAllEdges = false
FEATURE [PartDesign::Fillet] Fillet016
  Base = -> Fillet015 [Edge32,Edge33,Edge35,Edge34,Edge39,Edge37,Edge38,Edge40]
  BaseFeature = -> Fillet015
  Placement = pos=(0,0,0) rot=(1,1,1;2.0944rad)
  Radius = 0.75
  Refine = true
  SupportTransform = false
  Suppressed = false
  UseAllEdges = false
FEATURE [Sketcher::SketchObject] Sketch030
  ArcFitTolerance = 1e-06
  AttachmentSupport = -> [Fillet016]
  ExternalGeometry = -> [Fillet016]
  FullyConstrained = false
  MakeInternals = false
  MapMode = 5
  Placement = pos=(-31.5,0,0) rot=(0.57735,0.57735,0.57735;2.0944rad)
  sketch-geometry (4):
    g0: Circle CenterX=-50.3302 CenterY=-37.8302 CenterZ=0 NormalX=0 NormalY=0 NormalZ=1 AngleXU=0 Radius=6
    g1: Circle CenterX=25.3302 CenterY=-37.8302 CenterZ=0 NormalX=0 NormalY=0 NormalZ=1 AngleXU=0 Radius=6
    g2: Circle CenterX=-50.3302 CenterY=-37.8302 CenterZ=0 NormalX=0 NormalY=0 NormalZ=1 AngleXU=0 Radius=2
    g3: Circle CenterX=25.3302 CenterY=-37.8302 CenterZ=0 NormalX=0 NormalY=0 NormalZ=1 AngleXU=0 Radius=2
  constraints (6):
    c: Coincident(g0,g-3)
    c: Coincident(g1,g-4)
    c: Equal(g1,g0)
    c: Diameter(g1) = 12
    c: Coincident(g2,g0)
    c: Coincident(g3,g1)
FEATURE [PartDesign::Pad] Pad014  label="Bearing_Separator"
  BaseFeature = -> Fillet016
  Direction = (1,0,0)
  Length = 3
  Length2 = 10
  Placement = pos=(0,0,0) rot=(1,1,1;2.0944rad)
  Profile = -> Sketch030
  ReferenceAxis = -> Sketch030 [N_Axis]
  Refine = true
  Suppressed = false
  Type = 0
FEATURE [Sketcher::SketchObject] Sketch032
  ArcFitTolerance = 1e-06
  AttachmentSupport = -> [YZ_Plane152]
  FullyConstrained = true
  MakeInternals = false
  MapMode = 5
  Placement = pos=(0,0,0) rot=(0.57735,0.57735,0.57735;2.0944rad)
  sketch-geometry (6):
    g0: LineSegment StartX=-67.5 StartY=55 StartZ=0 EndX=-67.5 EndY=-55 EndZ=0
    g1: LineSegment StartX=-67.5 StartY=-55 StartZ=0 EndX=42.5 EndY=-55 EndZ=0
    g2: LineSegment StartX=42.5 StartY=-55 StartZ=0 EndX=42.5 EndY=55 EndZ=0
    g3: LineSegment StartX=42.5 StartY=55 StartZ=0 EndX=-67.5 EndY=55 EndZ=0
    g4: LineSegment [constr] StartX=-12.5 StartY=55 StartZ=0 EndX=-12.5 EndY=-55 EndZ=0
    g5: LineSegment [constr] StartX=-67.5 StartY=0 StartZ=0 EndX=42.5 EndY=0 EndZ=0
  constraints (15):
    c: Coincident(g0,g1)
    c: Coincident(g1,g2)
    c: Coincident(g2,g3)
    c: Coincident(g3,g0)
    c: Vertical(g0)
    c: Vertical(g2)
    c: Horizontal(g1)
    c: DistanceX(g3,g3) = 110
    c: DistanceY(g0,g0) = 110
    c: Symmetric(g3,g3,g4)
    c: Symmetric(g1,g1,g4)
    c: Symmetric(g0,g0,g5)
    c: Symmetric(g2,g2,g5)
    c: Tangent(g5,g-1)
    c: DistanceX(g4,g-1) = 12.5
FEATURE [PartDesign::Pad] Pad016  label="Depth001"
  Direction = (1,0,0)
  Length = 3
  Length2 = 10
  Placement = pos=(0,0,0) rot=(1,1,1;2.0944rad)
  Profile = -> Sketch032
  ReferenceAxis = -> Sketch032 [N_Axis]
  Refine = true
  Reversed = true
  Suppressed = false
  Type = 0
FEATURE [Sketcher::SketchObject] Sketch034
  ArcFitTolerance = 1e-06
  AttachmentSupport = -> [Fillet011]
  ExternalGeometry = -> [Fillet011]
  FullyConstrained = false
  MakeInternals = false
  MapMode = 5
  Placement = pos=(-7e-15,-32,0) rot=(0.57735,0.57735,0.57735;4.18879rad)
  sketch-geometry (5):
    g0: LineSegment StartX=-17.929 StartY=-13 StartZ=0 EndX=-17.929 EndY=-16 EndZ=0
    g1: LineSegment StartX=-17.929 StartY=-16 StartZ=0 EndX=17.929 EndY=-16 EndZ=0
    g2: LineSegment StartX=17.929 StartY=-16 StartZ=0 EndX=17.929 EndY=-13 EndZ=0
    g3: LineSegment StartX=17.929 StartY=-13 StartZ=0 EndX=-17.929 EndY=-13 EndZ=0
    g4: LineSegment [constr] StartX=1.3289e-12 StartY=-13 StartZ=0 EndX=1.3289e-12 EndY=-35 EndZ=0
  constraints (13):
    c: Coincident(g0,g1)
    c: Coincident(g1,g2)
    c: Coincident(g2,g3)
    c: Coincident(g3,g0)
    c: Vertical(g0)
    c: Vertical(g2)
    c: Horizontal(g1)
    c: Horizontal(g3)
    c: DistanceY(g0,g0) = 3
    c: DistanceY(g-3,g0) = 19
    c: Symmetric(g3,g3,g4)
    c: Symmetric(g-3,g-3,g4)
    c: Vertical(g4)
FEATURE [PartDesign::Pad] Pad017  label="Press_Dovetail_Stopper_R"
  BaseFeature = -> Fillet011
  Direction = (-1e-16,1,-1e-15)
  Length = 0.5
  Length2 = 10
  Placement = pos=(0,0,0) rot=(1,1,1;2.0944rad)
  Profile = -> Sketch034
  ReferenceAxis = -> Sketch034 [N_Axis]
  Refine = true
  Suppressed = false
  Type = 0
FEATURE [Sketcher::SketchObject] Sketch035
  ArcFitTolerance = 1e-06
  AttachmentSupport = -> [Pad017]
  ExternalGeometry = -> [Pad017]
  FullyConstrained = false
  MakeInternals = false
  MapMode = 5
  Placement = pos=(1.5e-15,7,0) rot=(0.57735,0.57735,-0.57735;2.0944rad)
  sketch-geometry (5):
    g0: LineSegment StartX=-16.6626 StartY=-13 StartZ=0 EndX=-16.6626 EndY=-16 EndZ=0
    g1: LineSegment StartX=-16.6626 StartY=-16 StartZ=0 EndX=16.6626 EndY=-16 EndZ=0
    g2: LineSegment StartX=16.6626 StartY=-16 StartZ=0 EndX=16.6626 EndY=-13 EndZ=0
    g3: LineSegment StartX=16.6626 StartY=-13 StartZ=0 EndX=-16.6626 EndY=-13 EndZ=0
    g4: LineSegment [constr] StartX=-6.5215e-12 StartY=-16 StartZ=0 EndX=-6.5215e-12 EndY=-35 EndZ=0
  constraints (13):
    c: Coincident(g0,g1)
    c: Coincident(g1,g2)
    c: Coincident(g2,g3)
    c: Coincident(g3,g0)
    c: Vertical(g0)
    c: Vertical(g2)
    c: Horizontal(g1)
    c: Horizontal(g3)
    c: DistanceY(g0,g0) = 3
    c: Symmetric(g1,g1,g4)
    c: Symmetric(g-3,g-3,g4)
    c: Vertical(g4)
    c: DistanceY(g-3,g0) = 19
FEATURE [PartDesign::Pad] Pad018  label="Press_Dovetail_Stopper_L"
  BaseFeature = -> Pad017
  Direction = (0,-1,1.3e-15)
  Length = 0.5
  Length2 = 10
  Placement = pos=(0,0,0) rot=(1,1,1;2.0944rad)
  Profile = -> Sketch035
  ReferenceAxis = -> Sketch035 [N_Axis]
  Refine = true
  Suppressed = false
  Type = 0
FEATURE [PartDesign::Fillet] Fillet017
  Base = -> Pad018 [Edge79,Edge61,Edge104,Edge110]
  BaseFeature = -> Pad018
  Placement = pos=(0,0,0) rot=(1,1,1;2.0944rad)
  Radius = 0.2
  Refine = true
  SupportTransform = false
  Suppressed = false
  UseAllEdges = false
FEATURE [PartDesign::Fillet] Fillet018
  Base = -> Fillet017 [Edge23,Edge30,Edge120,Edge116]
  BaseFeature = -> Fillet017
  Placement = pos=(0,0,0) rot=(1,1,1;2.0944rad)
  Radius = 0.25
  Refine = true
  SupportTransform = false
  Suppressed = false
  UseAllEdges = false
FEATURE [PartDesign::Fillet] Fillet019
  Base = -> Fillet018 [Edge120]
  BaseFeature = -> Fillet018
  Placement = pos=(0,0,0) rot=(1,1,1;2.0944rad)
  Radius = 2
  Refine = true
  SupportTransform = false
  Suppressed = false
  UseAllEdges = false
FEATURE [PartDesign::Body] Body002  label="Drum"
  AllowCompound = false
  Group = -> [Sketch008,Pad005,Sketch009,Pocket003,Sketch010,Pocket004,Sketch014,Pad007,Sketch015,Pocket007,Fillet010,Fillet011,Sketch034,Pad017,Sketch035,Pad018,Fillet017,Fillet018,Fillet019]
  Origin = -> Origin002
  Tip = -> Fillet019
FEATURE [Sketcher::SketchObject] Sketch036
  ArcFitTolerance = 1e-06
  FullyConstrained = true
  MakeInternals = false
  MapMode = 5
  Placement = pos=(-1.5e-14,-67.5,3e-14) rot=(0.57735,0.57735,-0.57735;2.0944rad)
  sketch-geometry (9):
    g0: LineSegment StartX=55 StartY=5.16e-14 StartZ=0 EndX=55 EndY=3 EndZ=0
    g1: LineSegment StartX=55 StartY=3 StartZ=0 EndX=54 EndY=3 EndZ=0
    g2: LineSegment [constr] StartX=54 StartY=3 StartZ=0 EndX=54 EndY=5.11e-14 EndZ=0
    g3: LineSegment StartX=54 StartY=3 StartZ=0 EndX=53.5657 EndY=2.56569 EndZ=0
    g4: LineSegment StartX=53.5657 StartY=1.43431 StartZ=0 EndX=54 EndY=1 EndZ=0
    g5: LineSegment StartX=54 StartY=1 StartZ=0 EndX=54 EndY=5.11e-14 EndZ=0
    g6: LineSegment StartX=54 StartY=5.11e-14 StartZ=0 EndX=55 EndY=5.16e-14 EndZ=0
    g7: ArcOfCircle CenterX=54.1314 CenterY=2 CenterZ=0 NormalX=0 NormalY=0 NormalZ=1 AngleXU=0 Radius=0.8 StartAngle=2.35619 EndAngle=3.92699
    g8: GeomPoint [constr] X=53 Y=2 Z=0
  constraints (23):
    c: PointOnObject(g2,g-3)
    c: Distance(g0) = 3
    c: Vertical(g0)
    c: Distance(g1) = 1
    c: Coincident(g1,g0)
    c: Horizontal(g1)
    c: Coincident(g2,g1)
    c: Vertical(g2)
    c: Coincident(g3,g1)
    c: Perpendicular(g4,g3)
    c: DistanceX(g8,g1) = 1
    c: Coincident(g0,g-3)
    c: DistanceY(g4,g1) = 2
    c: PointOnObject(g4,g2)
    c: Coincident(g5,g4)
    c: Coincident(g5,g2)
    c: Coincident(g6,g2)
    c: Coincident(g6,g0)
    c: PointOnObject(g8,g4)
    c: PointOnObject(g8,g3)
    c: Tangent(g4,g7) = -1.5708
    c: Tangent(g3,g7) = -1.5708
    c: Radius(g7) = 0.8
FEATURE [PartDesign::AdditivePipe] AdditivePipe  label="Rear_Snap_fit"
  AuxilleryCurvelinear = true
  AuxillerySpineTangent = false
  BaseFeature = -> Pad016
  Binormal = (0,0,0)
  Mode = 0
  Placement = pos=(0,0,0) rot=(1,1,1;2.0944rad)
  Profile = -> Sketch036
  Refine = true
  Spine = -> Pad016 [Edge6,Edge9,Edge11,Edge3]
  SpineTangent = false
  Suppressed = false
  Transformation = 0
  Transition = 2
FEATURE [Sketcher::SketchObject] Sketch038
  ArcFitTolerance = 1e-06
  AttachmentSupport = -> [YZ_Plane153]
  FullyConstrained = true
  MakeInternals = false
  MapMode = 5
  Placement = pos=(0,0,0) rot=(0.57735,0.57735,0.57735;2.0944rad)
  sketch-geometry (6):
    g0: LineSegment StartX=-67.5 StartY=55 StartZ=0 EndX=-67.5 EndY=-55 EndZ=0
    g1: LineSegment StartX=-67.5 StartY=-55 StartZ=0 EndX=42.5 EndY=-55 EndZ=0
    g2: LineSegment StartX=42.5 StartY=-55 StartZ=0 EndX=42.5 EndY=55 EndZ=0
    g3: LineSegment StartX=42.5 StartY=55 StartZ=0 EndX=-67.5 EndY=55 EndZ=0
    g4: LineSegment [constr] StartX=-12.5 StartY=55 StartZ=0 EndX=-12.5 EndY=-55 EndZ=0
    g5: LineSegment [constr] StartX=-67.5 StartY=0 StartZ=0 EndX=42.5 EndY=0 EndZ=0
  constraints (15):
    c: Coincident(g0,g1)
    c: Coincident(g1,g2)
    c: Coincident(g2,g3)
    c: Coincident(g3,g0)
    c: Vertical(g0)
    c: Vertical(g2)
    c: Horizontal(g1)
    c: DistanceX(g3,g3) = 110
    c: DistanceY(g0,g0) = 110
    c: Symmetric(g3,g3,g4)
    c: Symmetric(g1,g1,g4)
    c: Symmetric(g0,g0,g5)
    c: Symmetric(g2,g2,g5)
    c: Tangent(g5,g-1)
    c: DistanceX(g4,g-1) = 12.5
FEATURE [PartDesign::Pad] Pad019  label="Depth002"
  Direction = (1,0,0)
  Length = 3
  Length2 = 10
  Placement = pos=(0,0,0) rot=(1,1,1;2.0944rad)
  Profile = -> Sketch038
  ReferenceAxis = -> Sketch038 [N_Axis]
  Refine = true
  Reversed = true
  Suppressed = false
  Type = 0
FEATURE [Sketcher::SketchObject] Sketch039
  ArcFitTolerance = 1e-06
  FullyConstrained = true
  MakeInternals = false
  MapMode = 5
  Placement = pos=(-1.5e-14,-67.5,3e-14) rot=(0.57735,0.57735,-0.57735;2.0944rad)
  sketch-geometry (9):
    g0: LineSegment StartX=55 StartY=5.16e-14 StartZ=0 EndX=55 EndY=3 EndZ=0
    g1: LineSegment StartX=55 StartY=3 StartZ=0 EndX=54 EndY=3 EndZ=0
    g2: LineSegment [constr] StartX=54 StartY=3 StartZ=0 EndX=54 EndY=5.11e-14 EndZ=0
    g3: LineSegment StartX=54 StartY=3 StartZ=0 EndX=53.5657 EndY=2.56568 EndZ=0
    g4: LineSegment StartX=53.5657 StartY=1.43431 StartZ=0 EndX=54 EndY=1 EndZ=0
    g5: LineSegment StartX=54 StartY=1 StartZ=0 EndX=54 EndY=5.11e-14 EndZ=0
    g6: LineSegment StartX=54 StartY=5.11e-14 StartZ=0 EndX=55 EndY=5.16e-14 EndZ=0
    g7: ArcOfCircle CenterX=54.1314 CenterY=2 CenterZ=0 NormalX=0 NormalY=0 NormalZ=1 AngleXU=0 Radius=0.8 StartAngle=2.3562 EndAngle=3.92699
    g8: GeomPoint [constr] X=53 Y=1.99999 Z=0
  constraints (23):
    c: PointOnObject(g2,g-3)
    c: Distance(g0) = 3
    c: Vertical(g0)
    c: Distance(g1) = 1
    c: Coincident(g1,g0)
    c: Horizontal(g1)
    c: Coincident(g2,g1)
    c: Vertical(g2)
    c: Coincident(g3,g1)
    c: Perpendicular(g4,g3)
    c: DistanceX(g8,g1) = 1
    c: Coincident(g0,g-3)
    c: DistanceY(g4,g1) = 2
    c: PointOnObject(g4,g2)
    c: Coincident(g5,g4)
    c: Coincident(g5,g2)
    c: Coincident(g6,g2)
    c: Coincident(g6,g0)
    c: PointOnObject(g8,g3)
    c: PointOnObject(g8,g4)
    c: Tangent(g3,g7) = -1.5708
    c: Tangent(g4,g7) = -1.5708
    c: Radius(g7) = 0.8
FEATURE [PartDesign::AdditivePipe] AdditivePipe002  label="Front_snap_fit"
  AuxilleryCurvelinear = true
  AuxillerySpineTangent = false
  BaseFeature = -> Pad019
  Binormal = (0,0,0)
  Mode = 0
  Placement = pos=(0,0,0) rot=(1,1,1;2.0944rad)
  Profile = -> Sketch039
  Refine = true
  Spine = -> Pad019 [Edge6,Edge9,Edge11,Edge3]
  SpineTangent = false
  Suppressed = false
  Transformation = 0
  Transition = 2
FEATURE [Sketcher::SketchObject] Sketch040
  ArcFitTolerance = 1e-06
  FullyConstrained = true
  MakeInternals = false
  MapMode = 5
  Placement = pos=(1.441e-13,-3.289e-13,-55) rot=(0.707107,0.707107,0;3.14159rad)
  sketch-geometry (13):
    g0: LineSegment StartX=41.5 StartY=-2 StartZ=0 EndX=40.6414 EndY=-1.14142 EndZ=0
    g1: LineSegment StartX=40.6414 StartY=-0.858579 StartZ=0 EndX=41.1586 EndY=-0.341421 EndZ=0
    g2: LineSegment StartX=41.0172 StartY=-1.537e-13 StartZ=0 EndX=40.5 EndY=-1.537e-13 EndZ=0
    g3: LineSegment [constr] StartX=41.5 StartY=-1.537e-13 StartZ=0 EndX=41.5 EndY=-2 EndZ=0
    g4: LineSegment [constr] StartX=40.5 StartY=-1 StartZ=0 EndX=41.5 EndY=-1 EndZ=0
    g5: ArcOfCircle CenterX=41.0172 CenterY=-0.2 CenterZ=0 NormalX=0 NormalY=0 NormalZ=1 AngleXU=0 Radius=0.2 StartAngle=5.49779 EndAngle=7.85398
    g6: GeomPoint [constr] X=41.5 Y=-1.537e-13 Z=0
    g7: ArcOfCircle CenterX=40.7828 CenterY=-1 CenterZ=0 NormalX=0 NormalY=0 NormalZ=1 AngleXU=0 Radius=0.2 StartAngle=2.35619 EndAngle=3.92699
    g8: GeomPoint [constr] X=40.5 Y=-1 Z=0
    g9: LineSegment StartX=40.5 StartY=-1.537e-13 StartZ=0 EndX=40.5 EndY=1 EndZ=0
    g10: LineSegment StartX=40.5 StartY=1 StartZ=0 EndX=43.5 EndY=1 EndZ=0
    g11: LineSegment StartX=43.5 StartY=1 StartZ=0 EndX=43.5 EndY=-2 EndZ=0
    g12: LineSegment StartX=41.5 StartY=-2 StartZ=0 EndX=43.5 EndY=-2 EndZ=0
  constraints (33):
    c: Horizontal(g2)
    c: Perpendicular(g0,g1)
    c: Coincident(g3,g6)
    c: Vertical(g3)
    c: Coincident(g4,g8)
    c: Symmetric(g3,g3,g4)
    c: Horizontal(g4)
    c: PointOnObject(g6,g2)
    c: PointOnObject(g6,g1)
    c: Tangent(g2,g5) = -1.5708
    c: Tangent(g1,g5) = -1.5708
    c: Radius(g5) = 0.2
    c: PointOnObject(g8,g0)
    c: PointOnObject(g8,g1)
    c: Tangent(g0,g7) = 1.5708
    c: Tangent(g1,g7) = 1.5708
    c: Radius(g7) = 0.2
    c: DistanceY(g0,g2) = 2
    c: Coincident(g3,g0)
    c: DistanceX(g2,g0) = 1
    c: DistanceX(g0,g-3) = 1
    c: DistanceY(g0,g-3) = 2
    c: Distance(g9) = 1
    c: Coincident(g9,g2)
    c: Vertical(g9)
    c: Distance(g10) = 3
    c: Coincident(g10,g9)
    c: Horizontal(g10)
    c: Coincident(g11,g10)
    c: Vertical(g11)
    c: Coincident(g12,g0)
    c: Coincident(g12,g11)
    c: Horizontal(g12)
FEATURE [Sketcher::SketchObject] Sketch041
  ArcFitTolerance = 1e-06
  AttachmentSupport = -> [AdditivePipe002]
  FullyConstrained = true
  MakeInternals = false
  MapMode = 5
  Placement = pos=(-3,0,0) rot=(0.57735,0.57735,-0.57735;4.18879rad)
  sketch-geometry (1):
    g0: Circle CenterX=-12.5 CenterY=0 CenterZ=0 NormalX=0 NormalY=0 NormalZ=1 AngleXU=0 Radius=39
  constraints (3):
    c: PointOnObject(g0,g-1)
    c: DistanceX(g0,g-1) = 12.5
    c: Diameter(g0) = 78
FEATURE [PartDesign::Pocket] Pocket015
  BaseFeature = -> AdditivePipe002
  Direction = (1,0,0)
  Length = 5
  Length2 = 5
  Placement = pos=(0,0,0) rot=(1,1,1;2.0944rad)
  Profile = -> Sketch041
  ReferenceAxis = -> Sketch041 [N_Axis]
  Refine = true
  Suppressed = false
  Type = 0
FEATURE [Sketcher::SketchObject] Sketch042
  ArcFitTolerance = 1e-06
  AttachmentSupport = -> [Pocket015]
  ExternalGeometry = -> [Pocket015]
  FullyConstrained = true
  MakeInternals = false
  MapMode = 5
  Placement = pos=(0,0,0) rot=(0.57735,0.57735,0.57735;2.0944rad)
  sketch-geometry (1):
    g0: Circle CenterX=-12.5 CenterY=0 CenterZ=0 NormalX=0 NormalY=0 NormalZ=1 AngleXU=0 Radius=43
  constraints (2):
    c: Coincident(g0,g-3)
    c: Diameter(g0) = 86
FEATURE [PartDesign::Pocket] Pocket016
  BaseFeature = -> Pocket015
  Direction = (-1,0,0)
  Length = 0.5
  Length2 = 5
  Placement = pos=(0,0,0) rot=(1,1,1;2.0944rad)
  Profile = -> Sketch042
  ReferenceAxis = -> Sketch042 [N_Axis]
  Refine = true
  Suppressed = false
  Type = 0
FEATURE [PartDesign::Fillet] Fillet020
  Base = -> Pocket016 [Edge30]
  BaseFeature = -> Pocket016
  Placement = pos=(0,0,0) rot=(1,1,1;2.0944rad)
  Radius = 0.3
  Refine = true
  SupportTransform = false
  Suppressed = false
  UseAllEdges = false
FEATURE [PartDesign::Fillet] Fillet021
  Base = -> Fillet020 [Edge12]
  BaseFeature = -> Fillet020
  Placement = pos=(0,0,0) rot=(1,1,1;2.0944rad)
  Radius = 2
  Refine = true
  SupportTransform = false
  Suppressed = false
  UseAllEdges = false
FEATURE [PartDesign::Fillet] Fillet022
  Base = -> Fillet021 [Edge8,Edge10,Edge9,Edge7,Edge15,Edge13,Edge18,Edge17]
  BaseFeature = -> Fillet021
  Placement = pos=(0,0,0) rot=(1,1,1;2.0944rad)
  Radius = 2
  Refine = true
  SupportTransform = false
  Suppressed = false
  UseAllEdges = false
FEATURE [PartDesign::Body] Body008  label="Front_Cover"
  AllowCompound = false
  Group = -> [Sketch038,Pad019,Sketch039,AdditivePipe002,Sketch041,Pocket015,Sketch042,Pocket016,Fillet020,Fillet021,Fillet022]
  Origin = -> Origin153
  Placement = pos=(1,0,-3.8e-15) rot=(0,1,0;3.14159rad)
  Tip = -> Fillet022
FEATURE [PartDesign::SubtractivePipe] SubtractivePipe  label="Front_Snapfit"
  AuxilleryCurvelinear = true
  AuxillerySpineTangent = false
  BaseFeature = -> Pad014
  Binormal = (0,0,0)
  Mode = 0
  Placement = pos=(0,0,0) rot=(1,1,1;2.0944rad)
  Profile = -> Sketch040
  Refine = true
  Spine = -> Pad014 [Edge159,Edge244,Edge245,Edge246]
  SpineTangent = false
  Suppressed = false
  Transformation = 0
  Transition = 2
FEATURE [Sketcher::SketchObject] Sketch043
  ArcFitTolerance = 1e-06
  AttachmentSupport = -> [AdditivePipe]
  FullyConstrained = false
  MakeInternals = false
  MapMode = 5
  Placement = pos=(0,0,0) rot=(0.57735,0.57735,0.57735;2.0944rad)
  sketch-geometry (10):
    g0: LineSegment StartX=-24.55 StartY=-32.1686 StartZ=0 EndX=-24.55 EndY=-30.1686 EndZ=0
    g1: LineSegment StartX=-24.55 StartY=-30.1686 StartZ=0 EndX=-29.55 EndY=-30.1686 EndZ=0
    g2: LineSegment StartX=-29.55 StartY=-30.1686 StartZ=0 EndX=-29.55 EndY=-32.1686 EndZ=0
    g3: LineSegment StartX=-29.55 StartY=-32.1686 StartZ=0 EndX=-24.55 EndY=-32.1686 EndZ=0
    g4: LineSegment StartX=-24.55 StartY=-44.7153 StartZ=0 EndX=-24.55 EndY=-42.7153 EndZ=0
    g5: LineSegment StartX=-24.55 StartY=-42.7153 StartZ=0 EndX=-29.55 EndY=-42.7153 EndZ=0
    g6: LineSegment StartX=-29.55 StartY=-42.7153 StartZ=0 EndX=-29.55 EndY=-44.7153 EndZ=0
    g7: LineSegment StartX=-29.55 StartY=-44.7153 StartZ=0 EndX=-24.55 EndY=-44.7153 EndZ=0
    g8: LineSegment [constr] StartX=-24.55 StartY=-32.1686 StartZ=0 EndX=-24.55 EndY=-42.7153 EndZ=0
    g9: LineSegment [constr] StartX=-29.55 StartY=-32.1686 StartZ=0 EndX=-29.55 EndY=-42.7153 EndZ=0
  constraints (25):
    c: Coincident(g0,g1)
    c: Coincident(g1,g2)
    c: Coincident(g2,g3)
    c: Coincident(g3,g0)
    c: Vertical(g0)
    c: Vertical(g2)
    c: Horizontal(g1)
    c: Horizontal(g3)
    c: Distance(g0,g2) = 5
    c: Distance(g1,g3) = 2
    c: Coincident(g4,g5)
    c: Coincident(g5,g6)
    c: Coincident(g6,g7)
    c: Coincident(g7,g4)
    c: Vertical(g4)
    c: Vertical(g6)
    c: Horizontal(g5)
    c: Horizontal(g7)
    c: Distance(g5,g7) = 2
    c: Coincident(g8,g0)
    c: Coincident(g8,g4)
    c: Vertical(g8)
    c: Coincident(g9,g2)
    c: Coincident(g9,g5)
    c: Vertical(g9)
FEATURE [PartDesign::Pad] Pad020
  BaseFeature = -> AdditivePipe
  Direction = (1,0,0)
  Length = 15
  Length2 = 10
  Placement = pos=(0,0,0) rot=(1,1,1;2.0944rad)
  Profile = -> Sketch043
  ReferenceAxis = -> Sketch043 [N_Axis]
  Refine = true
  Suppressed = false
  Type = 0
FEATURE [PartDesign::Chamfer] Chamfer
  Angle = 45
  Base = -> Pad020 [Edge59,Edge67]
  BaseFeature = -> Pad020
  ChamferType = 1
  FlipDirection = false
  Placement = pos=(0,0,0) rot=(1,1,1;2.0944rad)
  Refine = true
  Size = 6
  Size2 = 1
  SupportTransform = false
  Suppressed = false
  UseAllEdges = false
FEATURE [PartDesign::Fillet] Fillet025
  Base = -> Chamfer [Edge6,Edge16,Edge3,Edge17,Edge20,Edge19,Edge18,Edge15]
  BaseFeature = -> Chamfer
  Placement = pos=(0,0,0) rot=(1,1,1;2.0944rad)
  Radius = 2
  Refine = true
  SupportTransform = false
  Suppressed = false
  UseAllEdges = false
FEATURE [PartDesign::Fillet] Fillet026
  Base = -> Fillet025 [Edge92,Edge90,Edge91,Edge87,Edge94,Edge89,Edge93,Edge88]
  BaseFeature = -> Fillet025
  Placement = pos=(0,0,0) rot=(1,1,1;2.0944rad)
  Radius = 2
  Refine = true
  SupportTransform = false
  Suppressed = false
  UseAllEdges = false
FEATURE [PartDesign::Body] Body007  label="Rear_Cover"
  AllowCompound = false
  Group = -> [Sketch032,Pad016,Sketch036,AdditivePipe,Sketch043,Pad020,Chamfer,Fillet025,Fillet026]
  Origin = -> Origin152
  Placement = pos=(-87,0,0) rot=(0,0,1;0rad)
  Tip = -> Fillet026
FEATURE [Sketcher::SketchObject] Sketch044
  ArcFitTolerance = 1e-06
  AttachmentSupport = -> [SubtractivePipe]
  ExternalGeometry = -> [SubtractivePipe]
  FullyConstrained = true
  MakeInternals = false
  MapMode = 5
  Placement = pos=(9.4e-15,42.5,0) rot=(0.57735,0.57735,0.57735;4.18879rad)
  sketch-geometry (13):
    g0: LineSegment StartX=53.5172 StartY=-86 StartZ=0 EndX=53 EndY=-86 EndZ=0
    g1: LineSegment [constr] StartX=54 StartY=-86 StartZ=0 EndX=54 EndY=-84 EndZ=0
    g2: LineSegment StartX=53.6586 StartY=-85.6586 StartZ=0 EndX=53.1414 EndY=-85.1414 EndZ=0
    g3: LineSegment StartX=53.1414 StartY=-84.8586 StartZ=0 EndX=54 EndY=-84 EndZ=0
    g4: LineSegment [constr] StartX=53 StartY=-85 StartZ=0 EndX=54 EndY=-85 EndZ=0
    g5: LineSegment StartX=54 StartY=-84 StartZ=0 EndX=56 EndY=-84 EndZ=0
    g6: LineSegment StartX=56 StartY=-84 StartZ=0 EndX=56 EndY=-87 EndZ=0
    g7: LineSegment StartX=56 StartY=-87 StartZ=0 EndX=53 EndY=-87 EndZ=0
    g8: LineSegment StartX=53 StartY=-87 StartZ=0 EndX=53 EndY=-86 EndZ=0
    g9: ArcOfCircle CenterX=53.5172 CenterY=-85.8 CenterZ=0 NormalX=0 NormalY=0 NormalZ=1 AngleXU=0 Radius=0.2 StartAngle=4.71239 EndAngle=7.06858
    g10: GeomPoint [constr] X=54 Y=-86 Z=0
    g11: ArcOfCircle CenterX=53.2828 CenterY=-85 CenterZ=0 NormalX=0 NormalY=0 NormalZ=1 AngleXU=0 Radius=0.2 StartAngle=2.35619 EndAngle=3.92699
    g12: GeomPoint [constr] X=53 Y=-85 Z=0
  constraints (33):
    c: PointOnObject(g10,g-3)
    c: PointOnObject(g0,g-3)
    c: DistanceX(g0,g-3) = 2
    c: DistanceX(g0,g10) = 1
    c: Distance(g1) = 2
    c: Coincident(g1,g10)
    c: Vertical(g1)
    c: Coincident(g3,g1)
    c: Perpendicular(g2,g3)
    c: Coincident(g4,g12)
    c: Symmetric(g1,g1,g4)
    c: Horizontal(g4)
    c: Distance(g5) = 2
    c: Coincident(g5,g1)
    c: Horizontal(g5)
    c: Distance(g6) = 3
    c: Coincident(g6,g5)
    c: Vertical(g6)
    c: Coincident(g7,g6)
    c: Horizontal(g7)
    c: Coincident(g8,g7)
    c: Coincident(g8,g0)
    c: Vertical(g8)
    c: PointOnObject(g10,g2)
    c: PointOnObject(g10,g0)
    c: Tangent(g2,g9) = -1.5708
    c: Tangent(g0,g9) = 1.5708
    c: Radius(g9) = 0.2
    c: PointOnObject(g12,g2)
    c: PointOnObject(g12,g3)
    c: Tangent(g2,g11) = 1.5708
    c: Tangent(g3,g11) = 1.5708
    c: Radius(g11) = 0.2
FEATURE [PartDesign::SubtractivePipe] SubtractivePipe001  label="Rear_Snapfit"
  AuxilleryCurvelinear = true
  AuxillerySpineTangent = false
  BaseFeature = -> SubtractivePipe
  Binormal = (0,0,0)
  Mode = 0
  Placement = pos=(0,0,0) rot=(1,1,1;2.0944rad)
  Profile = -> Sketch044
  Refine = true
  Spine = -> SubtractivePipe [Edge205,Edge159,Edge206,Edge208,Edge155]
  SpineTangent = false
  Suppressed = false
  Transformation = 0
  Transition = 2
FEATURE [PartDesign::Fillet] Fillet027
  Base = -> SubtractivePipe001 [Edge169,Edge167,Edge265,Edge257]
  BaseFeature = -> SubtractivePipe001
  Placement = pos=(0,0,0) rot=(1,1,1;2.0944rad)
  Radius = 2
  Refine = true
  SupportTransform = false
  Suppressed = false
  UseAllEdges = false
FEATURE [PartDesign::Body] Body003  label="Body"
  AllowCompound = false
  Group = -> [Sketch011,Pad006,Sketch012,Pocket005,Sketch013,Pocket006,Sketch016,Pocket008,Sketch017,Pocket009,Sketch018,Pocket010,Sketch019,Sketch020,Pocket012,Pad008,Sketch022,Pad009,Sketch023,Pocket013,Sketch024,Pocket014,Sketch025,Pad010,Sketch026,Pad011,Sketch028,Pad012,Sketch029,Pad013,Fillet013,Fillet014,Fillet015,Fillet016,Sketch030,Pad014,Sketch040,SubtractivePipe,Sketch044,SubtractivePipe001,+1 more]
  Origin = -> Origin005
  Tip = -> Fillet027
FEATURE [App::DocumentObjectGroup] Group001  label="Winder"
  Group = -> [Body003,Body006,Body002,Body008,Body007,Body,Body001]
FEATURE [App::Link] Body009
  LinkedObject = -> Body003
FEATURE [App::FeaturePython] GroundedJoint  # Assembly grounded joint (typed FeaturePython)
  ObjectToGround = -> Body009
FEATURE [App::Link] _8BYJ_48  label="28BYJ-049"
  LinkPlacement = pos=(-85.0002,-12.4942,-7.93388) rot=(0.576736,0.578748,0.576564;2.09204rad)
  LinkedObject = -> Part__Feature012
  Placement = pos=(-85.0002,-12.4942,-7.93388) rot=(0.576736,0.578748,0.576564;2.09204rad)
FEATURE [Part::Feature] Part__Feature279  label="COMPOUND"
  shape: bbox 2e-07 x 2e-07 x 2e-07 mm, 0 faces, 0 solids (baked)
FEATURE [Part::Feature] Part__Feature280  label="SOLID001"
  shape: bbox 5.513 x 5.513 x 10.06 mm, 211 faces (baked)
FEATURE [App::Part] M3x8_Philips_Screw  label="M3x8 Philips Screw"
  Group = -> [Part__Feature279,Part__Feature280]
  Origin = -> Origin155
FEATURE [Part::Feature] Part__Feature281  label="L Bolt M4 x 15 Stainless Steel"
  shape: bbox 7.577 x 19 x 7.577 mm, 31 faces (baked)
FEATURE [Part::Feature] Part__Feature282  label="M3 insert nut brass"
  shape: bbox 4.551 x 5.927 x 4.539 mm, 138 faces (baked)
FEATURE [Part::Feature] Part__Feature283  label="insert"
  shape: bbox 5.209 x 5.209 x 6.394 mm, 170 faces (baked)
FEATURE [App::Part] M4x6mm_threaded_brass_insert
  Group = -> [Part__Feature283]
  Origin = -> Origin156
FEATURE [App::DocumentObjectGroup] Group  label="COTS"
  Group = -> [Part__Feature012,PRODUCT_NAME_1,PCB001,Part__Feature262,Y_JG_WJ_A00220_01,Part__Feature013,DC_DC_4_5_28V_to_0_8_20V_Output_3A_MP1584EN_Step_Down_Buck_Converter,M3x8_Philips_Screw,Part__Feature281,Part__Feature282,M4x6mm_threaded_brass_insert]
FEATURE [App::Link] M3_insert_nut_brass  label="M3 insert nut brass001"
  LinkPlacement = pos=(-66,5,-8) rot=(0,0,1;4.71209rad)
  LinkedObject = -> Part__Feature282
  Placement = pos=(-66,5,-8) rot=(0,0,1;4.71209rad)
FEATURE [App::Link] M3_insert_nut_brass001  label="M3 insert nut brass002"
  LinkPlacement = pos=(-66,-30,-8) rot=(0,0,1;4.71239rad)
  LinkedObject = -> Part__Feature282
  Placement = pos=(-66,-30,-8) rot=(0,0,1;4.71239rad)
FEATURE [App::FeaturePython] Joint  label="Revolute"  # Assembly joint (typed FeaturePython)
  Activated = true
  AngleMax = 0
  AngleMin = 0
  Detach1 = false
  Detach2 = false
  Distance = 0
  Distance2 = 0
  EnableAngleMax = false
  EnableAngleMin = false
  EnableLengthMax = false
  EnableLengthMin = false
  JointType = 1 (Revolute)
  LengthMax = 0
  LengthMin = 0
  Placement1 = pos=(-66,5,-8) rot=(0.57735,0.57735,-0.57735;4.18879rad)
  Placement2 = pos=(0,-1.42e-14,0) rot=(0,-0.707107,-0.707107;3.14159rad)
  Reference1 = -> Assembly [Body009.Edge86,Body009.Edge86]
  Reference2 = -> Assembly [M3_insert_nut_brass.Edge77,M3_insert_nut_brass.Edge77]
FEATURE [App::FeaturePython] Joint001  label="Revolute001"  # Assembly joint (typed FeaturePython)
  Activated = true
  AngleMax = 0
  AngleMin = 0
  Detach1 = false
  Detach2 = false
  Distance = 0
  Distance2 = 0
  EnableAngleMax = false
  EnableAngleMin = false
  EnableLengthMax = false
  EnableLengthMin = false
  JointType = 1 (Revolute)
  LengthMax = 0
  LengthMin = 0
  Placement1 = pos=(-66,-30,-8) rot=(0.57735,0.57735,-0.57735;4.18879rad)
  Placement2 = pos=(0,-1.42e-14,0) rot=(0,-0.707107,-0.707107;3.14159rad)
  Reference1 = -> Assembly [Body009.Edge87,Body009.Edge87]
  Reference2 = -> Assembly [M3_insert_nut_brass001.Edge77,M3_insert_nut_brass001.Edge77]
FEATURE [App::FeaturePython] Joint002  label="Distance"  # Assembly joint (typed FeaturePython)
  Activated = true
  AngleMax = 0
  AngleMin = 0
  Detach1 = false
  Detach2 = false
  Distance = 0
  Distance2 = 0
  EnableAngleMax = false
  EnableAngleMin = false
  EnableLengthMax = false
  EnableLengthMin = false
  JointType = 5 (Distance)
  LengthMax = 0
  LengthMin = 0
  Placement1 = pos=(0.000591433,-1.42663,19) rot=(0,-1,0;3.14159rad)
  Placement2 = pos=(-66,-11.8378,-0.180502) rot=(0.707107,0,-0.707107;3.14159rad)
  Reference1 = -> Assembly [_8BYJ_48.Face12,_8BYJ_48.Face12]
  Reference2 = -> Assembly [Body009.Face6,Body009.Face6]
FEATURE [App::FeaturePython] Joint003  label="Revolute002"  # Assembly joint (typed FeaturePython)
  Activated = true
  AngleMax = 0
  AngleMin = 0
  Detach1 = false
  Detach2 = false
  Distance = 0
  Distance2 = 0
  EnableAngleMax = false
  EnableAngleMin = false
  EnableLengthMax = false
  EnableLengthMin = false
  JointType = 1 (Revolute)
  LengthMax = 0
  LengthMin = 0
  Placement1 = pos=(0,-1.42e-14,0) rot=(0,-0.707107,-0.707107;3.14159rad)
  Placement2 = pos=(17.5,9e-16,18.995) rot=(0,-1,0;3.14159rad)
  Reference1 = -> Assembly [M3_insert_nut_brass.Edge26,M3_insert_nut_brass.Edge26]
  Reference2 = -> Assembly [_8BYJ_48.Edge58,_8BYJ_48.Edge58]
FEATURE [App::Link] M3x8_Philips_Screw001  label="M3x8 Philips Screw001"
  LinkPlacement = pos=(-66.79,5.00023,-8) rot=(-0.707106,0.001441,0.707106;3.14405rad)
  LinkedObject = -> M3x8_Philips_Screw
  Placement = pos=(-66.79,5.00023,-8) rot=(-0.707106,0.001441,0.707106;3.14405rad)
FEATURE [App::Link] M3x8_Philips_Screw002  label="M3x8 Philips Screw002"
  LinkPlacement = pos=(-66.8004,-29.9992,-7.86776) rot=(-0.707106,0.001441,0.707106;3.14405rad)
  LinkedObject = -> M3x8_Philips_Screw
  Placement = pos=(-66.8004,-29.9992,-7.86776) rot=(-0.707106,0.001441,0.707106;3.14405rad)
FEATURE [App::FeaturePython] Joint004  label="Revolute003"  # Assembly joint (typed FeaturePython)
  Activated = true
  AngleMax = 0
  AngleMin = 0
  Detach1 = false
  Detach2 = false
  Distance = 0
  Distance2 = 0
  EnableAngleMax = false
  EnableAngleMin = false
  EnableLengthMax = false
  EnableLengthMin = false
  JointType = 1 (Revolute)
  LengthMax = 0
  LengthMin = 0
  Placement1 = pos=(0,0,0) rot=(-0.707107,0.707107,0;3.14159rad)
  Placement2 = pos=(17.5,9e-16,18.205) rot=(0,0,1;0rad)
  Reference1 = -> Assembly [M3x8_Philips_Screw001.Part__Feature280.Edge328,M3x8_Philips_Screw001.Part__Feature280.Edge328]
  Reference2 = -> Assembly [_8BYJ_48.Edge64,_8BYJ_48.Edge64]
FEATURE [App::FeaturePython] Joint005  label="Revolute004"  # Assembly joint (typed FeaturePython)
  Activated = true
  AngleMax = 0
  AngleMin = 0
  Detach1 = false
  Detach2 = false
  Distance = 0
  Distance2 = 0
  EnableAngleMax = false
  EnableAngleMin = false
  EnableLengthMax = false
  EnableLengthMin = false
  JointType = 1 (Revolute)
  LengthMax = 0
  LengthMin = 0
  Placement1 = pos=(-17.4997,0,18.205) rot=(0,0,1;0rad)
  Placement2 = pos=(0,0,0) rot=(-0.707107,0.707107,0;3.14159rad)
  Reference1 = -> Assembly [_8BYJ_48.Edge70,_8BYJ_48.Edge70]
  Reference2 = -> Assembly [M3x8_Philips_Screw002.Part__Feature280.Edge328,M3x8_Philips_Screw002.Part__Feature280.Edge328]
FEATURE [App::Link] _08zz  label="608zz001"
  LinkPlacement = pos=(-21.5,-50.3302,-37.8302) rot=(0.707107,0.707107,0;3.14159rad)
  LinkedObject = -> PRODUCT_NAME_1
  Placement = pos=(-21.5,-50.3302,-37.8302) rot=(0.707107,0.707107,0;3.14159rad)
FEATURE [App::Link] _08zz001  label="608zz002"
  LinkPlacement = pos=(-21.5,25.3302,-37.8302) rot=(0.707107,0.707107,0;3.14159rad)
  LinkedObject = -> PRODUCT_NAME_1
  Placement = pos=(-21.5,25.3302,-37.8302) rot=(0.707107,0.707107,0;3.14159rad)
FEATURE [App::Link] Bearing_Stopper  label="Bearing_Stopper001"
  LinkPlacement = pos=(-18.5,-50.3302,-37.8302) rot=(1,0,0;1.5708rad)
  LinkedObject = -> Body006
  Placement = pos=(-18.5,-50.3302,-37.8302) rot=(1,0,0;1.5708rad)
FEATURE [App::Link] Bearing_Stopper001  label="Bearing_Stopper002"
  LinkPlacement = pos=(-18.5,25.3302,-37.8302) rot=(1,0,0;1.5708rad)
  LinkedObject = -> Body006
  Placement = pos=(-18.5,25.3302,-37.8302) rot=(1,0,0;1.5708rad)
FEATURE [App::FeaturePython] Joint006  label="Revolute005"  # Assembly joint (typed FeaturePython)
  Activated = true
  AngleMax = 0
  AngleMin = 0
  Detach1 = false
  Detach2 = false
  Distance = 0
  Distance2 = 0
  EnableAngleMax = false
  EnableAngleMin = false
  EnableLengthMax = false
  EnableLengthMin = false
  JointType = 1 (Revolute)
  LengthMax = 0
  LengthMin = 0
  Placement1 = pos=(-3,0,0) rot=(0.707107,0,-0.707107;3.14159rad)
  Placement2 = pos=(0,0,0) rot=(0.57735,0.57735,0.57735;4.18879rad)
  Reference1 = -> Assembly [Bearing_Stopper.Edge10,Bearing_Stopper.Edge10]
  Reference2 = -> Assembly [_08zz.Part__Feature010.Edge13,_08zz.Part__Feature010.Edge13]
FEATURE [App::FeaturePython] Joint007  label="Revolute006"  # Assembly joint (typed FeaturePython)
  Activated = true
  AngleMax = 0
  AngleMin = 0
  Detach1 = false
  Detach2 = false
  Distance = 0
  Distance2 = 0
  EnableAngleMax = false
  EnableAngleMin = false
  EnableLengthMax = false
  EnableLengthMin = false
  JointType = 1 (Revolute)
  LengthMax = 0
  LengthMin = 0
  Placement1 = pos=(-3,0,0) rot=(0.707107,0,-0.707107;3.14159rad)
  Placement2 = pos=(0,0,0) rot=(0.57735,0.57735,0.57735;4.18879rad)
  Reference1 = -> Assembly [Bearing_Stopper001.Edge10,Bearing_Stopper001.Edge10]
  Reference2 = -> Assembly [_08zz001.Part__Feature010.Edge14,_08zz001.Part__Feature010.Edge14]
FEATURE [App::Link] M4x6mm_threaded_brass_insert001
  LinkPlacement = pos=(-34.5,-50.3302,-37.8302) rot=(0.57735,0.57735,0.57735;2.0944rad)
  LinkedObject = -> M4x6mm_threaded_brass_insert
  Placement = pos=(-34.5,-50.3302,-37.8302) rot=(0.57735,0.57735,0.57735;2.0944rad)
FEATURE [App::Link] M4x6mm_threaded_brass_insert002
  LinkPlacement = pos=(-34.5,25.3302,-37.8302) rot=(0.57735,0.57735,0.57735;2.0944rad)
  LinkedObject = -> M4x6mm_threaded_brass_insert
  Placement = pos=(-34.5,25.3302,-37.8302) rot=(0.57735,0.57735,0.57735;2.0944rad)
FEATURE [App::FeaturePython] Joint008  label="Revolute007"  # Assembly joint (typed FeaturePython)
  Activated = true
  AngleMax = 0
  AngleMin = 0
  Detach1 = false
  Detach2 = false
  Distance = 0
  Distance2 = 0
  EnableAngleMax = false
  EnableAngleMin = false
  EnableLengthMax = false
  EnableLengthMin = false
  JointType = 1 (Revolute)
  LengthMax = 0
  LengthMin = 0
  Placement1 = pos=(-28.5,-50.3302,-37.8302) rot=(0.57735,0.57735,0.57735;2.0944rad)
  Placement2 = pos=(0,0,6) rot=(0,0,1;0rad)
  Reference1 = -> Assembly [Body009.Edge441,Body009.Edge441]
  Reference2 = -> Assembly [M4x6mm_threaded_brass_insert001.Part__Feature283.Edge424,M4x6mm_threaded_brass_insert001.Part__Feature283.Edge424]
FEATURE [App::FeaturePython] Joint009  label="Revolute008"  # Assembly joint (typed FeaturePython)
  Activated = true
  AngleMax = 0
  AngleMin = 0
  Detach1 = false
  Detach2 = false
  Distance = 0
  Distance2 = 0
  EnableAngleMax = false
  EnableAngleMin = false
  EnableLengthMax = false
  EnableLengthMin = false
  JointType = 1 (Revolute)
  LengthMax = 0
  LengthMin = 0
  Placement1 = pos=(-28.5,25.3302,-37.8302) rot=(0.57735,0.57735,0.57735;2.0944rad)
  Placement2 = pos=(0,0,6) rot=(0,0,1;0rad)
  Reference1 = -> Assembly [Body009.Edge440,Body009.Edge440]
  Reference2 = -> Assembly [M4x6mm_threaded_brass_insert002.Part__Feature283.Edge424,M4x6mm_threaded_brass_insert002.Part__Feature283.Edge424]
FEATURE [App::FeaturePython] Joint010  label="Revolute009"  # Assembly joint (typed FeaturePython)
  Activated = true
  AngleMax = 0
  AngleMin = 0
  Detach1 = false
  Detach2 = false
  Distance = 0
  Distance2 = 0
  EnableAngleMax = false
  EnableAngleMin = false
  EnableLengthMax = false
  EnableLengthMin = false
  JointType = 1 (Revolute)
  LengthMax = 0
  LengthMin = 0
  Placement1 = pos=(-10,0,7.1e-15) rot=(0.707107,0,-0.707107;3.14159rad)
  Placement2 = pos=(-28.5,-50.3302,-37.8302) rot=(0.57735,0.57735,0.57735;2.0944rad)
  Reference1 = -> Assembly [Bearing_Stopper.Edge5,Bearing_Stopper.Edge5]
  Reference2 = -> Assembly [Body009.Edge441,Body009.Edge441]
FEATURE [App::FeaturePython] Joint011  label="Revolute010"  # Assembly joint (typed FeaturePython)
  Activated = true
  AngleMax = 0
  AngleMin = 0
  Detach1 = false
  Detach2 = false
  Distance = 0
  Distance2 = 0
  EnableAngleMax = false
  EnableAngleMin = false
  EnableLengthMax = false
  EnableLengthMin = false
  JointType = 1 (Revolute)
  LengthMax = 0
  LengthMin = 0
  Placement1 = pos=(-10,-7.1e-15,0) rot=(0.707107,0,-0.707107;3.14159rad)
  Placement2 = pos=(-28.5,25.3302,-37.8302) rot=(0.57735,0.57735,0.57735;2.0944rad)
  Reference1 = -> Assembly [Bearing_Stopper001.Edge5,Bearing_Stopper001.Edge5]
  Reference2 = -> Assembly [Body009.Edge440,Body009.Edge440]
FEATURE [App::Link] L_Bolt_M4_x_15_Stainless_Steel  label="L Bolt M4 x 15 Stainless Steel001"
  LinkPlacement = pos=(-33.5,-50.3302,-37.8302) rot=(0.707107,0.707107,0;3.14159rad)
  LinkedObject = -> Part__Feature281
  Placement = pos=(-33.5,-50.3302,-37.8302) rot=(0.707107,0.707107,0;3.14159rad)
FEATURE [App::Link] L_Bolt_M4_x_15_Stainless_Steel001  label="L Bolt M4 x 15 Stainless Steel002"
  LinkPlacement = pos=(-33.5,25.3302,-37.8302) rot=(0.707107,0.707107,0;3.14159rad)
  LinkedObject = -> Part__Feature281
  Placement = pos=(-33.5,25.3302,-37.8302) rot=(0.707107,0.707107,0;3.14159rad)
FEATURE [App::FeaturePython] Joint012  label="Revolute011"  # Assembly joint (typed FeaturePython)
  Activated = true
  AngleMax = 0
  AngleMin = 0
  Detach1 = false
  Detach2 = false
  Distance = 0
  Distance2 = 0
  EnableAngleMax = false
  EnableAngleMin = false
  EnableLengthMax = false
  EnableLengthMin = false
  JointType = 1 (Revolute)
  LengthMax = 0
  LengthMin = 0
  Placement1 = pos=(0,15,-7.1e-15) rot=(1,0,0;1.5708rad)
  Placement2 = pos=(0,0,0) rot=(0.707107,0,-0.707107;3.14159rad)
  Reference1 = -> Assembly [L_Bolt_M4_x_15_Stainless_Steel.Edge51,L_Bolt_M4_x_15_Stainless_Steel.Edge51]
  Reference2 = -> Assembly [Bearing_Stopper.Edge2,Bearing_Stopper.Edge2]
FEATURE [App::FeaturePython] Joint013  label="Revolute012"  # Assembly joint (typed FeaturePython)
  Activated = true
  AngleMax = 0
  AngleMin = 0
  Detach1 = false
  Detach2 = false
  Distance = 0
  Distance2 = 0
  EnableAngleMax = false
  EnableAngleMin = false
  EnableLengthMax = false
  EnableLengthMin = false
  JointType = 1 (Revolute)
  LengthMax = 0
  LengthMin = 0
  Placement1 = pos=(0,15,0) rot=(1,0,0;1.5708rad)
  Placement2 = pos=(0,0,0) rot=(0.707107,0,-0.707107;3.14159rad)
  Reference1 = -> Assembly [L_Bolt_M4_x_15_Stainless_Steel001.Edge51,L_Bolt_M4_x_15_Stainless_Steel001.Edge51]
  Reference2 = -> Assembly [Bearing_Stopper001.Edge2,Bearing_Stopper001.Edge2]
FEATURE [App::Link] Drum  label="Drum001"
  LinkPlacement = pos=(0.00351208,0.00253963,0.0271707) rot=(-0.998979,0.000148,-0.078513;0.003782rad)
  LinkedObject = -> Body002
  Placement = pos=(0.00351208,0.00253963,0.0271707) rot=(-0.998979,0.000148,-0.078513;0.003782rad)
FEATURE [App::FeaturePython] Joint014  label="Distancia"  # Assembly joint (typed FeaturePython)
  Activated = true
  AngleMax = 0
  AngleMin = 0
  Detach1 = false
  Detach2 = false
  Distance = 0
  Distance2 = 0
  EnableAngleMax = false
  EnableAngleMin = false
  EnableLengthMax = false
  EnableLengthMin = false
  JointType = 5 (Distance)
  LengthMax = 0
  LengthMin = 0
  Placement1 = pos=(0,8,29) rot=(0,1,0;3.14159rad)
  Placement2 = pos=(-56,-12.5,0) rot=(0.707107,0,0.707107;3.14159rad)
  Reference1 = -> Assembly [_8BYJ_48.Face612,_8BYJ_48.Face612]
  Reference2 = -> Assembly [Drum.Fillet019.Face67,Drum.Fillet019.Face67]
FEATURE [Assembly::JointGroup] Joints
  Group = -> [GroundedJoint,Joint,Joint001,Joint002,Joint003,Joint004,Joint005,Joint006,Joint007,Joint008,Joint009,Joint010,Joint011,Joint012,Joint013,Joint014]
FEATURE [Assembly::AssemblyObject] Assembly
  Group = -> [Joints,Body009,GroundedJoint,_8BYJ_48,M3_insert_nut_brass,M3_insert_nut_brass001,Joint,Joint001,Joint002,Joint003,M3x8_Philips_Screw001,M3x8_Philips_Screw002,Joint004,Joint005,_08zz,_08zz001,Bearing_Stopper,Bearing_Stopper001,Joint006,Joint007,M4x6mm_threaded_brass_insert001,M4x6mm_threaded_brass_insert002,Joint008,Joint009,Joint010,Joint011,L_Bolt_M4_x_15_Stainless_Steel,+5 more]
  Origin = -> Origin154
  Type = Assembly
